FCSTD DOCUMENT  (FreeCAD 0.21R33771 (Git))
Label: ass-tornio
License: All rights reserved
LicenseURL: https://en.wikipedia.org/wiki/All_rights_reserved
objects: App::Link×56, App::DocumentObjectGroup×4, Part::FeaturePython×4, App::AnnotationLabel×4, PartDesign::CoordinateSystem×1, App::FeaturePython×1, App::Part×1
note: 5 computed .brp shape members not serialized (recipe doc carries the construction recipe); baked Part::Feature solids carry a one-line shape summary decoded from their .brp
EXTERNAL_REF file=../Pattino-20.FCStd obj=LCS_Pattino_20
EXTERNAL_REF file=../Pattino-20.FCStd obj=Body
EXTERNAL_REF file=../PiastraCarroUtensile.FCStd obj=LCS_PiastraCarro
EXTERNAL_REF file=../PiastraCarroUtensile.FCStd obj=Body
EXTERNAL_REF file=../TORRETTA/Pattino-15.FCStd obj=LCS_Pattino1
EXTERNAL_REF file=../PiastraTorretta.FCStd obj=LCS_PiastraTorretta
EXTERNAL_REF file=../PiastraTorretta.FCStd obj=Body
EXTERNAL_REF file=../BloccoMandrino/FlangiaSupportoMandrino.FCStd obj=LCS_
EXTERNAL_REF file=../Profilo-C-basamento.FCStd obj=LCS_ProfiloCbasamento
EXTERNAL_REF file=../BloccoMandrino/FlangiaSupportoMandrino.FCStd obj=Body
EXTERNAL_REF file=../SupportoSingoloVite16x4.FCStd obj=LCS_SupportoSingoloVite16x4
EXTERNAL_REF file=../ViteCarro16x4.FCStd obj=LCS_ViteCarro16x4
EXTERNAL_REF file=../ViteCarro16x4.FCStd obj=Body
EXTERNAL_REF file=../SupportoSingoloVite16x4.FCStd obj=Body
EXTERNAL_REF file=../Chiocciola16x4.FCStd obj=LCS_Chiociola16X4
EXTERNAL_REF file=../StaffaChiocciola16x4.FCStd obj=LCS_StaffaChiocciola16x4
EXTERNAL_REF file=../Chiocciola16x4.FCStd obj=Body
EXTERNAL_REF file=../StaffaChiocciola16x4.FCStd obj=Body
EXTERNAL_REF file=../SupportoDoppioVite16x4.FCStd obj=LCS_SupportoDoppioVite16x4
EXTERNAL_REF file=../SupportoDoppioVite16x4.FCStd obj=Body
EXTERNAL_REF file=../Piedino40x40.FCStd obj=LCS_piedino40x40
EXTERNAL_REF file=../Piedino40x40.FCStd obj=Body
EXTERNAL_REF file=../Guida-quadra-20-800.FCStd obj=LCS_GuidaQuadrata_20x800
EXTERNAL_REF file=../Contropunta/PiastraContropunta.FCStd obj=LCS_PiastraContropunta
EXTERNAL_REF file=../Contropunta/PiastraContropunta.FCStd obj=Body
EXTERNAL_REF file=../BloccoMandrino/Flagia-Mandrino.FCStd obj=LCS_FllangiaSupportoMandrino
EXTERNAL_REF file=../BloccoMandrino/Reggispinta35x52x12.FCStd obj=LCS_Reggispinta35x12
EXTERNAL_REF file=../BloccoMandrino/Reggispinta35x52x12.FCStd obj=Body
EXTERNAL_REF file=../TORRETTA/Guida-quadra-15-300.FCStd obj=LCS_GuidoQuadra15x300
EXTERNAL_REF file=../BloccoMandrino/PiastraMandrinoRotante.FCStd obj=LCS_PiastraRotazioneUtensile
EXTERNAL_REF file=../TORRETTA/Guida-quadra-15-300.FCStd obj=Body
EXTERNAL_REF file=../TORRETTA/Pattino-15.FCStd obj=Body
EXTERNAL_REF file=../BloccoMandrino/PiastraMandrinoRotante.FCStd obj=Body
EXTERNAL_REF file=../TORRETTA/SupportoChiocciolaRicircolo12.FCStd obj=LCS_SupportoChiocciolaRicircolo12
EXTERNAL_REF file=../TORRETTA/SupportoChiocciolaRicircolo12.FCStd obj=Body
EXTERNAL_REF file=../TORRETTA/Chiocciola10x2.FCStd obj=LCS_Chiocciola12x2
EXTERNAL_REF file=../TORRETTA/Chiocciola10x2.FCStd obj=Body
EXTERNAL_REF file=../TORRETTA/ViteTrapezioT10.FCStd obj=LCS_ViteTrapezioT10
EXTERNAL_REF file=../TORRETTA/ViteTrapezioT10.FCStd obj=Body
EXTERNAL_REF file=../TORRETTA/TorrettaPortaUtensile.FCStd obj=LCS_TorrettaPortaUtensile
EXTERNAL_REF file=../TORRETTA/TorrettaPortaUtensile.FCStd obj=Body
EXTERNAL_REF file=../BloccoMandrino/Motore-P60B13150HXS00M- SANYO.FCStd obj=LCS_Motore_sanyoP60
EXTERNAL_REF file=../BloccoMandrino/Motore-P60B13150HXS00M- SANYO.FCStd obj=Body
EXTERNAL_REF file=../BloccoMandrino/FlangiaCuscinettoAlberoMandrino.FCStd obj=LCS_FlangiaCuscinettoMandrino
EXTERNAL_REF file=../BloccoMandrino/FlangiaCuscinettoAlberoMandrino.FCStd obj=Body
EXTERNAL_REF file=../BloccoMandrino/CuscinettoSfere30x52x12.FCStd obj=LCS_Cuscinetto30x52x12
EXTERNAL_REF file=../BloccoMandrino/CuscinettoSfere30x52x12.FCStd obj=Body
EXTERNAL_REF file=../Profilo-C-basamento.FCStd obj=Body
EXTERNAL_REF file=../Piatto40x10x850.FCStd obj=LCS_Piatto40x10
EXTERNAL_REF file=../Piatto40x10x850.FCStd obj=Body
EXTERNAL_REF file=../Guida-quadra-20-800.FCStd obj=Body
EXTERNAL_REF file=../Puleggia70-Foro28.FCStd obj=LCS_Puleggia70
EXTERNAL_REF file=../Puleggia70-Foro28.FCStd obj=Body
EXTERNAL_REF file=../BloccoMandrino/Albero-Mandrino30.FCStd obj=LCS_AlberoMandrino
EXTERNAL_REF file=../BloccoMandrino/Flagia-Mandrino.FCStd obj=Body
EXTERNAL_REF file=../BloccoMandrino/Albero-Mandrino30.FCStd obj=Body
EXTERNAL_REF file=../BloccoMandrino/Mandrino.FCStd obj=LCS_Mandrino
EXTERNAL_REF file=../BloccoMandrino/Mandrino.FCStd obj=Body
EXTERNAL_REF file=../DistanzialeBasamentoC.FCStd obj=LCS_DistanzialeBasamentoC
EXTERNAL_REF file=../DistanzialeBasamentoC.FCStd obj=Body
EXTERNAL_REF file=../Cremagliera-M1.FCStd obj=LCS_Cremagliera_800
EXTERNAL_REF file=../Cremagliera-M1.FCStd obj=Part
EXTERNAL_REF file=../PiastraAvanzamentoCarro.FCStd obj=LCS_PiastraAvanzamentoUtensile
EXTERNAL_REF file=../Pignone13-M1.FCStd obj=LCS_Pignone13M1
EXTERNAL_REF file=../Pignone13-M1.FCStd obj=Part
EXTERNAL_REF file=../TORRETTA/PiastraAvanzamentoUtensile.FCStd obj=LCS_PiastraAvanzamentoViteUtensile
EXTERNAL_REF file=../TORRETTA/PiastraAvanzamentoUtensile.FCStd obj=Body
EXTERNAL_REF file=../PiastraAvanzamentoCarro.FCStd obj=Body
EXTERNAL_REF file=../Assembly-SgancioViteCarro.FCStd obj=LCS_Origin
EXTERNAL_REF file=../Assembly-SgancioViteCarro.FCStd obj=Assembly
EXTERNAL_REF file=../BloccoMandrino/IngranaggioM35.FCStd obj=LCS_1_Ingranaggio35
EXTERNAL_REF file=../BloccoMandrino/IngranaggioM35.FCStd obj=Body

FEATURE [App::DocumentObjectGroup] Parts
FEATURE [PartDesign::CoordinateSystem] LCS_Origin
  AttacherType = Attacher::AttachEngine3D
  MapMode = 2
  Support = -> [X_Axis]
FEATURE [App::DocumentObjectGroup] Constraints
FEATURE [App::DocumentObjectGroup] Configurations
FEATURE [App::Link] Pattino20_2_link
  AttachedBy = #LCS_Pattino_20
  AttachedTo = Pattino20_0_link#LCS_Pattino_20
  AttachmentOffset = pos=(0,0,85) rot=(0,0,1;0rad)
  LinkPlacement = pos=(86,-115,360) rot=(0,0,1;4.71239rad)
  LinkedObject = -> <external ../Pattino-20.FCStd>#Body
  Placement = pos=(86,-115,360) rot=(0,0,1;4.71239rad)
  SolverId = Asm4EE
  expr: Placement = Pattino20_0_link.Placement * Pattino_20#LCS_Pattino_20.Placement * AttachmentOffset * Pattino_20#LCS_Pattino_20.Placement ^ -1
FEATURE [App::Link] PiastraCarro_link  label="PiastraCarro-link"
  AttachedBy = #LCS_PiastraCarro
  AttachedTo = Pattino20_0_link#LCS_Pattino_20
  AttachmentOffset = pos=(-142,25,83) rot=(1,0,0;1.5708rad)
  LinkPlacement = pos=(126,127,423) rot=(-0.57735,-0.57735,0.57735;4.18879rad)
  LinkedObject = -> <external ../PiastraCarroUtensile.FCStd>#Body
  Placement = pos=(126,127,423) rot=(-0.57735,-0.57735,0.57735;4.18879rad)
  SolverId = Asm4EE
  expr: Placement = Pattino20_0_link.Placement * Pattino_20#LCS_Pattino_20.Placement * AttachmentOffset * PiastraCarroUtensile#LCS_PiastraCarro.Placement ^ -1
FEATURE [App::Link] PiastraTorretta_link
  AttachedBy = #LCS_PiastraTorretta
  AttachedTo = Pattino_1_15_link#LCS_Pattino1
  AttachmentOffset = pos=(-13,24,23) rot=(0,-0.707107,-0.707107;3.14159rad)
  LinkPlacement = pos=(161,87,358) rot=(0.707107,0,0.707107;3.14159rad)
  LinkedObject = -> <external ../PiastraTorretta.FCStd>#Body
  Placement = pos=(161,87,358) rot=(0.707107,0,0.707107;3.14159rad)
  SolverId = Asm4EE
  expr: Placement = Pattino_1_15_link.Placement * Pattino_15#LCS_Pattino1.Placement * AttachmentOffset * PiastraTorretta#LCS_PiastraTorretta.Placement ^ -1
FEATURE [App::Link] Pattino20_4_link  label="Pattino20-3_link"
  AttachedBy = #LCS_Pattino_20
  AttachedTo = Pattino20_3_link#LCS_Pattino_20
  AttachmentOffset = pos=(0,0,85) rot=(0,0,1;0rad)
  LinkPlacement = pos=(86,75,360) rot=(0,0,1;4.71239rad)
  LinkedObject = -> <external ../Pattino-20.FCStd>#Body
  Placement = pos=(86,75,360) rot=(0,0,1;4.71239rad)
  SolverId = Asm4EE
  expr: Placement = Pattino20_3_link.Placement * Pattino_20#LCS_Pattino_20.Placement * AttachmentOffset * Pattino_20#LCS_Pattino_20.Placement ^ -1
FEATURE [App::Link] FlangiaSupportoMandrino1_link  label="FlangiaSupportoMandrino1-link"
  AttachedBy = #LCS_
  AttachedTo = Profilo_C_basamento_link#LCS_ProfiloCbasamento
  AttachmentOffset = pos=(80,35,230) rot=(0.57735,-0.57735,0.57735;4.18879rad)
  LinkPlacement = pos=(80,35,230) rot=(0.57735,-0.57735,0.57735;4.18879rad)
  LinkedObject = -> <external ../BloccoMandrino/FlangiaSupportoMandrino.FCStd>#Body
  Placement = pos=(80,35,230) rot=(0.57735,-0.57735,0.57735;4.18879rad)
  SolverId = Asm4EE
  expr: Placement = Profilo_C_basamento_link.Placement * Profilo_C_basamento#LCS_ProfiloCbasamento.Placement * AttachmentOffset * FlangiaSupportoMandrino#LCS_.Placement ^ -1
FEATURE [App::Link] FlangiaSupportoMandrino2_link  label="FlangiaSupportoMandrino2-link"
  AttachedBy = #LCS_
  AttachedTo = FlangiaSupportoMandrino1_link#LCS_
  AttachmentOffset = pos=(0,220,0) rot=(0,0,1;0rad)
  LinkPlacement = pos=(80,35,10) rot=(0.57735,-0.57735,0.57735;4.18879rad)
  LinkedObject = -> <external ../BloccoMandrino/FlangiaSupportoMandrino.FCStd>#Body
  Placement = pos=(80,35,10) rot=(0.57735,-0.57735,0.57735;4.18879rad)
  SolverId = Asm4EE
  expr: Placement = FlangiaSupportoMandrino1_link.Placement * FlangiaSupportoMandrino#LCS_.Placement * AttachmentOffset * FlangiaSupportoMandrino#LCS_.Placement ^ -1
FEATURE [App::Link] ViteCarro16x4_link  label="ViteCarro16x4-link"
  AttachedBy = #LCS_ViteCarro16x4
  AttachedTo = SuppotoSingoloVite16x4_link#LCS_SupportoSingoloVite16x4
  AttachmentOffset = pos=(0,0,-576) rot=(0,1,0;4.71239rad)
  LinkPlacement = pos=(35,90,274) rot=(0,1,0;4.71239rad)
  LinkedObject = -> <external ../ViteCarro16x4.FCStd>#Body
  Placement = pos=(35,90,274) rot=(0,1,0;4.71239rad)
  SolverId = Asm4EE
  expr: Placement = SuppotoSingoloVite16x4_link.Placement * SupportoSingoloVite16x4#LCS_SupportoSingoloVite16x4.Placement * AttachmentOffset * ViteCarro16x4#LCS_ViteCarro16x4.Placement ^ -1
FEATURE [App::Link] SuppotoSingoloVite16x4_link  label="SuppotoSingoloVite16x4-link"
  AttachedBy = #LCS_SupportoSingoloVite16x4
  AttachedTo = Profilo_C_basamento_link#LCS_ProfiloCbasamento
  AttachmentOffset = pos=(35,90,850) rot=(0,0,1;0rad)
  LinkPlacement = pos=(35,90,850) rot=(0,0,1;0rad)
  LinkedObject = -> <external ../SupportoSingoloVite16x4.FCStd>#Body
  Placement = pos=(35,90,850) rot=(0,0,1;0rad)
  SolverId = Asm4EE
  expr: Placement = Profilo_C_basamento_link.Placement * Profilo_C_basamento#LCS_ProfiloCbasamento.Placement * AttachmentOffset * SupportoSingoloVite16x4#LCS_SupportoSingoloVite16x4.Placement ^ -1
FEATURE [App::Link] Chiocciola16x4_link  label="Chiocciola16x4-link"
  AttachedBy = #LCS_Chiociola16X4
  AttachedTo = StaffaChiocciola16x4#LCS_StaffaChiocciola16x4
  AttachmentOffset = pos=(55,20,-5) rot=(0,1,0;4.71239rad)
  LinkPlacement = pos=(56,-40,404) rot=(-0.707107,0,-0.707107;3.14159rad)
  LinkedObject = -> <external ../Chiocciola16x4.FCStd>#Body
  Placement = pos=(56,-40,404) rot=(-0.707107,0,-0.707107;3.14159rad)
  SolverId = Asm4EE
  expr: Placement = StaffaChiocciola16x4.Placement * StaffaChiocciola16x4#LCS_StaffaChiocciola16x4.Placement * AttachmentOffset * Chiocciola16x4#LCS_Chiociola16X4.Placement ^ -1
FEATURE [App::Link] StaffaChiocciola16x4
  AttachedBy = #LCS_StaffaChiocciola16x4
  AttachedTo = PiastraCarro_link#LCS_PiastraCarro
  AttachmentOffset = pos=(47,51,0) rot=(-0.57735,-0.57735,-0.57735;2.0944rad)
  LinkPlacement = pos=(111,-20,409) rot=(0,0,1;3.14159rad)
  LinkedObject = -> <external ../StaffaChiocciola16x4.FCStd>#Body
  Placement = pos=(111,-20,409) rot=(0,0,1;3.14159rad)
  SolverId = Asm4EE
  expr: Placement = PiastraCarro_link.Placement * PiastraCarroUtensile#LCS_PiastraCarro.Placement * AttachmentOffset * StaffaChiocciola16x4#LCS_StaffaChiocciola16x4.Placement ^ -1
FEATURE [App::Link] SupportoDoppioVite16x4
  AttachedBy = #LCS_SupportoDoppioVite16x4
  AttachedTo = SuppotoSingoloVite16x4_link#LCS_SupportoSingoloVite16x4
  AttachmentOffset = pos=(0,0,-560) rot=(0,0,1;0rad)
  LinkPlacement = pos=(35,90,290) rot=(0,0,1;0rad)
  LinkedObject = -> <external ../SupportoDoppioVite16x4.FCStd>#Body
  Placement = pos=(35,90,290) rot=(0,0,1;0rad)
  SolverId = Asm4EE
  expr: Placement = SuppotoSingoloVite16x4_link.Placement * SupportoSingoloVite16x4#LCS_SupportoSingoloVite16x4.Placement * AttachmentOffset * SupportoDoppioVite16x4#LCS_SupportoDoppioVite16x4.Placement ^ -1
FEATURE [App::Link] Piedino40x40_link  label="Piedino40x40-link"
  AttachedBy = #LCS_piedino40x40
  AttachedTo = Profilo_C_basamento_link#LCS_ProfiloCbasamento
  AttachmentOffset = pos=(55,85,-20) rot=(0.57735,-0.57735,-0.57735;2.0944rad)
  LinkPlacement = pos=(55,85,-20) rot=(0.57735,-0.57735,-0.57735;2.0944rad)
  LinkedObject = -> <external ../Piedino40x40.FCStd>#Body
  Placement = pos=(55,85,-20) rot=(0.57735,-0.57735,-0.57735;2.0944rad)
  SolverId = Asm4EE
  expr: Placement = Profilo_C_basamento_link.Placement * Profilo_C_basamento#LCS_ProfiloCbasamento.Placement * AttachmentOffset * Piedino40x40#LCS_piedino40x40.Placement ^ -1
FEATURE [App::Link] Piedino40x40_1_link  label="Piedino40x40-1-link"
  AttachedBy = #LCS_piedino40x40
  AttachedTo = Piedino40x40_link#LCS_piedino40x40
  AttachmentOffset = pos=(0,1120,0) rot=(0,0,1;4.71239rad)
  LinkPlacement = pos=(55,85,1100) rot=(-0.707107,0,0.707107;3.14159rad)
  LinkedObject = -> <external ../Piedino40x40.FCStd>#Body
  Placement = pos=(55,85,1100) rot=(-0.707107,0,0.707107;3.14159rad)
  SolverId = Asm4EE
  expr: Placement = Piedino40x40_link.Placement * Piedino40x40#LCS_piedino40x40.Placement * AttachmentOffset * Piedino40x40#LCS_piedino40x40.Placement ^ -1
FEATURE [App::Link] Piedino40x40_2_link  label="Piedino40x40-2-link"
  AttachedBy = #LCS_piedino40x40
  AttachedTo = Profilo_C_basamento_2_link#LCS_ProfiloCbasamento
  AttachmentOffset = pos=(10,45,-20) rot=(0.57735,0.57735,0.57735;2.0944rad)
  LinkPlacement = pos=(70,-125,-20) rot=(-0.57735,0.57735,0.57735;4.18879rad)
  LinkedObject = -> <external ../Piedino40x40.FCStd>#Body
  Placement = pos=(70,-125,-20) rot=(-0.57735,0.57735,0.57735;4.18879rad)
  SolverId = Asm4EE
  expr: Placement = Profilo_C_basamento_2_link.Placement * Profilo_C_basamento#LCS_ProfiloCbasamento.Placement * AttachmentOffset * Piedino40x40#LCS_piedino40x40.Placement ^ -1
FEATURE [App::Link] Piedino40x40_3_link  label="Piedino40x40-3-link"
  AttachedBy = #LCS_piedino40x40
  AttachedTo = Piedino40x40_2_link#LCS_piedino40x40
  AttachmentOffset = pos=(0,1120,0) rot=(0,0,1;4.71239rad)
  LinkPlacement = pos=(70,-125,1100) rot=(0.707107,0,-0.707107;3.14159rad)
  LinkedObject = -> <external ../Piedino40x40.FCStd>#Body
  Placement = pos=(70,-125,1100) rot=(0.707107,0,-0.707107;3.14159rad)
  SolverId = Asm4EE
  expr: Placement = Piedino40x40_2_link.Placement * Piedino40x40#LCS_piedino40x40.Placement * AttachmentOffset * Piedino40x40#LCS_piedino40x40.Placement ^ -1
FEATURE [App::Link] Pattino_0_contropunta_link  label="Pattino-0-contropunta-link"
  AttachedBy = #LCS_Pattino_20
  AttachedTo = GuidaQuadra_20x800_2_link#LCS_GuidaQuadrata_20x800
  AttachmentOffset = pos=(20,5,780) rot=(0,1,0;3.14159rad)
  LinkPlacement = pos=(87,-155,1055) rot=(-0.707107,-0.707107,0;3.14159rad)
  LinkedObject = -> <external ../Pattino-20.FCStd>#Body
  Placement = pos=(87,-155,1055) rot=(-0.707107,-0.707107,0;3.14159rad)
  SolverId = Asm4EE
  expr: Placement = GuidaQuadra_20x800_2_link.Placement * Guida_quadra_20_800#LCS_GuidaQuadrata_20x800.Placement * AttachmentOffset * Pattino_20#LCS_Pattino_20.Placement ^ -1
FEATURE [App::Link] Pattino_1_contropunta_link  label="Pattino-1-contropunta-link"
  AttachedBy = #LCS_Pattino_20
  AttachedTo = Pattino_0_contropunta_link#LCS_Pattino_20
  AttachmentOffset = pos=(0,0,85) rot=(0,0,1;0rad)
  LinkPlacement = pos=(87,-155,970) rot=(-0.707107,-0.707107,0;3.14159rad)
  LinkedObject = -> <external ../Pattino-20.FCStd>#Body
  Placement = pos=(87,-155,970) rot=(-0.707107,-0.707107,0;3.14159rad)
  SolverId = Asm4EE
  expr: Placement = Pattino_0_contropunta_link.Placement * Pattino_20#LCS_Pattino_20.Placement * AttachmentOffset * Pattino_20#LCS_Pattino_20.Placement ^ -1
FEATURE [App::Link] Pattino_3_contropunta_link  label="Pattino-3-contropunta-link"
  AttachedBy = #LCS_Pattino_20
  AttachedTo = Pattino20_2_contropiastra#LCS_Pattino_20
  AttachmentOffset = pos=(0,0,85) rot=(0,0,1;0rad)
  LinkPlacement = pos=(87,35,970) rot=(-0.707107,-0.707107,0;3.14159rad)
  LinkedObject = -> <external ../Pattino-20.FCStd>#Body
  Placement = pos=(87,35,970) rot=(-0.707107,-0.707107,0;3.14159rad)
  SolverId = Asm4EE
  expr: Placement = Pattino20_2_contropiastra.Placement * Pattino_20#LCS_Pattino_20.Placement * AttachmentOffset * Pattino_20#LCS_Pattino_20.Placement ^ -1
FEATURE [App::Link] PiastraContropunta_link  label="PiastraContropunta-link"
  AttachedBy = #LCS_PiastraContropunta
  AttachedTo = Pattino_0_contropunta_link#LCS_Pattino_20
  AttachmentOffset = pos=(-7,25,17) rot=(0.707107,0,0.707107;3.14159rad)
  LinkPlacement = pos=(112,-162,1038) rot=(-0.57735,0.57735,0.57735;2.0944rad)
  LinkedObject = -> <external ../Contropunta/PiastraContropunta.FCStd>#Body
  Placement = pos=(112,-162,1038) rot=(-0.57735,0.57735,0.57735;2.0944rad)
  SolverId = Asm4EE
  expr: Placement = Pattino_0_contropunta_link.Placement * Pattino_20#LCS_Pattino_20.Placement * AttachmentOffset * PiastraContropunta#LCS_PiastraContropunta.Placement ^ -1
FEATURE [App::Link] Reggispinta35_12_link  label="Reggispinta35-12-link"
  AttachedBy = #LCS_Reggispinta35x12
  AttachedTo = FlangiaMandrino_link#LCS_FllangiaSupportoMandrino
  AttachmentOffset = pos=(-2,0,0) rot=(0,1,0;1.5708rad)
  LinkPlacement = pos=(190,-40,233) rot=(0,0,-1;4.71239rad)
  LinkedObject = -> <external ../BloccoMandrino/Reggispinta35x52x12.FCStd>#Body
  Placement = pos=(190,-40,233) rot=(0,0,-1;4.71239rad)
  SolverId = Asm4EE
  expr: Placement = FlangiaMandrino_link.Placement * Flagia_Mandrino#LCS_FllangiaSupportoMandrino.Placement * AttachmentOffset * Reggispinta35x52x12#LCS_Reggispinta35x12.Placement ^ -1
FEATURE [App::Link] GuidoQuadra15x300_link  label="GuidaQuadra15x300-link"
  AttachedBy = #LCS_GuidoQuadra15x300
  AttachedTo = PiastraRotazioneUtensile_link#LCS_PiastraRotazioneUtensile
  AttachmentOffset = pos=(-100,30,0) rot=(-0.57735,-0.57735,-0.57735;4.18879rad)
  LinkPlacement = pos=(136,127,328) rot=(-0.57735,-0.57735,0.57735;4.18879rad)
  LinkedObject = -> <external ../TORRETTA/Guida-quadra-15-300.FCStd>#Body
  Placement = pos=(136,127,328) rot=(-0.57735,-0.57735,0.57735;4.18879rad)
  SolverId = Asm4EE
  expr: Placement = PiastraRotazioneUtensile_link.Placement * PiastraMandrinoRotante#LCS_PiastraRotazioneUtensile.Placement * AttachmentOffset * Guida_quadra_15_300#LCS_GuidoQuadra15x300.Placement ^ -1
FEATURE [App::Link] GuidoQuadra_2_15x300_link  label="GuidaQuadra-2-15x300-link"
  AttachedBy = #LCS_GuidoQuadra15x300
  AttachedTo = GuidoQuadra15x300_link#LCS_GuidoQuadra15x300
  AttachmentOffset = pos=(-60,0,0) rot=(0,0,1;0rad)
  LinkPlacement = pos=(136,127,388) rot=(-0.57735,-0.57735,0.57735;4.18879rad)
  LinkedObject = -> <external ../TORRETTA/Guida-quadra-15-300.FCStd>#Body
  Placement = pos=(136,127,388) rot=(-0.57735,-0.57735,0.57735;4.18879rad)
  SolverId = Asm4EE
  expr: Placement = GuidoQuadra15x300_link.Placement * Guida_quadra_15_300#LCS_GuidoQuadra15x300.Placement * AttachmentOffset * Guida_quadra_15_300#LCS_GuidoQuadra15x300.Placement ^ -1
FEATURE [App::Link] Pattino_1_15_link  label="Pattino-1-15-link"
  AttachedBy = #LCS_Pattino1
  AttachedTo = GuidoQuadra15x300_link#LCS_GuidoQuadra15x300
  AttachmentOffset = pos=(-17,1,17) rot=(0,0,1;0rad)
  LinkPlacement = pos=(137,110,345) rot=(-0.57735,-0.57735,0.57735;4.18879rad)
  LinkedObject = -> <external ../TORRETTA/Pattino-15.FCStd>#Body
  Placement = pos=(137,110,345) rot=(-0.57735,-0.57735,0.57735;4.18879rad)
  SolverId = Asm4EE
  expr: Placement = GuidoQuadra15x300_link.Placement * Guida_quadra_15_300#LCS_GuidoQuadra15x300.Placement * AttachmentOffset * Pattino_15#LCS_Pattino1.Placement ^ -1
FEATURE [App::Link] LCS_Pattino3_15_link  label="Pattino3-15-link"
  AttachedBy = #LCS_Pattino1
  AttachedTo = Pattino_1_15_link#LCS_Pattino1
  AttachmentOffset = pos=(-60,0,0) rot=(0,0,1;0rad)
  LinkPlacement = pos=(137,110,405) rot=(-0.57735,-0.57735,0.57735;4.18879rad)
  LinkedObject = -> <external ../TORRETTA/Pattino-15.FCStd>#Body
  Placement = pos=(137,110,405) rot=(-0.57735,-0.57735,0.57735;4.18879rad)
  SolverId = Asm4EE
  expr: Placement = Pattino_1_15_link.Placement * Pattino_15#LCS_Pattino1.Placement * AttachmentOffset * Pattino_15#LCS_Pattino1.Placement ^ -1
FEATURE [App::FeaturePython] Variables  label="0.000000"  # WARN: FeaturePython — macro-defined, semantics opaque (R4)
  Angle = 0
  Type = App::PropertyContainer
  expr: Label = Angle
FEATURE [App::Link] Pattino20_0_link  label="Pattino20-0-link"
  AttachedBy = #LCS_Pattino_20
  AttachedTo = GuidaQuadra_20x800_2_link#LCS_GuidaQuadrata_20x800
  AttachmentOffset = pos=(-20,4,0) rot=(0,0,1;0rad)
  LinkPlacement = pos=(86,-115,275) rot=(0,0,1;4.71239rad)
  LinkedObject = -> <external ../Pattino-20.FCStd>#Body
  Placement = pos=(86,-115,275) rot=(0,0,1;4.71239rad)
  SolverId = Asm4EE
  expr: Placement = GuidaQuadra_20x800_2_link.Placement * Guida_quadra_20_800#LCS_GuidaQuadrata_20x800.Placement * AttachmentOffset * Pattino_20#LCS_Pattino_20.Placement ^ -1
FEATURE [App::Link] Pattino20_3_link  label="Pattino20-2-link"
  AttachedBy = #LCS_Pattino_20
  AttachedTo = Pattino20_0_link#LCS_Pattino_20
  AttachmentOffset = pos=(-190,0,0) rot=(0,0,1;0rad)
  LinkPlacement = pos=(86,75,275) rot=(0,0,1;4.71239rad)
  LinkedObject = -> <external ../Pattino-20.FCStd>#Body
  Placement = pos=(86,75,275) rot=(0,0,1;4.71239rad)
  SolverId = Asm4EE
  expr: Placement = Pattino20_0_link.Placement * Pattino_20#LCS_Pattino_20.Placement * AttachmentOffset * Pattino_20#LCS_Pattino_20.Placement ^ -1
FEATURE [App::Link] PiastraRotazioneUtensile_link  label="PiastraRotazioneUtensile-link"
  AttachedBy = #LCS_PiastraRotazioneUtensile
  AttachedTo = PiastraCarro_link#LCS_PiastraCarro
  AttachmentOffset = pos=(0,0,-25) rot=(1,0,0;3.14159rad)
  LinkPlacement = pos=(126,157,318) rot=(-0.707107,0,-0.707107;3.14159rad)
  LinkedObject = -> <external ../BloccoMandrino/PiastraMandrinoRotante.FCStd>#Body
  Placement = pos=(126,157,318) rot=(-0.707107,0,-0.707107;3.14159rad)
  SolverId = Asm4EE
  expr: .AttachmentOffset.Rotation.Yaw = Variables.Angle
  expr: .Placement.Rotation.Angle = 0
  expr: .Placement.Rotation.Pitch = Variables.Angle
  expr: Placement = PiastraCarro_link.Placement * PiastraCarroUtensile#LCS_PiastraCarro.Placement * AttachmentOffset * PiastraMandrinoRotante#LCS_PiastraRotazioneUtensile.Placement ^ -1
FEATURE [App::Link] Pattino20_2_contropiastra  label="Pattino20-2-contropiastra"
  AttachedBy = #LCS_Pattino_20
  AttachedTo = Pattino_0_contropunta_link#LCS_Pattino_20
  AttachmentOffset = pos=(190,0,0) rot=(0,0,1;0rad)
  LinkPlacement = pos=(87,35,1055) rot=(-0.707107,-0.707107,0;3.14159rad)
  LinkedObject = -> <external ../Pattino-20.FCStd>#Body
  Placement = pos=(87,35,1055) rot=(-0.707107,-0.707107,0;3.14159rad)
  SolverId = Asm4EE
  expr: Placement = Pattino_0_contropunta_link.Placement * Pattino_20#LCS_Pattino_20.Placement * AttachmentOffset * Pattino_20#LCS_Pattino_20.Placement ^ -1
FEATURE [App::Link] SuportoChiocciola12_link  label="SuportoChiocciola12-link"
  AttachedBy = #LCS_SupportoChiocciolaRicircolo12
  AttachedTo = PiastraTorretta_link#LCS_PiastraTorretta
  AttachmentOffset = pos=(0,-32,-13) rot=(1,0,0;4.71239rad)
  LinkPlacement = pos=(148,119,358) rot=(-0.57735,0.57735,-0.57735;4.18879rad)
  LinkedObject = -> <external ../TORRETTA/SupportoChiocciolaRicircolo12.FCStd>#Body
  Placement = pos=(148,119,358) rot=(-0.57735,0.57735,-0.57735;4.18879rad)
  SolverId = Asm4EE
  expr: Placement = PiastraTorretta_link.Placement * PiastraTorretta#LCS_PiastraTorretta.Placement * AttachmentOffset * SupportoChiocciolaRicircolo12#LCS_SupportoChiocciolaRicircolo12.Placement ^ -1
FEATURE [App::Link] Chiocciola12x2_link  label="Chiocciola12x2-link"
  AttachedBy = #LCS_Chiocciola12x2
  AttachedTo = SuportoChiocciola12_link#LCS_SupportoChiocciolaRicircolo12
  AttachmentOffset = pos=(0,0,0) rot=(0,1,0;3.14159rad)
  LinkPlacement = pos=(148,119,358) rot=(0.57735,-0.57735,-0.57735;4.18879rad)
  LinkedObject = -> <external ../TORRETTA/Chiocciola10x2.FCStd>#Body
  Placement = pos=(148,119,358) rot=(0.57735,-0.57735,-0.57735;4.18879rad)
  SolverId = Asm4EE
  expr: Placement = SuportoChiocciola12_link.Placement * SupportoChiocciolaRicircolo12#LCS_SupportoChiocciolaRicircolo12.Placement * AttachmentOffset * Chiocciola10x2#LCS_Chiocciola12x2.Placement ^ -1
FEATURE [App::Link] ViteTrapezioT10_link  label="ViteTrapezioT10-link"
  AttachedBy = #LCS_ViteTrapezioT10
  AttachedTo = Chiocciola12x2_link#LCS_Chiocciola12x2
  AttachmentOffset = pos=(0,0,60) rot=(0,1,0;3.14159rad)
  LinkPlacement = pos=(148,179,358) rot=(0.57735,-0.57735,0.57735;2.0944rad)
  LinkedObject = -> <external ../TORRETTA/ViteTrapezioT10.FCStd>#Body
  Placement = pos=(148,179,358) rot=(0.57735,-0.57735,0.57735;2.0944rad)
  SolverId = Asm4EE
  expr: Placement = Chiocciola12x2_link.Placement * Chiocciola10x2#LCS_Chiocciola12x2.Placement * AttachmentOffset * ViteTrapezioT10#LCS_ViteTrapezioT10.Placement ^ -1
FEATURE [App::Link] TorrettaPortaUtensile_link  label="TorrettaPortaUtensile-link"
  AttachedBy = #LCS_TorrettaPortaUtensile
  AttachedTo = PiastraTorretta_link#LCS_PiastraTorretta
  AttachmentOffset = pos=(0,0,10) rot=(0,0,1;0rad)
  LinkPlacement = pos=(171,87,358) rot=(0,0,1;1.5708rad)
  LinkedObject = -> <external ../TORRETTA/TorrettaPortaUtensile.FCStd>#Body
  Placement = pos=(171,87,358) rot=(0,0,1;1.5708rad)
  SolverId = Asm4EE
  expr: Placement = PiastraTorretta_link.Placement * PiastraTorretta#LCS_PiastraTorretta.Placement * AttachmentOffset * TorrettaPortaUtensile#LCS_TorrettaPortaUtensile.Placement ^ -1
FEATURE [App::Link] Motore_P60_Sanyo_link  label="Motore-P60-Sanyo-link"
  AttachedBy = #LCS_Motore_sanyoP60
  AttachedTo = FlangiaSupportoMandrino1_link#LCS_
  AttachmentOffset = pos=(75,205,-80) rot=(0,0,-1;3.14159rad)
  LinkPlacement = pos=(4.26e-14,-40,25) rot=(0,0,1;1.5708rad)
  LinkedObject = -> <external ../BloccoMandrino/Motore-P60B13150HXS00M- SANYO.FCStd>#Body
  Placement = pos=(4.26e-14,-40,25) rot=(0,0,1;1.5708rad)
  SolverId = Asm4EE
  expr: Placement = FlangiaSupportoMandrino1_link.Placement * FlangiaSupportoMandrino#LCS_.Placement * AttachmentOffset * Motore_P60B13150HXS00M__SANYO#LCS_Motore_sanyoP60.Placement ^ -1
FEATURE [App::Link] FlangiaCuscinettoMandrino_link  label="FlangiaCuscinettoMandrino-link"
  AttachedBy = #LCS_FlangiaCuscinettoMandrino
  AttachedTo = FlangiaSupportoMandrino1_link#LCS_
  AttachmentOffset = pos=(75,18,110) rot=(1,0,0;1.5708rad)
  LinkPlacement = pos=(190,-40,212) rot=(0,0,1;4.71239rad)
  LinkedObject = -> <external ../BloccoMandrino/FlangiaCuscinettoAlberoMandrino.FCStd>#Body
  Placement = pos=(190,-40,212) rot=(0,0,1;4.71239rad)
  SolverId = Asm4EE
  expr: Placement = FlangiaSupportoMandrino1_link.Placement * FlangiaSupportoMandrino#LCS_.Placement * AttachmentOffset * FlangiaCuscinettoAlberoMandrino#LCS_FlangiaCuscinettoMandrino.Placement ^ -1
FEATURE [App::Link] CuscinettoSfere30x52x12_link  label="CuscinettoSfere30x52x12-link"
  AttachedBy = #LCS_Cuscinetto30x52x12
  AttachedTo = FlangiaCuscinettoMandrino_link#LCS_FlangiaCuscinettoMandrino
  AttachmentOffset = pos=(0,0,3) rot=(0,0,1;0rad)
  LinkPlacement = pos=(190,-40,215) rot=(0,0,1;4.71239rad)
  LinkedObject = -> <external ../BloccoMandrino/CuscinettoSfere30x52x12.FCStd>#Body
  Placement = pos=(190,-40,215) rot=(0,0,1;4.71239rad)
  SolverId = Asm4EE
  expr: Placement = FlangiaCuscinettoMandrino_link.Placement * FlangiaCuscinettoAlberoMandrino#LCS_FlangiaCuscinettoMandrino.Placement * AttachmentOffset * CuscinettoSfere30x52x12#LCS_Cuscinetto30x52x12.Placement ^ -1
FEATURE [App::Link] Profilo_C_basamento_link  label="Profilo_C_basamento-link"
  AttachedBy = #LCS_ProfiloCbasamento
  AttachedTo = Parent Assembly#LCS_Origin
  LinkedObject = -> <external ../Profilo-C-basamento.FCStd>#Body
  SolverId = Asm4EE
  expr: Placement = LCS_Origin.Placement * AttachmentOffset * Profilo_C_basamento#LCS_ProfiloCbasamento.Placement ^ -1
FEATURE [App::Link] Piatto40x10_link  label="Piatto40x10-link"
  AttachedBy = #LCS_Piatto40x10
  AttachedTo = Profilo_C_basamento_link#LCS_ProfiloCbasamento
  AttachmentOffset = pos=(82,45,250) rot=(0,0,1;1.5708rad)
  LinkPlacement = pos=(82,45,250) rot=(0,0,1;1.5708rad)
  LinkedObject = -> <external ../Piatto40x10x850.FCStd>#Body
  Placement = pos=(82,45,250) rot=(0,0,1;1.5708rad)
  SolverId = Asm4EE
  expr: Placement = Profilo_C_basamento_link.Placement * Profilo_C_basamento#LCS_ProfiloCbasamento.Placement * AttachmentOffset * Piatto40x10x850#LCS_Piatto40x10.Placement ^ -1
FEATURE [App::Link] Piatto40x10_link_2  label="Piatto40x10-link-2"
  AttachedBy = #LCS_Piatto40x10
  AttachedTo = Piatto40x10_link#LCS_Piatto40x10
  AttachmentOffset = pos=(10,0,0) rot=(0,0,1;0rad)
  LinkPlacement = pos=(82,55,250) rot=(0,0,1;1.5708rad)
  LinkedObject = -> <external ../Piatto40x10x850.FCStd>#Body
  Placement = pos=(82,55,250) rot=(0,0,1;1.5708rad)
  SolverId = Asm4EE
  expr: Placement = Piatto40x10_link.Placement * Piatto40x10x850#LCS_Piatto40x10.Placement * AttachmentOffset * Piatto40x10x850#LCS_Piatto40x10.Placement ^ -1
FEATURE [App::Link] GuidaQuadra_20x800_link  label="GuidaQuadra_20x800-link"
  AttachedBy = #LCS_GuidaQuadrata_20x800
  AttachedTo = Piatto40x10_link_2#LCS_Piatto40x10
  AttachmentOffset = pos=(0,0,25) rot=(0,0,1;3.14159rad)
  LinkPlacement = pos=(82,55,275) rot=(0,0,1;4.71239rad)
  LinkedObject = -> <external ../Guida-quadra-20-800.FCStd>#Body
  Placement = pos=(82,55,275) rot=(0,0,1;4.71239rad)
  SolverId = Asm4EE
  expr: Placement = Piatto40x10_link_2.Placement * Piatto40x10x850#LCS_Piatto40x10.Placement * AttachmentOffset * Guida_quadra_20_800#LCS_GuidaQuadrata_20x800.Placement ^ -1
FEATURE [App::Link] Profilo_C_basamento_2_link  label="Profilo_C_basamento-2-link"
  AttachedBy = #LCS_ProfiloCbasamento
  AttachedTo = Profilo_C_basamento_link#LCS_ProfiloCbasamento
  AttachmentOffset = pos=(80,-80,0) rot=(0,0,1;3.14159rad)
  LinkPlacement = pos=(80,-80,0) rot=(0,0,1;3.14159rad)
  LinkedObject = -> <external ../Profilo-C-basamento.FCStd>#Body
  Placement = pos=(80,-80,0) rot=(0,0,1;3.14159rad)
  SolverId = Asm4EE
  expr: Placement = Profilo_C_basamento_link.Placement * Profilo_C_basamento#LCS_ProfiloCbasamento.Placement * AttachmentOffset * Profilo_C_basamento#LCS_ProfiloCbasamento.Placement ^ -1
FEATURE [App::Link] Piatto40x10_2_link  label="Piatto40x10-2-link"
  AttachedBy = #LCS_Piatto40x10
  AttachedTo = Profilo_C_basamento_2_link#LCS_ProfiloCbasamento
  AttachmentOffset = pos=(38,45,250) rot=(0,0,1;1.5708rad)
  LinkPlacement = pos=(42,-125,250) rot=(0,0,1;4.71239rad)
  LinkedObject = -> <external ../Piatto40x10x850.FCStd>#Body
  Placement = pos=(42,-125,250) rot=(0,0,1;4.71239rad)
  SolverId = Asm4EE
  expr: Placement = Profilo_C_basamento_2_link.Placement * Profilo_C_basamento#LCS_ProfiloCbasamento.Placement * AttachmentOffset * Piatto40x10x850#LCS_Piatto40x10.Placement ^ -1
FEATURE [App::Link] Piatto40x10_3_link  label="Piatto40x10-3-link"
  AttachedBy = #LCS_Piatto40x10
  AttachedTo = Piatto40x10_2_link#LCS_Piatto40x10
  AttachmentOffset = pos=(10,0,0) rot=(0,0,1;0rad)
  LinkPlacement = pos=(42,-135,250) rot=(0,0,1;4.71239rad)
  LinkedObject = -> <external ../Piatto40x10x850.FCStd>#Body
  Placement = pos=(42,-135,250) rot=(0,0,1;4.71239rad)
  SolverId = Asm4EE
  expr: Placement = Piatto40x10_2_link.Placement * Piatto40x10x850#LCS_Piatto40x10.Placement * AttachmentOffset * Piatto40x10x850#LCS_Piatto40x10.Placement ^ -1
FEATURE [App::Link] GuidaQuadra_20x800_2_link  label="GuidaQuadra_20x800-2-link"
  AttachedBy = #LCS_GuidaQuadrata_20x800
  AttachedTo = Piatto40x10_3_link#LCS_Piatto40x10
  AttachmentOffset = pos=(0,40,25) rot=(0,0,1;0rad)
  LinkPlacement = pos=(82,-135,275) rot=(0,0,1;4.71239rad)
  LinkedObject = -> <external ../Guida-quadra-20-800.FCStd>#Body
  Placement = pos=(82,-135,275) rot=(0,0,1;4.71239rad)
  SolverId = Asm4EE
  expr: Placement = Piatto40x10_3_link.Placement * Piatto40x10x850#LCS_Piatto40x10.Placement * AttachmentOffset * Guida_quadra_20_800#LCS_GuidaQuadrata_20x800.Placement ^ -1
FEATURE [App::Link] Puleggia70_link  label="Puleggia70-link"
  AttachedBy = #LCS_Puleggia70
  AttachedTo = Motore_P60_Sanyo_link#LCS_Motore_sanyoP60
  AttachmentOffset = pos=(0,162,0) rot=(0.57735,0.57735,0.57735;2.0944rad)
  LinkPlacement = pos=(-6.53e-14,-40,187) rot=(0.57735,0.57735,0.57735;4.18879rad)
  LinkedObject = -> <external ../Puleggia70-Foro28.FCStd>#Body
  Placement = pos=(-6.53e-14,-40,187) rot=(0.57735,0.57735,0.57735;4.18879rad)
  SolverId = Asm4EE
  expr: Placement = Motore_P60_Sanyo_link.Placement * Motore_P60B13150HXS00M__SANYO#LCS_Motore_sanyoP60.Placement * AttachmentOffset * Puleggia70_Foro28#LCS_Puleggia70.Placement ^ -1
FEATURE [App::Link] FlangiaMandrino_link  label="FlangiaMandrino-link"
  AttachedBy = #LCS_FllangiaSupportoMandrino
  AttachedTo = AlberoMandrino30_link#LCS_AlberoMandrino
  AttachmentOffset = pos=(0,0,30) rot=(0,1,0;1.5708rad)
  LinkPlacement = pos=(190,-40,235) rot=(-0.57735,0.57735,-0.57735;4.18879rad)
  LinkedObject = -> <external ../BloccoMandrino/Flagia-Mandrino.FCStd>#Body
  Placement = pos=(190,-40,235) rot=(-0.57735,0.57735,-0.57735;4.18879rad)
  SolverId = Asm4EE
  expr: Placement = AlberoMandrino30_link.Placement * Albero_Mandrino30#LCS_AlberoMandrino.Placement * AttachmentOffset * Flagia_Mandrino#LCS_FllangiaSupportoMandrino.Placement ^ -1
FEATURE [App::Link] AlberoMandrino30_link  label="AlberoMandrino30-link"
  AttachedBy = #LCS_AlberoMandrino
  AttachedTo = FlangiaSupportoMandrino1_link#LCS_
  AttachmentOffset = pos=(75,-35,110) rot=(1,0,0;4.71239rad)
  LinkPlacement = pos=(190,-40,265) rot=(-0.707107,0.707107,0;3.14159rad)
  LinkedObject = -> <external ../BloccoMandrino/Albero-Mandrino30.FCStd>#Body
  Placement = pos=(190,-40,265) rot=(-0.707107,0.707107,0;3.14159rad)
  SolverId = Asm4EE
  expr: Placement = FlangiaSupportoMandrino1_link.Placement * FlangiaSupportoMandrino#LCS_.Placement * AttachmentOffset * Albero_Mandrino30#LCS_AlberoMandrino.Placement ^ -1
FEATURE [App::Link] Puleggia70Din28_link  label="Puleggia70Din28-link"
  AttachedBy = #LCS_Puleggia70
  AttachedTo = AlberoMandrino30_link#LCS_AlberoMandrino
  AttachmentOffset = pos=(0,0,78) rot=(-0.57735,-0.57735,0.57735;4.18879rad)
  LinkPlacement = pos=(190,-40,187) rot=(0.707107,0,0.707107;3.14159rad)
  LinkedObject = -> <external ../Puleggia70-Foro28.FCStd>#Body
  Placement = pos=(190,-40,187) rot=(0.707107,0,0.707107;3.14159rad)
  SolverId = Asm4EE
  expr: Placement = AlberoMandrino30_link.Placement * Albero_Mandrino30#LCS_AlberoMandrino.Placement * AttachmentOffset * Puleggia70_Foro28#LCS_Puleggia70.Placement ^ -1
FEATURE [App::Link] Mandrino_link  label="Mandrino-link"
  AttachedBy = #LCS_Mandrino
  AttachedTo = FlangiaMandrino_link#LCS_FllangiaSupportoMandrino
  AttachmentOffset = pos=(25,0,0) rot=(0.707107,0,0.707107;3.14159rad)
  LinkPlacement = pos=(190,-40,260) rot=(0,0,-1;1.5708rad)
  LinkedObject = -> <external ../BloccoMandrino/Mandrino.FCStd>#Body
  Placement = pos=(190,-40,260) rot=(0,0,-1;1.5708rad)
  SolverId = Asm4EE
  expr: Placement = FlangiaMandrino_link.Placement * Flagia_Mandrino#LCS_FllangiaSupportoMandrino.Placement * AttachmentOffset * Mandrino#LCS_Mandrino.Placement ^ -1
FEATURE [App::Link] DistanzialeBasamentoC_link  label="DistanzialeBasamentoC-link"
  AttachedBy = #LCS_DistanzialeBasamentoC
  AttachedTo = Profilo_C_basamento_link#LCS_ProfiloCbasamento
  AttachmentOffset = pos=(59,39,1100) rot=(0,-0.707107,0.707107;3.14159rad)
  LinkPlacement = pos=(59,39,1100) rot=(0,-0.707107,0.707107;3.14159rad)
  LinkedObject = -> <external ../DistanzialeBasamentoC.FCStd>#Body
  Placement = pos=(59,39,1100) rot=(0,-0.707107,0.707107;3.14159rad)
  SolverId = Asm4EE
  expr: Placement = Profilo_C_basamento_link.Placement * Profilo_C_basamento#LCS_ProfiloCbasamento.Placement * AttachmentOffset * DistanzialeBasamentoC#LCS_DistanzialeBasamentoC.Placement ^ -1
FEATURE [App::Link] Cremagliera_800_link  label="Cremagliera-800-link"
  AttachedBy = #LCS_Cremagliera_800
  AttachedTo = Piatto40x10_link_2#LCS_Piatto40x10
  AttachmentOffset = pos=(10,11,80) rot=(0.57735,0.57735,0.57735;2.0944rad)
  LinkPlacement = pos=(71,65,330) rot=(0,0.707107,0.707107;3.14159rad)
  LinkedObject = -> <external ../Cremagliera-M1.FCStd>#Part
  Placement = pos=(71,65,330) rot=(0,0.707107,0.707107;3.14159rad)
  SolverId = Asm4EE
  expr: Placement = Piatto40x10_link_2.Placement * Piatto40x10x850#LCS_Piatto40x10.Placement * AttachmentOffset * Cremagliera_M1#LCS_Cremagliera_800.Placement ^ -1
FEATURE [App::Link] Pignone_13M1_link  label="Pignone-13M1-link"
  AttachedBy = #LCS_Pignone13M1
  AttachedTo = PiastraVolantinoAvanzamentoCarro_link#LCS_PiastraAvanzamentoUtensile
  AttachmentOffset = pos=(23,21,61) rot=(0,1,0;3.14159rad)
  LinkPlacement = pos=(67,66,335) rot=(0.57735,0.57735,0.57735;4.18879rad)
  LinkedObject = -> <external ../Pignone13-M1.FCStd>#Part
  Placement = pos=(67,66,335) rot=(0.57735,0.57735,0.57735;4.18879rad)
  SolverId = Asm4EE
  expr: Placement = PiastraVolantinoAvanzamentoCarro_link.Placement * PiastraAvanzamentoCarro#LCS_PiastraAvanzamentoUtensile.Placement * AttachmentOffset * Pignone13_M1#LCS_Pignone13M1.Placement ^ -1
FEATURE [App::Link] PiastraVolantinoAvanzamentoUtensile_link  label="PiastraVolantinoAvanzamentoUtensile-link"
  AttachedBy = #LCS_PiastraAvanzamentoViteUtensile
  AttachedTo = ViteTrapezioT10_link#LCS_ViteTrapezioT10
  AttachmentOffset = pos=(0,7,22) rot=(1,0,0;3.14159rad)
  LinkPlacement = pos=(141,157,358) rot=(0.57735,0.57735,0.57735;4.18879rad)
  LinkedObject = -> <external ../TORRETTA/PiastraAvanzamentoUtensile.FCStd>#Body
  Placement = pos=(141,157,358) rot=(0.57735,0.57735,0.57735;4.18879rad)
  SolverId = Asm4EE
  expr: Placement = ViteTrapezioT10_link.Placement * ViteTrapezioT10#LCS_ViteTrapezioT10.Placement * AttachmentOffset * PiastraAvanzamentoUtensile#LCS_PiastraAvanzamentoViteUtensile.Placement ^ -1
FEATURE [App::Link] PiastraVolantinoAvanzamentoUtensilePosteriore_link  label="PiastraVolantinoAvanzamentoUtensilePosteriore-link"
  AttachedBy = #LCS_PiastraAvanzamentoViteUtensile
  AttachedTo = ViteTrapezioT10_link#LCS_ViteTrapezioT10
  AttachmentOffset = pos=(0,7,372) rot=(0,0,1;3.14159rad)
  LinkPlacement = pos=(141,-193,358) rot=(-0.57735,-0.57735,0.57735;4.18879rad)
  LinkedObject = -> <external ../TORRETTA/PiastraAvanzamentoUtensile.FCStd>#Body
  Placement = pos=(141,-193,358) rot=(-0.57735,-0.57735,0.57735;4.18879rad)
  SolverId = Asm4EE
  expr: Placement = ViteTrapezioT10_link.Placement * ViteTrapezioT10#LCS_ViteTrapezioT10.Placement * AttachmentOffset * PiastraAvanzamentoUtensile#LCS_PiastraAvanzamentoViteUtensile.Placement ^ -1
FEATURE [App::Link] PiastraVolantinoAvanzamentoCarro_link  label="PiastraVolantinoAvanzamentoCarro-link"
  AttachedBy = #LCS_PiastraAvanzamentoUtensile
  AttachedTo = PiastraCarro_link#LCS_PiastraCarro
  AttachmentOffset = pos=(-100,0,65) rot=(0.57735,-0.57735,0.57735;4.18879rad)
  LinkPlacement = pos=(46,127,358) rot=(0.57735,0.57735,-0.57735;2.0944rad)
  LinkedObject = -> <external ../PiastraAvanzamentoCarro.FCStd>#Body
  Placement = pos=(46,127,358) rot=(0.57735,0.57735,-0.57735;2.0944rad)
  SolverId = Asm4EE
  expr: Placement = PiastraCarro_link.Placement * PiastraCarroUtensile#LCS_PiastraCarro.Placement * AttachmentOffset * PiastraAvanzamentoCarro#LCS_PiastraAvanzamentoUtensile.Placement ^ -1
FEATURE [App::Link] Assembly_SgancioViteCarro_link  label="Assembly_SgancioViteCarro-link"
  AttachedBy = #LCS_Origin
  AttachedTo = PiastraVolantinoAvanzamentoCarro_link#LCS_PiastraAvanzamentoUtensile
  AttachmentOffset = pos=(-56,-55,10) rot=(0,0,1;0rad)
  LinkPlacement = pos=(-9,117,414) rot=(0.57735,0.57735,-0.57735;2.0944rad)
  LinkedObject = -> <external ../Assembly-SgancioViteCarro.FCStd>#Assembly
  Placement = pos=(-9,117,414) rot=(0.57735,0.57735,-0.57735;2.0944rad)
  SolverId = Asm4EE
  expr: Placement = PiastraVolantinoAvanzamentoCarro_link.Placement * PiastraAvanzamentoCarro#LCS_PiastraAvanzamentoUtensile.Placement * AttachmentOffset * Assembly_SgancioViteCarro#LCS_Origin.Placement ^ -1
FEATURE [Part::FeaturePython] DistPoints  # WARN: FeaturePython — macro-defined, semantics opaque (R4)
FEATURE [App::AnnotationLabel] MeasureLbl
  BasePosition = (97,-145,908)
  LabelText = D = 30,00 mm
  TextPosition = (0,0,0)
FEATURE [Part::FeaturePython] DistPoints001  # WARN: FeaturePython — macro-defined, semantics opaque (R4)
FEATURE [App::AnnotationLabel] MeasureLbl001
  BasePosition = (97,-145,908)
  LabelText = D = 30,00 mm
  TextPosition = (0,0,0)
FEATURE [Part::FeaturePython] DistPoints002  # WARN: FeaturePython — macro-defined, semantics opaque (R4)
FEATURE [App::AnnotationLabel] MeasureLbl002
  BasePosition = (96.5,-145,293)
  LabelText = D = 29,00 mm
  TextPosition = (0,0,0)
FEATURE [App::Link] Ingranaggio35_link  label="Ingranaggio35-link"
  AttachedBy = #LCS_1_Ingranaggio35
  AttachedTo = AlberoMandrino30_link#LCS_AlberoMandrino
  AttachmentOffset = pos=(0,0,55) rot=(0,0,1;0rad)
  LinkPlacement = pos=(190,-40,210) rot=(-0.707107,0.707107,0;3.14159rad)
  LinkedObject = -> <external ../BloccoMandrino/IngranaggioM35.FCStd>#Body
  Placement = pos=(190,-40,210) rot=(-0.707107,0.707107,0;3.14159rad)
  SolverId = Asm4EE
  expr: Placement = AlberoMandrino30_link.Placement * Albero_Mandrino30#LCS_AlberoMandrino.Placement * AttachmentOffset * IngranaggioM35#LCS_1_Ingranaggio35.Placement ^ -1
FEATURE [App::Part] Assembly
  AssemblyType = Part::Link
  Group = -> [LCS_Origin,Constraints,Configurations,Pattino20_2_link,Pattino20_4_link,PiastraCarro_link,FlangiaSupportoMandrino1_link,FlangiaSupportoMandrino2_link,ViteCarro16x4_link,SuppotoSingoloVite16x4_link,Chiocciola16x4_link,StaffaChiocciola16x4,SupportoDoppioVite16x4,Piedino40x40_link,Piedino40x40_1_link,Piedino40x40_2_link,Piedino40x40_3_link,Pattino_0_contropunta_link,Pattino_1_contropunta_link,+41 more]
  Origin = -> Origin
  Type = Assembly
FEATURE [Part::FeaturePython] DistPoints003  # WARN: FeaturePython — macro-defined, semantics opaque (R4)
FEATURE [App::AnnotationLabel] MeasureLbl003
  BasePosition = (72.5,55,290)
  LabelText = D = 25,00 mm
  TextPosition = (0,0,0)
FEATURE [App::DocumentObjectGroup] Measures
  Group = -> [DistPoints,MeasureLbl,DistPoints001,MeasureLbl001,DistPoints002,MeasureLbl002,DistPoints003,MeasureLbl003]

RESOLVED EXTERNAL PARTS (link-assembly join: the EXTERNAL_REF files above that resolve inside this repo's crawl, each included once):
---- part ../Assembly-SgancioViteCarro.FCStd = doc fcstd_8bcb4f4af678 ----
FCSTD DOCUMENT  (FreeCAD 0.21R33771 (Git))
Label: Assembly-SgancioViteCarro
License: All rights reserved
LicenseURL: http://en.wikipedia.org/wiki/All_rights_reserved
objects: App::DocumentObjectGroup×4, App::Link×4, PartDesign::CoordinateSystem×1, App::FeaturePython×1, App::Part×1, Part::FeaturePython×1, App::AnnotationLabel×1
note: 2 computed .brp shape members not serialized (recipe doc carries the construction recipe); baked Part::Feature solids carry a one-line shape summary decoded from their .brp
EXTERNAL_REF file=ChiocciolaMezzoSupporto.FCStd obj=LCS_HlafNut
EXTERNAL_REF file=FangiaHalfNut.FCStd obj=LCS_FlangiaHalfNut
EXTERNAL_REF file=ChiocciolaMezzoSupporto.FCStd obj=Body
EXTERNAL_REF file=FangiaHalfNut.FCStd obj=Body
EXTERNAL_REF file=CammaRotazioneHalfNut-160.FCStd obj=LCS_CammaHalfNut
EXTERNAL_REF file=CammaRotazioneHalfNut-160.FCStd obj=Body

FEATURE [App::DocumentObjectGroup] Parts
FEATURE [PartDesign::CoordinateSystem] LCS_Origin
  AttacherType = Attacher::AttachEngine3D
  MapMode = 2
  Support = -> [X_Axis]
FEATURE [App::DocumentObjectGroup] Constraints
FEATURE [App::FeaturePython] Variables  # WARN: FeaturePython — macro-defined, semantics opaque (R4)
  Type = App::PropertyContainer
FEATURE [App::DocumentObjectGroup] Configurations
FEATURE [App::Link] ChiocciolaMezzoSupporto_link  label="ChiocciolaMezzoSupporto-link"
  AttachedBy = #LCS_HlafNut
  AttachedTo = FlangiaHalfNut_link#LCS_FlangiaHalfNut
  AttachmentOffset = pos=(44,45,27) rot=(0,1,0;4.71239rad)
  LinkPlacement = pos=(44,45,27) rot=(0,1,0;4.71239rad)
  LinkedObject = -> <external ChiocciolaMezzoSupporto.FCStd>#Body
  Placement = pos=(44,45,27) rot=(0,1,0;4.71239rad)
  SolverId = Asm4EE
  expr: Placement = FlangiaHalfNut_link.Placement * FangiaHalfNut#LCS_FlangiaHalfNut.Placement * AttachmentOffset * ChiocciolaMezzoSupporto#LCS_HlafNut.Placement ^ -1
FEATURE [App::Link] ChiocciolaMezzoSupporto_2_link  label="ChiocciolaMezzoSupporto-2-link"
  AttachedBy = #LCS_HlafNut
  AttachedTo = ChiocciolaMezzoSupporto_link#LCS_HlafNut
  AttachmentOffset = pos=(0,0,28) rot=(1,0,0;3.14159rad)
  LinkPlacement = pos=(16,45,27) rot=(-0.707107,0,-0.707107;3.14159rad)
  LinkedObject = -> <external ChiocciolaMezzoSupporto.FCStd>#Body
  Placement = pos=(16,45,27) rot=(-0.707107,0,-0.707107;3.14159rad)
  SolverId = Asm4EE
  expr: Placement = ChiocciolaMezzoSupporto_link.Placement * ChiocciolaMezzoSupporto#LCS_HlafNut.Placement * AttachmentOffset * ChiocciolaMezzoSupporto#LCS_HlafNut.Placement ^ -1
FEATURE [App::Link] FlangiaHalfNut_link  label="FlangiaHalfNut-link"
  AttachedBy = #LCS_FlangiaHalfNut
  AttachedTo = Parent Assembly#LCS_Origin
  LinkedObject = -> <external FangiaHalfNut.FCStd>#Body
  SolverId = Asm4EE
  expr: Placement = LCS_Origin.Placement * AttachmentOffset * FangiaHalfNut#LCS_FlangiaHalfNut.Placement ^ -1
FEATURE [App::Link] CammaRotazioneHalfNut_160_link  label="CammaRotazioneHalfNut-160-link"
  AttachedBy = #LCS_CammaHalfNut
  AttachedTo = FlangiaHalfNut_link#LCS_FlangiaHalfNut
  AttachmentOffset = pos=(30,45,0) rot=(0,0,-1;4.71239rad)
  LinkPlacement = pos=(30,45,0) rot=(0,0,-1;4.71239rad)
  LinkedObject = -> <external CammaRotazioneHalfNut-160.FCStd>#Body
  Placement = pos=(30,45,0) rot=(0,0,-1;4.71239rad)
  SolverId = Asm4EE
  expr: Placement = FlangiaHalfNut_link.Placement * FangiaHalfNut#LCS_FlangiaHalfNut.Placement * AttachmentOffset * CammaRotazioneHalfNut_160#LCS_CammaHalfNut.Placement ^ -1
FEATURE [App::Part] Assembly
  AssemblyType = Part::Link
  Group = -> [LCS_Origin,Constraints,Variables,Configurations,ChiocciolaMezzoSupporto_link,ChiocciolaMezzoSupporto_2_link,FlangiaHalfNut_link,CammaRotazioneHalfNut_160_link]
  Origin = -> Origin
  Type = Assembly
FEATURE [Part::FeaturePython] DistPoints  # WARN: FeaturePython — macro-defined, semantics opaque (R4)
FEATURE [App::AnnotationLabel] MeasureLbl
  BasePosition = (0,45,0)
  LabelText = D = 90,00 mm
  TextPosition = (0,0,0)
FEATURE [App::DocumentObjectGroup] Measures
  Group = -> [DistPoints,MeasureLbl]
---- part ../BloccoMandrino/Albero-Mandrino30.FCStd = doc fcstd_750b8ebc45a7 ----
FCSTD DOCUMENT  (FreeCAD 0.21R33771 (Git))
Label: Albero-Mandrino30
License: All rights reserved
LicenseURL: http://en.wikipedia.org/wiki/All_rights_reserved
objects: Sketcher::SketchObject×2, Part::Helix×1, PartDesign::Pad×1, Part::Feature×1, PartDesign::CoordinateSystem×1, PartDesign::Pocket×1, PartDesign::Body×1
note: 10 computed .brp shape members not serialized (recipe doc carries the construction recipe); baked Part::Feature solids carry a one-line shape summary decoded from their .brp

FEATURE [Part::Helix] Helix  label="Elica"
  Angle = 0
  AttacherType = Attacher::AttachEngine3D
  Height = 15
  LocalCoord = 0
  Pitch = 1.5
  Placement = pos=(0,0,65.7628) rot=(0,0,1;0rad)
  Radius = 15
  SegmentLength = 0
  Style = 1
FEATURE [Sketcher::SketchObject] Sketch
  FullyConstrained = true
  MapMode = 5
  Support = -> [XY_Plane]
  sketch-geometry (2):
    g0: Circle CenterX=0 CenterY=0 CenterZ=0 NormalX=0 NormalY=0 NormalZ=1 AngleXU=0 Radius=15
    g1: Circle CenterX=0 CenterY=0 CenterZ=0 NormalX=0 NormalY=0 NormalZ=1 AngleXU=0 Radius=11
  constraints (4):
    c: Coincident(g0,g-1)
    c: Radius(g0) = 15
    c: Coincident(g1,g0)
    c: Radius(g1) = 11
FEATURE [Sketcher::SketchObject] Sketch001
  FullyConstrained = true
  MapMode = 5
  Placement = pos=(0,0,260) rot=(0,0,1;0rad)
  sketch-geometry (2):
    g0: Circle CenterX=0 CenterY=0 CenterZ=0 NormalX=0 NormalY=0 NormalZ=1 AngleXU=0 Radius=15
    g1: Circle CenterX=0 CenterY=0 CenterZ=0 NormalX=0 NormalY=0 NormalZ=1 AngleXU=0 Radius=14
  constraints (4):
    c: Coincident(g0,g-1)
    c: Coincident(g1,g0)
    c: Radius(g0) = 15
    c: Radius(g1) = 14
FEATURE [PartDesign::Pad] Pad
  Direction = (0,0,1)
  Length = 260
  Length2 = 10
  Profile = -> Sketch
  ReferenceAxis = -> Sketch [N_Axis]
  Type = 0
FEATURE [Part::Feature] Face
  Placement = pos=(-0.113336,0,0) rot=(0,0,1;0rad)
  shape: bbox 0.6439 x 2e-07 x 0.7643 mm, 1 faces, 0 solids (baked)
FEATURE [PartDesign::CoordinateSystem] LCS_AlberoMandrino
  AttacherType = Attacher::AttachEngine3D
FEATURE [PartDesign::Pocket] Pocket
  BaseFeature = -> Pad
  Direction = (0,0,-1)
  Length = 190
  Length2 = 5
  Profile = -> Sketch001
  ReferenceAxis = -> Sketch001 [N_Axis]
  Type = 0
FEATURE [PartDesign::Body] Body
  Group = -> [Sketch,Sketch001,Pad,LCS_AlberoMandrino,Pocket]
  Origin = -> Origin
  Tip = -> Pocket
---- part ../BloccoMandrino/CuscinettoSfere30x52x12.FCStd = doc fcstd_a628b2c13842 ----
FCSTD DOCUMENT  (FreeCAD 0.21R33771 (Git))
Label: CuscinettoSfere30x52x12
License: All rights reserved
LicenseURL: http://en.wikipedia.org/wiki/All_rights_reserved
objects: Sketcher::SketchObject×2, PartDesign::Pad×1, PartDesign::Pocket×1, PartDesign::CoordinateSystem×1, PartDesign::Body×1
note: 8 computed .brp shape members not serialized (recipe doc carries the construction recipe); baked Part::Feature solids carry a one-line shape summary decoded from their .brp

FEATURE [Sketcher::SketchObject] Sketch
  FullyConstrained = true
  MapMode = 5
  Support = -> [XY_Plane]
  sketch-geometry (2):
    g0: Circle CenterX=0 CenterY=0 CenterZ=0 NormalX=0 NormalY=0 NormalZ=1 AngleXU=0 Radius=15
    g1: Circle CenterX=0 CenterY=0 CenterZ=0 NormalX=0 NormalY=0 NormalZ=1 AngleXU=0 Radius=26
  constraints (4):
    c: Coincident(g0,g-1)
    c: Coincident(g1,g0)
    c: Radius(g0) = 15
    c: Radius(g1) = 26
FEATURE [PartDesign::Pad] Pad
  Direction = (1,1,1)
  Length = 12
  Length2 = 100
  Profile = -> Sketch
  Type = 0
FEATURE [Sketcher::SketchObject] Sketch001
  FullyConstrained = true
  MapMode = 5
  Placement = pos=(0,0,12) rot=(0,0,1;0rad)
  Support = -> [Pad]
  sketch-geometry (2):
    g0: Circle CenterX=0 CenterY=0 CenterZ=0 NormalX=0 NormalY=0 NormalZ=1 AngleXU=0 Radius=34
    g1: Circle CenterX=0 CenterY=0 CenterZ=0 NormalX=0 NormalY=0 NormalZ=1 AngleXU=0 Radius=48
  constraints (4):
    c: Coincident(g0,g-1)
    c: Coincident(g1,g0)
    c: Radius(g1) = 48
    c: Radius(g0) = 34
FEATURE [PartDesign::Pocket] Pocket
  BaseFeature = -> Pad
  Direction = (1,1,1)
  Length = 5
  Length2 = 100
  Profile = -> Sketch001
  Type = 0
FEATURE [PartDesign::CoordinateSystem] LCS_Cuscinetto30x52x12
  AttacherType = Attacher::AttachEngine3D
FEATURE [PartDesign::Body] Body
  Group = -> [Sketch,Pad,Sketch001,Pocket,LCS_Cuscinetto30x52x12]
  Origin = -> Origin
  Tip = -> Pocket
---- part ../BloccoMandrino/Flagia-Mandrino.FCStd = doc fcstd_5d5e6ed03656 ----
FCSTD DOCUMENT  (FreeCAD 0.21R33771 (Git))
Label: Flagia-Mandrino
License: All rights reserved
LicenseURL: http://en.wikipedia.org/wiki/All_rights_reserved
objects: TechDraw::DrawViewDimension×12, TechDraw::DrawProjGroupItem×4, Sketcher::SketchObject×3, PartDesign::Pocket×2, PartDesign::Chamfer×2, PartDesign::Revolution×1, PartDesign::CoordinateSystem×1, PartDesign::Plane×1, PartDesign::Body×1, TechDraw::DrawSVGTemplate×1, TechDraw::DrawViewSection×1, TechDraw::DrawViewBalloon×1, TechDraw::DrawProjGroup×1, TechDraw::DrawPage×1
note: 33 computed .brp shape members not serialized (recipe doc carries the construction recipe); baked Part::Feature solids carry a one-line shape summary decoded from their .brp

FEATURE [Sketcher::SketchObject] Sketch
  FullyConstrained = true
  MapMode = 5
  Placement = pos=(0,0,0) rot=(1,0,0;1.5708rad)
  Support = -> [XZ_Plane]
  sketch-geometry (10):
    g0: LineSegment StartX=0 StartY=15 StartZ=0 EndX=0 EndY=17.5 EndZ=0
    g1: LineSegment StartX=0 StartY=17.5 StartZ=0 EndX=11 EndY=17.5 EndZ=0
    g2: LineSegment StartX=17 StartY=50 StartZ=0 EndX=24 EndY=50 EndZ=0
    g3: LineSegment StartX=24 StartY=50 StartZ=0 EndX=24 EndY=37 EndZ=0
    g4: LineSegment StartX=24 StartY=37 StartZ=0 EndX=30 EndY=37 EndZ=0
    g5: LineSegment StartX=30 StartY=37 StartZ=0 EndX=30 EndY=15 EndZ=0
    g6: LineSegment StartX=30 StartY=15 StartZ=0 EndX=0 EndY=15 EndZ=0
    g7: LineSegment StartX=17 StartY=50 StartZ=0 EndX=17 EndY=26 EndZ=0
    g8: LineSegment StartX=17 StartY=26 StartZ=0 EndX=11 EndY=26 EndZ=0
    g9: LineSegment StartX=11 StartY=26 StartZ=0 EndX=11 EndY=17.5 EndZ=0
  constraints (30):
    c: PointOnObject(g0,g-2)
    c: PointOnObject(g0,g-2)
    c: Coincident(g1,g0)
    c: Horizontal(g1)
    c: Horizontal(g2)
    c: Vertical(g3)
    c: Horizontal(g4)
    c: Coincident(g5,g4)
    c: Vertical(g5)
    c: Coincident(g6,g5)
    c: Coincident(g6,g0)
    c: Horizontal(g6)
    c: DistanceY(g-1,g0) = 15
    c: Coincident(g3,g2)
    c: Coincident(g3,g4)
    c: DistanceX(g6,g6) = 30
    c: DistanceY(g5,g5) = 22
    c: Coincident(g7,g2)
    c: Vertical(g7)
    c: Coincident(g8,g7)
    c: Horizontal(g8)
    c: Coincident(g9,g8)
    c: Coincident(g9,g1)
    c: Vertical(g9)
    c: DistanceY(g-1,g8) = 26
    c: DistanceX(g8,g8) = 6
    c: DistanceY(g-1,g0) = 17.5
    c: DistanceY(g-1,g2) = 50
    c: DistanceX(g4,g4) = 6
    c: DistanceX(g1,g1) = 11
FEATURE [PartDesign::Revolution] Revolution
  Angle = 360
  Axis = (1,0,0)
  Base = (0,0,0)
  Placement = pos=(0,0,0) rot=(1,0,0;1.5708rad)
  Profile = -> Sketch
  ReferenceAxis = -> X_Axis
FEATURE [Sketcher::SketchObject] Sketch001
  FullyConstrained = false
  MapMode = 5
  Placement = pos=(7,0,0) rot=(0.707107,0,-0.707107;3.14159rad)
  sketch-geometry (5):
    g0: Circle CenterX=0 CenterY=0 CenterZ=0 NormalX=0 NormalY=0 NormalZ=1 AngleXU=0 Radius=41.75
    g1: Circle CenterX=0 CenterY=41.75 CenterZ=0 NormalX=0 NormalY=0 NormalZ=1 AngleXU=0 Radius=4
    g2: Circle CenterX=35.9374 CenterY=-21.25 CenterZ=0 NormalX=0 NormalY=0 NormalZ=1 AngleXU=0 Radius=4
    g3: Circle CenterX=-35.9374 CenterY=-21.25 CenterZ=0 NormalX=0 NormalY=0 NormalZ=1 AngleXU=0 Radius=4
    g4: LineSegment StartX=-66.7657 StartY=-21.25 StartZ=0 EndX=72.4096 EndY=-21.25 EndZ=0
  constraints (13):
    c: Coincident(g0,g-1)
    c: PointOnObject(g1,g0)
    c: PointOnObject(g1,g-2)
    c: Radius(g0) = 41.75
    c: PointOnObject(g2,g0)
    c: PointOnObject(g3,g0)
    c: Horizontal(g4)
    c: PointOnObject(g3,g4)
    c: PointOnObject(g2,g4)
    c: DistanceY(g4,g0) = 21.25
    c: Equal(g1,g3)
    c: Equal(g1,g2)
    c: Radius(g1) = 4
FEATURE [PartDesign::CoordinateSystem] LCS_FllangiaSupportoMandrino  label="LCS_FlangiaSupportoMandrino"
  AttacherType = Attacher::AttachEngine3D
FEATURE [PartDesign::Pocket] Pocket
  BaseFeature = -> Revolution
  Direction = (1,0,2e-16)
  Length = 5
  Length2 = 5
  Placement = pos=(0,0,0) rot=(1,0,0;1.5708rad)
  Profile = -> Sketch001
  ReferenceAxis = -> Sketch001 [N_Axis]
  Type = 1
FEATURE [PartDesign::Chamfer] Chamfer
  Angle = 60
  Base = -> Pocket [Edge7,Edge5,Edge4]
  BaseFeature = -> Pocket
  ChamferType = 0
  FlipDirection = false
  Placement = pos=(0,0,0) rot=(1,0,0;1.5708rad)
  Size = 3.5
  Size2 = 1
  SupportTransform = false
  UseAllEdges = false
FEATURE [PartDesign::Chamfer] Chamfer001
  Angle = 45
  Base = -> Chamfer [Edge28]
  BaseFeature = -> Chamfer
  ChamferType = 0
  FlipDirection = false
  Placement = pos=(0,0,0) rot=(1,0,0;1.5708rad)
  Size = 4
  Size2 = 1
  SupportTransform = false
  UseAllEdges = false
FEATURE [PartDesign::Plane] DatumPlane
  AttachmentOffset = pos=(0,0,50) rot=(0,0,1;0rad)
  Length = 60
  MapMode = 2
  Placement = pos=(0,0,50) rot=(0,0,1;0rad)
  ResizeMode = 0
  Support = -> [XY_Plane]
  Width = 60
FEATURE [Sketcher::SketchObject] Sketch002
  FullyConstrained = true
  MapMode = 5
  Placement = pos=(0,0,50) rot=(0,0,1;0rad)
  Support = -> [DatumPlane]
  sketch-geometry (1):
    g0: Circle CenterX=14 CenterY=0 CenterZ=0 NormalX=0 NormalY=0 NormalZ=1 AngleXU=0 Radius=2.5
  constraints (3):
    c: PointOnObject(g0,g-1)
    c: Radius(g0) = 2.5
    c: DistanceX(g-1,g0) = 14
FEATURE [PartDesign::Pocket] Pocket001
  BaseFeature = -> Chamfer001
  Direction = (0,0,-1)
  Length = 5
  Length2 = 5
  Placement = pos=(0,0,0) rot=(1,0,0;1.5708rad)
  Profile = -> Sketch002
  ReferenceAxis = -> Sketch002 [N_Axis]
  Type = 1
FEATURE [PartDesign::Body] Body
  Group = -> [Sketch,Revolution,Sketch001,LCS_FllangiaSupportoMandrino,Pocket,Chamfer,Chamfer001,DatumPlane,Sketch002,Pocket001]
  Origin = -> Origin
  Tip = -> Pocket001
FEATURE [TechDraw::DrawSVGTemplate] Template
  EditableTexts = Designed_by_Name=Designed by Name; Drawing_number=Drawing number; FC-Date=Date; FC-SC=Scale; FC-SH=Sheet; FC-Title=Flangia Mandrino 03; Subtitle=Acciaio; Weight=Weight
  Height = 210
  Orientation = 1
  Template = <userpath>/Portable/FreeCAD_0.21.2-2023-12-17-conda-Windows-x86_64-py310/data/Mod/TechDraw/Templates/A4_LandscapeTD.svg
  Width = 297
FEATURE [TechDraw::DrawProjGroupItem] ProjItem  label="Front"
  CoarseView = false
  Direction = (-1,0,0)
  Focus = 100
  HardHidden = false
  IsoCount = 0
  IsoHidden = false
  IsoVisible = false
  LockPosition = true
  Perspective = false
  Rotation = 0
  RotationVector = (0,-1,0)
  Scale = 0.7
  ScaleType = 2
  ScrubCount = 0
  SeamHidden = false
  SeamVisible = false
  SmoothHidden = false
  SmoothVisible = true
  Source = -> [Body]
  Type = 0
  X = 0
  XDirection = (0,-1,0)
  Y = 0
FEATURE [TechDraw::DrawProjGroupItem] ProjItem001  label="Left"
  CoarseView = false
  Direction = (-1e-16,1,0)
  Focus = 100
  HardHidden = false
  IsoCount = 0
  IsoHidden = false
  IsoVisible = false
  LockPosition = true
  Perspective = false
  Rotation = 0
  RotationVector = (1,0,0)
  Scale = 0.7
  ScaleType = 2
  ScrubCount = 0
  SeamHidden = false
  SeamVisible = false
  SmoothHidden = false
  SmoothVisible = true
  Source = -> [Body]
  Type = 1
  X = 105.482
  XDirection = (-1,-1e-16,0)
  Y = 0
FEATURE [TechDraw::DrawViewDimension] Dimension001
  AngleOverride = false
  Arbitrary = false
  ArbitraryTolerances = false
  EqualTolerance = true
  ExtensionAngle = 0
  FormatSpec = ⌀%.2w
  FormatSpecOverTolerance = %+.2w
  FormatSpecUnderTolerance = %+.2w
  Inverted = false
  LineAngle = 0
  LockPosition = false
  MeasureType = 1
  OverTolerance = 0
  References2D = -> [ProjItem]
  Rotation = 0
  ScaleType = 0
  TheoreticalExact = false
  Type = 5
  UnderTolerance = 0
  X = 31.937
  Y = 42.9953
FEATURE [TechDraw::DrawViewDimension] Dimension002
  AngleOverride = false
  Arbitrary = false
  ArbitraryTolerances = false
  EqualTolerance = true
  ExtensionAngle = 0
  FormatSpec = ⌀%.2w
  FormatSpecOverTolerance = %+.2w
  FormatSpecUnderTolerance = %+.2w
  Inverted = false
  LineAngle = 0
  LockPosition = false
  MeasureType = 1
  OverTolerance = 0
  References2D = -> [ProjItem]
  Rotation = 0
  ScaleType = 0
  TheoreticalExact = false
  Type = 5
  UnderTolerance = 0
  X = 18.952
  Y = 44.838
FEATURE [TechDraw::DrawViewDimension] Dimension003
  AngleOverride = false
  Arbitrary = false
  ArbitraryTolerances = false
  EqualTolerance = false
  ExtensionAngle = 0
  FormatSpec = ⌀%.2w
  FormatSpecOverTolerance = %+.2w
  FormatSpecUnderTolerance = %+.2w
  Inverted = false
  LineAngle = 0
  LockPosition = false
  MeasureType = 1
  OverTolerance = 0
  References2D = -> [ProjItem]
  Rotation = 0
  ScaleType = 0
  TheoreticalExact = false
  Type = 5
  UnderTolerance = -0.1
  X = 46.7897
  Y = -27.0961
FEATURE [TechDraw::DrawViewDimension] Dimension004
  AngleOverride = false
  Arbitrary = false
  ArbitraryTolerances = false
  EqualTolerance = false
  ExtensionAngle = 0
  FormatSpec = ⌀%.2w
  FormatSpecOverTolerance = %+.2w
  FormatSpecUnderTolerance = %+.2w
  Inverted = false
  LineAngle = 0
  LockPosition = false
  MeasureType = 1
  OverTolerance = 0.1
  References2D = -> [ProjItem]
  Rotation = 0
  ScaleType = 0
  TheoreticalExact = false
  Type = 5
  UnderTolerance = 0
  X = 31.4493
  Y = -31.7766
FEATURE [TechDraw::DrawViewDimension] Dimension005
  AngleOverride = false
  Arbitrary = false
  ArbitraryTolerances = false
  EqualTolerance = true
  ExtensionAngle = 0
  FormatSpec = ⌀%.2w
  FormatSpecOverTolerance = %+.2w
  FormatSpecUnderTolerance = %+.2w
  Inverted = false
  LineAngle = 0
  LockPosition = false
  MeasureType = 1
  OverTolerance = 0
  References2D = -> [ProjItem]
  Rotation = 0
  ScaleType = 0
  TheoreticalExact = false
  Type = 5
  UnderTolerance = 0
  X = -36.1156
  Y = 38.0573
FEATURE [TechDraw::DrawViewDimension] Dimension006
  AngleOverride = false
  Arbitrary = false
  ArbitraryTolerances = false
  EqualTolerance = true
  ExtensionAngle = 0
  FormatSpec = %.2w
  FormatSpecOverTolerance = %+.2w
  FormatSpecUnderTolerance = %+.2w
  Inverted = false
  LineAngle = 0
  LockPosition = false
  MeasureType = 1
  OverTolerance = 0
  References2D = -> [ProjItem001]
  Rotation = 0
  ScaleType = 0
  TheoreticalExact = false
  Type = 1
  UnderTolerance = 0
  X = -33.9986
  Y = 45.2214
FEATURE [TechDraw::DrawViewDimension] Dimension007
  AngleOverride = false
  Arbitrary = false
  ArbitraryTolerances = false
  EqualTolerance = true
  ExtensionAngle = 0
  FormatSpec = %.2w
  FormatSpecOverTolerance = %+.2w
  FormatSpecUnderTolerance = %+.2w
  Inverted = false
  LineAngle = 0
  LockPosition = false
  MeasureType = 1
  OverTolerance = 0
  References2D = -> [ProjItem001]
  Rotation = 0
  ScaleType = 0
  TheoreticalExact = false
  Type = 1
  UnderTolerance = 0
  X = -25.5633
  Y = 51.0968
FEATURE [TechDraw::DrawViewDimension] Dimension008
  AngleOverride = false
  Arbitrary = false
  ArbitraryTolerances = false
  EqualTolerance = true
  ExtensionAngle = 0
  FormatSpec = %.2w
  FormatSpecOverTolerance = %+.2w
  FormatSpecUnderTolerance = %+.2w
  Inverted = false
  LineAngle = 0
  LockPosition = false
  MeasureType = 1
  OverTolerance = 0
  References2D = -> [ProjItem001]
  Rotation = 0
  ScaleType = 0
  TheoreticalExact = false
  Type = 1
  UnderTolerance = 0
  X = -1.1633
  Y = 68.6411
FEATURE [TechDraw::DrawViewDimension] Dimension009
  AngleOverride = false
  Arbitrary = false
  ArbitraryTolerances = false
  EqualTolerance = true
  ExtensionAngle = 0
  FormatSpec = %.2w
  FormatSpecOverTolerance = %+.2w
  FormatSpecUnderTolerance = %+.2w
  Inverted = false
  LineAngle = 0
  LockPosition = false
  MeasureType = 1
  OverTolerance = 0
  References2D = -> [ProjItem001]
  Rotation = 0
  ScaleType = 0
  TheoreticalExact = false
  Type = 1
  UnderTolerance = 0
  X = -20.5242
  Y = 61.0005
FEATURE [TechDraw::DrawViewSection] SectionView  label="Section A - A"
  BaseView = -> ProjItem
  CoarseView = false
  CutSurfaceDisplay = 2
  Direction = (0,-1e-16,-1)
  FileGeomPattern = <userpath>/Portable/FreeCAD_0.21.2-2023-12-17-conda-Windows-x86_64-py310/data/Mod/TechDraw/PAT/FCPAT.pat
  FileHatchPattern = <userpath>/Portable/FreeCAD_0.21.2-2023-12-17-conda-Windows-x86_64-py310/data/Mod/TechDraw/Patterns/simple.svg
  Focus = 100
  FuseBeforeCut = false
  HardHidden = false
  HatchOffset = (0,0,0)
  HatchRotation = 0
  HatchScale = 1
  IsoCount = 0
  IsoHidden = false
  IsoVisible = false
  LockPosition = true
  NameGeomPattern = Diamond
  Perspective = false
  Rotation = 0
  Scale = 0.7
  ScaleType = 2
  ScrubCount = 0
  SeamHidden = false
  SeamVisible = false
  SectionDirection = 4
  SectionNormal = (0,-1e-16,-1)
  SectionOrigin = (15,0,0)
  SectionSymbol = A
  SmoothHidden = false
  SmoothVisible = true
  Source = -> [Body]
  TrimAfterCut = false
  X = 70.37
  XDirection = (0,-1,1e-16)
  Y = 38.4134
FEATURE [TechDraw::DrawProjGroupItem] ProjItem004  label="Bottom"
  CoarseView = false
  Direction = (0,0,-1)
  Focus = 100
  HardHidden = false
  IsoCount = 0
  IsoHidden = false
  IsoVisible = false
  LockPosition = true
  Perspective = false
  Rotation = 0
  RotationVector = (1,0,0)
  ScaleType = 2
  ScrubCount = 0
  SeamHidden = false
  SeamVisible = false
  SmoothHidden = false
  SmoothVisible = true
  Source = -> [Body]
  Type = 5
  X = 0
  XDirection = (0,-1,0)
  Y = 73.8285
FEATURE [TechDraw::DrawViewDimension] Dimension012
  AngleOverride = false
  Arbitrary = false
  ArbitraryTolerances = false
  EqualTolerance = false
  ExtensionAngle = 0
  FormatSpec = ⌀%.2w
  FormatSpecOverTolerance = %+.2w
  FormatSpecUnderTolerance = %+.2w
  Inverted = false
  LineAngle = 0
  LockPosition = false
  MeasureType = 1
  OverTolerance = 0
  References2D = -> [ProjItem001]
  Rotation = 0
  ScaleType = 0
  TheoreticalExact = false
  Type = 2
  UnderTolerance = -0.05
  X = -32.1831
  Y = 3.24561
FEATURE [TechDraw::DrawViewDimension] Dimension014
  AngleOverride = false
  Arbitrary = false
  ArbitraryTolerances = false
  EqualTolerance = true
  ExtensionAngle = 0
  FormatSpec = ⌀%.2w
  FormatSpecOverTolerance = %+.2w
  FormatSpecUnderTolerance = %+.2w
  Inverted = false
  LineAngle = 0
  LockPosition = false
  MeasureType = 1
  OverTolerance = 0
  References2D = -> [ProjItem]
  Rotation = 0
  ScaleType = 0
  TheoreticalExact = false
  Type = 5
  UnderTolerance = 0
  X = -36.179
  Y = 26.3555
FEATURE [TechDraw::DrawViewBalloon] Balloon
  BubbleShape = 0
  EndType = 0
  EndTypeScale = 1
  KinkLength = 5
  LockPosition = false
  OriginX = -2.5
  OriginY = 1
  Rotation = 0
  ScaleType = 0
  ShapeScale = 1
  SourceView = -> ProjItem004
  Text = Filetto M5
  TextWrapLen = -1
  X = 83.0656
  Y = -4.90236
FEATURE [TechDraw::DrawProjGroupItem] ProjItem005  label="FrontBottomRight"
  CoarseView = false
  Direction = (-0.57735,-0.57735,-0.57735)
  Focus = 100
  HardHidden = false
  IsoCount = 0
  IsoHidden = false
  IsoVisible = false
  LockPosition = true
  Perspective = false
  Rotation = 0
  RotationVector = (1,0,0)
  ScaleType = 2
  ScrubCount = 0
  SeamHidden = false
  SeamVisible = false
  SmoothHidden = false
  SmoothVisible = true
  Source = -> [Body]
  Type = 9
  X = 181.142
  XDirection = (0.707107,-0.707107,0)
  Y = 51.4949
FEATURE [TechDraw::DrawProjGroup] ProjGroup
  Anchor = -> ProjItem
  AutoDistribute = true
  LockPosition = false
  ProjectionType = 0
  Rotation = 0
  Scale = 0.7
  ScaleType = 2
  Source = -> [Body]
  Views = -> [ProjItem,ProjItem001,ProjItem004,ProjItem005]
  X = 70.6048
  Y = 106.728
  spacingX = 15
  spacingY = 15
FEATURE [TechDraw::DrawViewDimension] Dimension015
  AngleOverride = false
  Arbitrary = true
  ArbitraryTolerances = false
  EqualTolerance = true
  ExtensionAngle = 0
  FormatSpec = ⌀83,5
  FormatSpecOverTolerance = %+.2w
  FormatSpecUnderTolerance = %+.2w
  Inverted = false
  LineAngle = 0
  LockPosition = false
  MeasureType = 1
  OverTolerance = 0
  References2D = -> [ProjItem]
  Rotation = 0
  ScaleType = 0
  TheoreticalExact = false
  Type = 5
  UnderTolerance = 0
  X = 43.6041
  Y = 32.2197
FEATURE [TechDraw::DrawPage] Page
  KeepUpdated = true
  NextBalloonIndex = 2
  ProjectionType = 0
  Template = -> Template
  Views = -> [ProjGroup,Dimension001,Dimension002,Dimension003,Dimension004,Dimension005,Dimension006,Dimension007,Dimension008,Dimension009,SectionView,Dimension012,Dimension014,Balloon,Dimension015]
---- part ../BloccoMandrino/FlangiaCuscinettoAlberoMandrino.FCStd = doc fcstd_be11426dbcd9 ----
FCSTD DOCUMENT  (FreeCAD 0.21R33771 (Git))
Label: FlangiaCuscinettoAlberoMandrino
License: All rights reserved
LicenseURL: http://en.wikipedia.org/wiki/All_rights_reserved
objects: Sketcher::SketchObject×3, PartDesign::Pocket×2, PartDesign::CoordinateSystem×1, PartDesign::Pad×1, PartDesign::Body×1
note: 11 computed .brp shape members not serialized (recipe doc carries the construction recipe); baked Part::Feature solids carry a one-line shape summary decoded from their .brp

FEATURE [Sketcher::SketchObject] Sketch
  FullyConstrained = true
  MapMode = 5
  Support = -> [XY_Plane]
  sketch-geometry (4):
    g0: LineSegment StartX=-35 StartY=35 StartZ=0 EndX=35 EndY=35 EndZ=0
    g1: LineSegment StartX=35 StartY=35 StartZ=0 EndX=35 EndY=-35 EndZ=0
    g2: LineSegment StartX=35 StartY=-35 StartZ=0 EndX=-35 EndY=-35 EndZ=0
    g3: LineSegment StartX=-35 StartY=-35 StartZ=0 EndX=-35 EndY=35 EndZ=0
  constraints (12):
    c: Coincident(g0,g1)
    c: Coincident(g1,g2)
    c: Coincident(g2,g3)
    c: Coincident(g3,g0)
    c: Horizontal(g0)
    c: Horizontal(g2)
    c: Vertical(g1)
    c: Vertical(g3)
    c: DistanceY(g1,g-1) = 35
    c: DistanceY(g3,g3) = 70
    c: DistanceX(g0,g0) = 70
    c: DistanceX(g2,g-1) = 35
FEATURE [Sketcher::SketchObject] Sketch002
  FullyConstrained = false
  MapMode = 5
  Placement = pos=(0,0,15) rot=(0,0,1;0rad)
  sketch-geometry (9):
    g0: LineSegment StartX=-42.5383 StartY=25 StartZ=0 EndX=54.8117 EndY=25 EndZ=0
    g1: LineSegment StartX=-43.6541 StartY=-25 StartZ=0 EndX=49.7908 EndY=-25 EndZ=0
    g2: LineSegment StartX=-25 StartY=39.9582 StartZ=0 EndX=-25 EndY=-42.6081 EndZ=0
    g3: LineSegment StartX=25 StartY=42.3292 StartZ=0 EndX=25 EndY=-40.795 EndZ=0
    g4: Circle CenterX=-25 CenterY=25 CenterZ=0 NormalX=0 NormalY=0 NormalZ=1 AngleXU=0 Radius=3
    g5: Circle CenterX=25 CenterY=25 CenterZ=0 NormalX=0 NormalY=0 NormalZ=1 AngleXU=0 Radius=3
    g6: Circle CenterX=25 CenterY=-25 CenterZ=0 NormalX=0 NormalY=0 NormalZ=1 AngleXU=0 Radius=3
    g7: Circle CenterX=-25 CenterY=-25 CenterZ=0 NormalX=0 NormalY=0 NormalZ=1 AngleXU=0 Radius=3
    g8: Circle CenterX=0 CenterY=0 CenterZ=0 NormalX=0 NormalY=0 NormalZ=1 AngleXU=0 Radius=21
  constraints (18):
    c: Horizontal(g0)
    c: Horizontal(g1)
    c: Vertical(g2)
    c: Vertical(g3)
    c: PointOnObject(g4,g2)
    c: PointOnObject(g5,g0)
    c: PointOnObject(g6,g1)
    c: PointOnObject(g7,g1)
    c: PointOnObject(g5,g3)
    c: PointOnObject(g6,g3)
    c: Equal(g4,g5)
    c: Equal(g5,g6)
    c: Equal(g6,g7)
    c: Radius(g4) = 3
    c: Symmetric(g4,g7,g-1)
    c: Symmetric(g4,g5,g-2)
    c: Coincident(g8,g-1)
    c: Radius(g8) = 21
FEATURE [PartDesign::CoordinateSystem] LCS_FlangiaCuscinettoMandrino
  AttacherType = Attacher::AttachEngine3D
FEATURE [PartDesign::Pad] Pad
  Direction = (0,0,1)
  Length = 15
  Length2 = 100
  Profile = -> Sketch
  Type = 0
FEATURE [Sketcher::SketchObject] Sketch001
  FullyConstrained = true
  MapMode = 5
  Placement = pos=(0,0,15) rot=(0,0,1;0rad)
  Support = -> [Pad]
  sketch-geometry (1):
    g0: Circle CenterX=0 CenterY=0 CenterZ=0 NormalX=0 NormalY=0 NormalZ=1 AngleXU=0 Radius=26
  constraints (2):
    c: Coincident(g0,g-1)
    c: Radius(g0) = 26
FEATURE [PartDesign::Pocket] Pocket
  BaseFeature = -> Pad
  Direction = (0,0,-1)
  Length = 11
  Length2 = 5
  Profile = -> Sketch001
  ReferenceAxis = -> Sketch001 [N_Axis]
  Type = 0
FEATURE [PartDesign::Pocket] Pocket001
  BaseFeature = -> Pocket
  Direction = (0,0,-1)
  Length = 5
  Length2 = 5
  Profile = -> Sketch002
  ReferenceAxis = -> Sketch002 [N_Axis]
  Type = 1
FEATURE [PartDesign::Body] Body
  Group = -> [Sketch,Pad,Sketch001,Sketch002,LCS_FlangiaCuscinettoMandrino,Pocket,Pocket001]
  Origin = -> Origin
  Tip = -> Pocket001
---- part ../BloccoMandrino/FlangiaSupportoMandrino.FCStd = doc fcstd_6f6d0b2f52be ----
FCSTD DOCUMENT  (FreeCAD 0.21R33771 (Git))
Label: FlangiaSupportoMandrino
License: All rights reserved
LicenseURL: http://en.wikipedia.org/wiki/All_rights_reserved
objects: Sketcher::SketchObject×2, PartDesign::Pad×1, PartDesign::CoordinateSystem×1, PartDesign::Pocket×1, PartDesign::Body×1
note: 8 computed .brp shape members not serialized (recipe doc carries the construction recipe); baked Part::Feature solids carry a one-line shape summary decoded from their .brp

FEATURE [Sketcher::SketchObject] Sketch
  FullyConstrained = false
  MapMode = 5
  Placement = pos=(0,0,0) rot=(1,0,0;1.5708rad)
  Support = -> [XZ_Plane]
  sketch-geometry (13):
    g0: LineSegment StartX=0 StartY=0 StartZ=0 EndX=50 EndY=0 EndZ=0
    g1: LineSegment StartX=150 StartY=0 StartZ=0 EndX=150 EndY=120 EndZ=0
    g2: LineSegment StartX=100 StartY=170 StartZ=0 EndX=50 EndY=170 EndZ=0
    g3: LineSegment StartX=0 StartY=120 StartZ=0 EndX=0 EndY=0 EndZ=0
    g4: LineSegment StartX=50 StartY=170 StartZ=0 EndX=0 EndY=120 EndZ=0
    g5: LineSegment StartX=100 StartY=170 StartZ=0 EndX=150 EndY=120 EndZ=0
    g6: LineSegment StartX=50 StartY=0 StartZ=0 EndX=50 EndY=-50 EndZ=0
    g7: LineSegment StartX=50 StartY=-50 StartZ=0 EndX=100 EndY=-50 EndZ=0
    g8: LineSegment StartX=100 StartY=-50 StartZ=0 EndX=100 EndY=0 EndZ=0
    g9: LineSegment StartX=100 StartY=0 StartZ=0 EndX=150 EndY=0 EndZ=0
    g10: LineSegment StartX=57.3539 StartY=-25 StartZ=0 EndX=90.0763 EndY=-25 EndZ=0
    g11: LineSegment StartX=75 StartY=-16.1455 StartZ=0 EndX=75 EndY=-44.4932 EndZ=0
    g12: Circle CenterX=75 CenterY=-25 CenterZ=0 NormalX=0 NormalY=0 NormalZ=1 AngleXU=0 Radius=5
  constraints (36):
    c: Coincident(g9,g1)
    c: Coincident(g3,g0)
    c: Horizontal(g0)
    c: Horizontal(g2)
    c: Vertical(g1)
    c: Vertical(g3)
    c: Coincident(g0,g-1)
    c: DistanceX(g0,g9) = 150
    c: Coincident(g2,g5)
    c: Coincident(g1,g5)
    c: Coincident(g2,g4)
    c: Coincident(g3,g4)
    c: Angle(g-2,g4) = 2.35619
    c: Angle(g-2,g5) = 0.785398
    c: DistanceY(g1,g1) = 120
    c: Equal(g1,g3)
    c: DistanceY(g1,g2) = 50
    c: Vertical(g6)
    c: Coincident(g7,g6)
    c: Horizontal(g7)
    c: Coincident(g8,g7)
    c: Vertical(g8)
    c: Coincident(g0,g6)
    c: Coincident(g9,g8)
    c: DistanceX(g7,g7) = 50
    c: DistanceY(g8,g8) = 50
    c: Horizontal(g9)
    c: Equal(g8,g6)
    c: DistanceX(g0,g0) = 50
    c: Horizontal(g10)
    c: Vertical(g11)
    c: DistanceY(g10,g0) = 25
    c: DistanceX(g0,g11) = 75
    c: PointOnObject(g12,g11)
    c: PointOnObject(g12,g10)
    c: Radius(g12) = 5
FEATURE [PartDesign::Pad] Pad
  Direction = (0,-1,-2e-16)
  Length = 8
  Length2 = 100
  Placement = pos=(0,0,0) rot=(1,0,0;1.5708rad)
  Profile = -> Sketch
  Type = 0
FEATURE [PartDesign::CoordinateSystem] LCS_  label="LCS_FlangiaSupportoMotore"
  AttacherType = Attacher::AttachEngine3D
FEATURE [Sketcher::SketchObject] Sketch001
  FullyConstrained = true
  MapMode = 5
  Placement = pos=(0,0,0) rot=(1,0,0;1.5708rad)
  Support = -> [XZ_Plane]
  sketch-geometry (1):
    g0: Circle CenterX=75 CenterY=110 CenterZ=0 NormalX=0 NormalY=0 NormalZ=1 AngleXU=0 Radius=18
  constraints (3):
    c: DistanceX(g-1,g0) = 75
    c: Radius(g0) = 18
    c: DistanceY(g-1,g0) = 110
FEATURE [PartDesign::Pocket] Pocket
  BaseFeature = -> Pad
  Direction = (0,1,2e-16)
  Length = 5
  Length2 = 5
  Placement = pos=(0,0,0) rot=(1,0,0;1.5708rad)
  Profile = -> Sketch001
  ReferenceAxis = -> Sketch001 [N_Axis]
  Reversed = true
  Type = 1
FEATURE [PartDesign::Body] Body
  Group = -> [Sketch,Pad,LCS_,Sketch001,Pocket]
  Origin = -> Origin
  Tip = -> Pocket
---- part ../BloccoMandrino/IngranaggioM35.FCStd = doc fcstd_6e630a0a7936 ----
FCSTD DOCUMENT  (FreeCAD 0.21R33771 (Git))
Label: IngranaggioM35
License: All rights reserved
LicenseURL: http://en.wikipedia.org/wiki/All_rights_reserved
objects: Part::Part2DObjectPython×1, Sketcher::SketchObject×1, PartDesign::Pad×1, PartDesign::Pocket×1, PartDesign::CoordinateSystem×1, PartDesign::Body×1
note: 8 computed .brp shape members not serialized (recipe doc carries the construction recipe); baked Part::Feature solids carry a one-line shape summary decoded from their .brp

FEATURE [Part::Part2DObjectPython] InvoluteGear001  # Draft 2D object (typed FeaturePython)
  AddendumCoefficient = 1
  DedendumCoefficient = 1.25
  ExternalGear = true
  HighPrecision = true
  Modules = 1
  NumberOfTeeth = 35
  PressureAngle = 20
  ProfileShiftCoefficient = 0
  RootFilletCoefficient = 0.38
FEATURE [Sketcher::SketchObject] Sketch001
  FullyConstrained = true
  MapMode = 5
  Placement = pos=(0,0,7) rot=(0,0,1;0rad)
  sketch-geometry (4):
    g0: ArcOfCircle CenterX=0 CenterY=0 CenterZ=0 NormalX=0 NormalY=0 NormalZ=1 AngleXU=0 Radius=14 StartAngle=1.71414 EndAngle=7.71063
    g1: LineSegment StartX=-2 StartY=15 StartZ=0 EndX=2 EndY=15 EndZ=0
    g2: LineSegment StartX=-2 StartY=15 StartZ=0 EndX=-2 EndY=13.8564 EndZ=0
    g3: LineSegment StartX=2 StartY=15 StartZ=0 EndX=2 EndY=13.8564 EndZ=0
  constraints (11):
    c: Coincident(g0,g-1)
    c: Radius(g0) = 14
    c: Symmetric(g1,g1,g-2)
    c: DistanceX(g1,g1) = 4
    c: DistanceY(g0,g1) = 15
    c: Coincident(g2,g1)
    c: Vertical(g2)
    c: Coincident(g3,g1)
    c: Vertical(g3)
    c: Coincident(g2,g0)
    c: Coincident(g3,g0)
FEATURE [PartDesign::Pad] Pad
  Direction = (0,0,1)
  Length = 7
  Length2 = 10
  Profile = -> InvoluteGear001
  ReferenceAxis = -> InvoluteGear001 [N_Axis]
  Type = 0
FEATURE [PartDesign::Pocket] Pocket
  BaseFeature = -> Pad
  Direction = (0,0,-1)
  Length = 5
  Length2 = 5
  Profile = -> Sketch001
  ReferenceAxis = -> Sketch001 [N_Axis]
  Type = 1
FEATURE [PartDesign::CoordinateSystem] LCS_1_Ingranaggio35
  AttacherType = Attacher::AttachEngine3D
FEATURE [PartDesign::Body] Body
  Group = -> [InvoluteGear001,Pad,Sketch001,Pocket,LCS_1_Ingranaggio35]
  Origin = -> Origin
  Tip = -> Pocket
---- part ../BloccoMandrino/Mandrino.FCStd = doc fcstd_84db28730806 ----
FCSTD DOCUMENT  (FreeCAD 0.21R33771 (Git))
Label: Mandrino
License: All rights reserved
LicenseURL: http://en.wikipedia.org/wiki/All_rights_reserved
objects: Sketcher::SketchObject×4, PartDesign::Pocket×3, PartDesign::Chamfer×2, PartDesign::Pad×1, PartDesign::CoordinateSystem×1, PartDesign::Body×1
note: 18 computed .brp shape members not serialized (recipe doc carries the construction recipe); baked Part::Feature solids carry a one-line shape summary decoded from their .brp

FEATURE [Sketcher::SketchObject] Sketch
  FullyConstrained = true
  MapMode = 5
  Support = -> [XY_Plane]
  sketch-geometry (1):
    g0: Circle CenterX=0 CenterY=0 CenterZ=0 NormalX=0 NormalY=0 NormalZ=1 AngleXU=0 Radius=50
  constraints (2):
    c: Coincident(g0,g-1)
    c: Radius(g0) = 50
FEATURE [PartDesign::Pad] Pad
  Direction = (0,0,1)
  Length = 56
  Length2 = 10
  Profile = -> Sketch
  ReferenceAxis = -> Sketch [N_Axis]
  Type = 0
FEATURE [Sketcher::SketchObject] Sketch003
  FullyConstrained = true
  MapMode = 5
  Placement = pos=(0,0,0) rot=(1,0,0;3.14159rad)
  sketch-geometry (1):
    g0: Circle CenterX=0 CenterY=0 CenterZ=0 NormalX=0 NormalY=0 NormalZ=1 AngleXU=0 Radius=35
  constraints (2):
    c: Coincident(g0,g-1)
    c: Radius(g0) = 35
FEATURE [Sketcher::SketchObject] Sketch004
  FullyConstrained = true
  MapMode = 5
  Support = -> [XY_Plane]
  sketch-geometry (1):
    g0: Circle CenterX=0 CenterY=0 CenterZ=0 NormalX=0 NormalY=0 NormalZ=1 AngleXU=0 Radius=11
  constraints (2):
    c: Coincident(g0,g-1)
    c: Radius(g0) = 11
FEATURE [PartDesign::Pocket] Pocket
  BaseFeature = -> Pad
  Direction = (0,0,-1)
  Length = 5
  Length2 = 5
  Profile = -> Sketch004
  ReferenceAxis = -> Sketch004 [N_Axis]
  Reversed = true
  Type = 1
FEATURE [PartDesign::Pocket] Pocket001
  BaseFeature = -> Pocket
  Direction = (0,0,1)
  Length = 7
  Length2 = 5
  Profile = -> Sketch003
  ReferenceAxis = -> Sketch003 [N_Axis]
  Type = 0
FEATURE [PartDesign::Chamfer] Chamfer
  Angle = 45
  Base = -> Pocket001 [Edge3]
  BaseFeature = -> Pocket001
  ChamferType = 1
  FlipDirection = false
  Size = 15
  Size2 = 25
  SupportTransform = false
  UseAllEdges = false
FEATURE [PartDesign::CoordinateSystem] LCS_Mandrino
  AttacherType = Attacher::AttachEngine3D
FEATURE [Sketcher::SketchObject] Sketch005
  FullyConstrained = false
  MapMode = 5
  Placement = pos=(0,0,0) rot=(1,0,0;3.14159rad)
  Support = -> [Chamfer]
  sketch-geometry (6):
    g0: Circle CenterX=0 CenterY=0 CenterZ=0 NormalX=0 NormalY=0 NormalZ=1 AngleXU=0 Radius=41.75
    g1: Circle CenterX=0 CenterY=41.75 CenterZ=0 NormalX=0 NormalY=0 NormalZ=1 AngleXU=0 Radius=3.4
    g2: Circle CenterX=36.1566 CenterY=-20.875 CenterZ=0 NormalX=0 NormalY=0 NormalZ=1 AngleXU=0 Radius=3.4
    g3: Circle CenterX=-36.1566 CenterY=-20.875 CenterZ=0 NormalX=0 NormalY=0 NormalZ=1 AngleXU=0 Radius=3.4
    g4: LineSegment StartX=0 StartY=0 StartZ=0 EndX=-59.1845 EndY=-34.1702 EndZ=0
    g5: LineSegment StartX=0 StartY=0 StartZ=0 EndX=58.1579 EndY=-33.5775 EndZ=0
  constraints (16):
    c: Coincident(g0,g-1)
    c: PointOnObject(g1,g0)
    c: PointOnObject(g2,g0)
    c: PointOnObject(g3,g0)
    c: Radius(g1) = 3.4
    c: Equal(g1,g2)
    c: Equal(g2,g3)
    c: PointOnObject(g1,g-2)
    c: Radius(g0) = 41.75
    c: PointOnObject(g4,g-1)
    c: Coincident(g5,g0)
    c: PointOnObject(g0,g4)
    c: Angle(g4,g-1) = 2.61799
    c: Angle(g5,g-1) = 0.523599
    c: PointOnObject(g2,g5)
    c: PointOnObject(g3,g4)
FEATURE [PartDesign::Pocket] Pocket002
  BaseFeature = -> Chamfer
  Direction = (0,0,1)
  Length = 20
  Length2 = 5
  Profile = -> Sketch005
  ReferenceAxis = -> Sketch005 [N_Axis]
  Type = 0
FEATURE [PartDesign::Chamfer] Chamfer001
  Angle = 45
  Base = -> Pocket002 [Edge9,Edge6,Edge7]
  BaseFeature = -> Pocket002
  ChamferType = 0
  FlipDirection = false
  Size = 1
  Size2 = 1
  SupportTransform = false
  UseAllEdges = false
FEATURE [PartDesign::Body] Body
  Group = -> [Sketch,Pad,Sketch003,Sketch004,Pocket,Pocket001,Chamfer,LCS_Mandrino,Sketch005,Pocket002,Chamfer001]
  Origin = -> Origin
  Tip = -> Chamfer001
---- part ../BloccoMandrino/PiastraMandrinoRotante.FCStd = doc fcstd_9cd8f2e4074e ----
FCSTD DOCUMENT  (FreeCAD 0.21R33771 (Git))
Label: PiastraMandrinoRotante
License: All rights reserved
LicenseURL: http://en.wikipedia.org/wiki/All_rights_reserved
objects: Sketcher::SketchObject×1, PartDesign::Pad×1, PartDesign::CoordinateSystem×1, PartDesign::Body×1
note: 5 computed .brp shape members not serialized (recipe doc carries the construction recipe); baked Part::Feature solids carry a one-line shape summary decoded from their .brp

FEATURE [Sketcher::SketchObject] Sketch
  FullyConstrained = false
  MapMode = 5
  Support = -> [XY_Plane]
  sketch-geometry (41):
    g0: LineSegment StartX=-2.13e-14 StartY=0 StartZ=0 EndX=80 EndY=0 EndZ=0
    g1: LineSegment StartX=80 StartY=0 StartZ=0 EndX=80 EndY=78.7652 EndZ=0
    g2: LineSegment StartX=80 StartY=350 StartZ=0 EndX=0 EndY=350 EndZ=0
    g3: LineSegment StartX=-7.1e-15 StartY=350 StartZ=0 EndX=-7.1e-15 EndY=181.235 EndZ=0
    g4: Circle CenterX=10 CenterY=50 CenterZ=0 NormalX=0 NormalY=0 NormalZ=1 AngleXU=0 Radius=2
    g5: Circle CenterX=10 CenterY=110 CenterZ=0 NormalX=0 NormalY=0 NormalZ=1 AngleXU=0 Radius=2
    g6: LineSegment StartX=10 StartY=50 StartZ=0 EndX=10 EndY=110 EndZ=0
    g7: Circle CenterX=10 CenterY=170 CenterZ=0 NormalX=0 NormalY=0 NormalZ=1 AngleXU=0 Radius=2
    g8: LineSegment StartX=10 StartY=110 StartZ=0 EndX=10 EndY=170 EndZ=0
    g9: Circle CenterX=10 CenterY=230 CenterZ=0 NormalX=0 NormalY=0 NormalZ=1 AngleXU=0 Radius=2
    g10: LineSegment StartX=10 StartY=170 StartZ=0 EndX=10 EndY=230 EndZ=0
    g11: Circle CenterX=10 CenterY=290 CenterZ=0 NormalX=0 NormalY=0 NormalZ=1 AngleXU=0 Radius=2
    g12: LineSegment StartX=10 StartY=230 StartZ=0 EndX=10 EndY=290 EndZ=0
    g13: Circle CenterX=70 CenterY=50 CenterZ=0 NormalX=0 NormalY=0 NormalZ=1 AngleXU=0 Radius=2
    g14: LineSegment StartX=10 StartY=50 StartZ=0 EndX=70 EndY=50 EndZ=0
    g15: Circle CenterX=70 CenterY=110 CenterZ=0 NormalX=0 NormalY=0 NormalZ=1 AngleXU=0 Radius=2
    g16: LineSegment StartX=70 StartY=50 StartZ=0 EndX=70 EndY=110 EndZ=0
    g17: Circle CenterX=70 CenterY=170 CenterZ=0 NormalX=0 NormalY=0 NormalZ=1 AngleXU=0 Radius=2
    g18: LineSegment StartX=70 StartY=110 StartZ=0 EndX=70 EndY=170 EndZ=0
    g19: Circle CenterX=70 CenterY=230 CenterZ=0 NormalX=0 NormalY=0 NormalZ=1 AngleXU=0 Radius=2
    g20: LineSegment StartX=70 StartY=170 StartZ=0 EndX=70 EndY=230 EndZ=0
    g21: Circle CenterX=70 CenterY=290 CenterZ=0 NormalX=0 NormalY=0 NormalZ=1 AngleXU=0 Radius=2
    g22: LineSegment StartX=70 StartY=230 StartZ=0 EndX=70 EndY=290 EndZ=0
    g23: Circle CenterX=40 CenterY=130 CenterZ=0 NormalX=0 NormalY=0 NormalZ=1 AngleXU=0 Radius=5
    g24: LineSegment StartX=80 StartY=181.235 StartZ=0 EndX=80 EndY=350 EndZ=0
    g25: LineSegment StartX=-2.13e-14 StartY=78.7652 StartZ=0 EndX=-2.13e-14 EndY=0 EndZ=0
    g26: ArcOfCircle CenterX=40 CenterY=130 CenterZ=0 NormalX=0 NormalY=0 NormalZ=1 AngleXU=0 Radius=65 StartAngle=5.37526 EndAngle=7.19111
    g27: ArcOfCircle CenterX=40 CenterY=130 CenterZ=0 NormalX=0 NormalY=0 NormalZ=1 AngleXU=0 Radius=65 StartAngle=2.23367 EndAngle=4.04952
    g28: Circle CenterX=40 CenterY=130 CenterZ=0 NormalX=0 NormalY=0 NormalZ=1 AngleXU=0 Radius=56
    g29: LineSegment StartX=40 StartY=130 StartZ=0 EndX=40 EndY=205 EndZ=0
    g30: Circle CenterX=40 CenterY=205 CenterZ=0 NormalX=0 NormalY=0 NormalZ=1 AngleXU=0 Radius=3
    g31: ArcOfCircle CenterX=40 CenterY=130 CenterZ=0 NormalX=0 NormalY=0 NormalZ=1 AngleXU=0 Radius=59 StartAngle=2.35619 EndAngle=4.01426
    g32: ArcOfCircle CenterX=40 CenterY=130 CenterZ=0 NormalX=0 NormalY=0 NormalZ=1 AngleXU=0 Radius=53 StartAngle=2.35619 EndAngle=4.01426
    g33: LineSegment StartX=40 StartY=130 StartZ=0 EndX=-66.264 EndY=236.264 EndZ=0
    g34: LineSegment StartX=40 StartY=130 StartZ=0 EndX=-32.4746 EndY=43.6281 EndZ=0
    g35: ArcOfCircle CenterX=0.40202 CenterY=169.598 CenterZ=0 NormalX=0 NormalY=0 NormalZ=1 AngleXU=0 Radius=3 StartAngle=5.49778 EndAngle=8.63938
    g36: ArcOfCircle CenterX=4.00389 CenterY=87.1015 CenterZ=0 NormalX=0 NormalY=0 NormalZ=1 AngleXU=0 Radius=3 StartAngle=4.01426 EndAngle=7.15585
    g37: ArcOfCircle CenterX=40 CenterY=130 CenterZ=0 NormalX=0 NormalY=0 NormalZ=1 AngleXU=0 Radius=53 StartAngle=5.41052 EndAngle=7.06858
    g38: ArcOfCircle CenterX=79.598 CenterY=169.598 CenterZ=0 NormalX=0 NormalY=0 NormalZ=1 AngleXU=0 Radius=3 StartAngle=0.785398 EndAngle=3.927
    g39: ArcOfCircle CenterX=40 CenterY=130 CenterZ=0 NormalX=0 NormalY=0 NormalZ=1 AngleXU=0 Radius=59 StartAngle=5.41052 EndAngle=7.06858
    g40: ArcOfCircle CenterX=75.9961 CenterY=87.1015 CenterZ=0 NormalX=0 NormalY=0 NormalZ=1 AngleXU=0 Radius=3 StartAngle=2.26893 EndAngle=5.41052
  constraints (108):
    c: Coincident(g0,g1)
    c: Coincident(g24,g2)
    c: Coincident(g2,g3)
    c: Coincident(g25,g0)
    c: Horizontal(g0)
    c: Horizontal(g2)
    c: Vertical(g1)
    c: Vertical(g3)
    c: Coincident(g0,g-1)
    c: DistanceX(g0,g0) = 80
    c: DistanceY(g25,g3) = 350
    c: DistanceX(g0,g4) = 10
    c: DistanceY(g0,g4) = 50
    c: Radius(g4) = 2
    c: Radius(g5) = 2
    c: Coincident(g4,g6)
    c: Coincident(g5,g6)
    c: Distance(g6) = 60
    c: Angle(g6) = 1.5708
    c: Radius(g7) = 2
    c: Coincident(g5,g8)
    c: Coincident(g7,g8)
    c: Equal(g6,g8)
    c: Parallel(g8,g6)
    c: Radius(g9) = 2
    c: Coincident(g7,g10)
    c: Coincident(g9,g10)
    c: Equal(g6,g10)
    c: Parallel(g10,g6)
    c: Radius(g11) = 2
    c: Coincident(g9,g12)
    c: Coincident(g11,g12)
    c: Equal(g6,g12)
    c: Parallel(g12,g6)
    c: Radius(g13) = 2
    c: Coincident(g4,g14)
    c: Coincident(g13,g14)
    c: Distance(g14) = 60
    c: Perpendicular(g14,g6)
    c: Radius(g15) = 2
    c: Coincident(g13,g16)
    c: Coincident(g15,g16)
    c: Equal(g6,g16)
    c: Parallel(g16,g6)
    c: Radius(g17) = 2
    c: Coincident(g15,g18)
    c: Coincident(g17,g18)
    c: Equal(g6,g18)
    c: Parallel(g18,g6)
    c: Radius(g19) = 2
    c: Coincident(g17,g20)
    c: Coincident(g19,g20)
    c: Equal(g6,g20)
    c: Parallel(g20,g6)
    c: Radius(g21) = 2
    c: Coincident(g19,g22)
    c: Coincident(g21,g22)
    c: Equal(g6,g22)
    c: Parallel(g22,g6)
    c: Radius(g23) = 5
    c: Coincident(g27,g25)
    c: Coincident(g27,g3)
    c: Vertical(g25)
    c: Equal(g27,g26)
    c: Vertical(g24)
    c: Equal(g0,g2)
    c: Radius(g27) = 65
    c: Coincident(g24,g26)
    c: Coincident(g26,g1)
    c: Equal(g25,g1)
    c: Coincident(g27,g23)
    c: Equal(g3,g24)
    c: Coincident(g28,g23)
    c: Radius(g28) = 56
    c: Coincident(g29,g23)
    c: Vertical(g29)
    c: Coincident(g30,g29)
    c: Radius(g30) = 3
    c: DistanceY(g29,g29) = 75
    c: PointOnObject(g3,g-2)
    c: Coincident(g31,g23)
    c: Coincident(g32,g23)
    c: Coincident(g33,g23)
    c: Coincident(g34,g23)
    c: Angle(g33,g34) = 1.65806
    c: Angle(g29,g33) = 0.785398
    c: Radius(g31) = 59
    c: Radius(g32) = 53
    c: PointOnObject(g35,g33)
    c: Radius(g35) = 3
    c: PointOnObject(g36,g34)
    c: Equal(g36,g35)
    c: PointOnObject(g31,g33)
    c: PointOnObject(g35,g33)
    c: Coincident(g35,g32)
    c: PointOnObject(g31,g34)
    c: PointOnObject(g36,g34)
    c: Coincident(g36,g32)
    c: PointOnObject(g36,g28)
    c: PointOnObject(g35,g28)
    c: DistanceY(g0,g23) = 130
    c: DistanceX(g0,g26) = 40
    c: Radius(g39) = 59
    c: Radius(g37) = 53
    c: Radius(g38) = 3
    c: Equal(g40,g38)
    c: Coincident(g38,g37)
    c: Coincident(g40,g37)
FEATURE [PartDesign::Pad] Pad
  Direction = (0,0,1)
  Length = 10
  Length2 = 10
  Profile = -> Sketch
  ReferenceAxis = -> Sketch [N_Axis]
  Type = 0
FEATURE [PartDesign::CoordinateSystem] LCS_PiastraRotazioneUtensile
  AttacherType = Attacher::AttachEngine3D
  MapMode = 11
  Placement = pos=(40,130,10) rot=(0,0,1;1.5708rad)
  Support = -> [Pad]
FEATURE [PartDesign::Body] Body
  Group = -> [Sketch,Pad,LCS_PiastraRotazioneUtensile]
  Origin = -> Origin
  Tip = -> Pad
---- part ../BloccoMandrino/Reggispinta35x52x12.FCStd = doc fcstd_1eb25f528bc7 ----
FCSTD DOCUMENT  (FreeCAD 0.21R33771 (Git))
Label: Reggispinta35x52x12
License: All rights reserved
LicenseURL: http://en.wikipedia.org/wiki/All_rights_reserved
objects: Sketcher::SketchObject×1, PartDesign::Pad×1, PartDesign::CoordinateSystem×1, PartDesign::Body×1
note: 5 computed .brp shape members not serialized (recipe doc carries the construction recipe); baked Part::Feature solids carry a one-line shape summary decoded from their .brp

FEATURE [Sketcher::SketchObject] Sketch
  FullyConstrained = true
  MapMode = 5
  Support = -> [XY_Plane]
  sketch-geometry (2):
    g0: Circle CenterX=0 CenterY=0 CenterZ=0 NormalX=0 NormalY=0 NormalZ=1 AngleXU=0 Radius=17.5
    g1: Circle CenterX=0 CenterY=0 CenterZ=0 NormalX=0 NormalY=0 NormalZ=1 AngleXU=0 Radius=26
  constraints (4):
    c: Coincident(g0,g-1)
    c: Radius(g0) = 17.5
    c: Coincident(g1,g0)
    c: Radius(g1) = 26
FEATURE [PartDesign::Pad] Pad
  Direction = (1,1,1)
  Length = 12
  Length2 = 100
  Profile = -> Sketch
  Type = 0
FEATURE [PartDesign::CoordinateSystem] LCS_Reggispinta35x12
  AttacherType = Attacher::AttachEngine3D
FEATURE [PartDesign::Body] Body
  Group = -> [Sketch,Pad,LCS_Reggispinta35x12]
  Origin = -> Origin
  Tip = -> Pad
---- part ../Chiocciola16x4.FCStd = doc fcstd_8876642d731d ----
FCSTD DOCUMENT  (FreeCAD 0.21R33771 (Git))
Label: Chiocciola16x4
License: All rights reserved
LicenseURL: http://en.wikipedia.org/wiki/All_rights_reserved
objects: Sketcher::SketchObject×2, PartDesign::Revolution×1, PartDesign::Pocket×1, PartDesign::CoordinateSystem×1, PartDesign::Body×1
note: 8 computed .brp shape members not serialized (recipe doc carries the construction recipe); baked Part::Feature solids carry a one-line shape summary decoded from their .brp

FEATURE [Sketcher::SketchObject] Sketch
  FullyConstrained = true
  MapMode = 5
  Support = -> [XY_Plane]
  sketch-geometry (6):
    g0: LineSegment StartX=0 StartY=7 StartZ=0 EndX=0 EndY=20 EndZ=0
    g1: LineSegment StartX=0 StartY=20 StartZ=0 EndX=5 EndY=20 EndZ=0
    g2: LineSegment StartX=5 StartY=20 StartZ=0 EndX=5 EndY=11 EndZ=0
    g3: LineSegment StartX=5 StartY=11 StartZ=0 EndX=28 EndY=11 EndZ=0
    g4: LineSegment StartX=28 StartY=11 StartZ=0 EndX=28 EndY=7 EndZ=0
    g5: LineSegment StartX=28 StartY=7 StartZ=0 EndX=0 EndY=7 EndZ=0
  constraints (18):
    c: PointOnObject(g0,g-2)
    c: PointOnObject(g0,g-2)
    c: Coincident(g1,g0)
    c: Horizontal(g1)
    c: Coincident(g2,g1)
    c: Vertical(g2)
    c: Coincident(g3,g2)
    c: Horizontal(g3)
    c: Coincident(g4,g3)
    c: Vertical(g4)
    c: Coincident(g5,g4)
    c: Coincident(g5,g0)
    c: Horizontal(g5)
    c: DistanceY(g-1,g0) = 7
    c: DistanceY(g0,g0) = 13
    c: DistanceY(g4,g4) = 4
    c: DistanceX(g1,g1) = 5
    c: DistanceX(g5,g5) = 28
FEATURE [PartDesign::Revolution] Revolution
  Angle = 360
  Axis = (1,0,0)
  Base = (0,0,0)
  Profile = -> Sketch
  ReferenceAxis = -> Sketch [H_Axis]
FEATURE [Sketcher::SketchObject] Sketch001
  FullyConstrained = true
  MapMode = 5
  Placement = pos=(0,0,0) rot=(0.57735,-0.57735,-0.57735;2.0944rad)
  Support = -> [Revolution]
  sketch-geometry (5):
    g0: Circle CenterX=0 CenterY=0 CenterZ=0 NormalX=0 NormalY=0 NormalZ=1 AngleXU=0 Radius=15.5
    g1: Circle CenterX=0 CenterY=15.5 CenterZ=0 NormalX=0 NormalY=0 NormalZ=1 AngleXU=0 Radius=2.25
    g2: Circle CenterX=15.5 CenterY=0 CenterZ=0 NormalX=0 NormalY=0 NormalZ=1 AngleXU=0 Radius=2.25
    g3: Circle CenterX=0 CenterY=-15.5 CenterZ=0 NormalX=0 NormalY=0 NormalZ=1 AngleXU=0 Radius=2.25
    g4: Circle CenterX=-15.5 CenterY=0 CenterZ=0 NormalX=0 NormalY=0 NormalZ=1 AngleXU=0 Radius=2.25
  constraints (14):
    c: Coincident(g0,g-1)
    c: PointOnObject(g1,g0)
    c: PointOnObject(g2,g0)
    c: PointOnObject(g3,g0)
    c: PointOnObject(g4,g0)
    c: PointOnObject(g1,g-2)
    c: PointOnObject(g4,g-1)
    c: PointOnObject(g2,g-1)
    c: PointOnObject(g3,g-2)
    c: Equal(g1,g2)
    c: Equal(g2,g3)
    c: Equal(g3,g4)
    c: Radius(g1) = 2.25
    c: Radius(g0) = 15.5
FEATURE [PartDesign::Pocket] Pocket
  BaseFeature = -> Revolution
  Direction = (1,0,0)
  Length = 5
  Length2 = 5
  Profile = -> Sketch001
  ReferenceAxis = -> Sketch001 [N_Axis]
  Type = 0
FEATURE [PartDesign::CoordinateSystem] LCS_Chiociola16X4
  AttacherType = Attacher::AttachEngine3D
FEATURE [PartDesign::Body] Body  label="Corpo"
  Group = -> [Sketch,Revolution,Sketch001,Pocket,LCS_Chiociola16X4]
  Origin = -> Origin
  Tip = -> Pocket
---- part ../Contropunta/PiastraContropunta.FCStd = doc fcstd_a144cd0fb891 ----
FCSTD DOCUMENT  (FreeCAD 0.21R33771 (Git))
Label: PiastraContropunta
License: All rights reserved
LicenseURL: http://en.wikipedia.org/wiki/All_rights_reserved
objects: Sketcher::SketchObject×3, PartDesign::CoordinateSystem×1, PartDesign::Pad×1, PartDesign::Body×1
note: 7 computed .brp shape members not serialized (recipe doc carries the construction recipe); baked Part::Feature solids carry a one-line shape summary decoded from their .brp

FEATURE [Sketcher::SketchObject] Sketch
  FullyConstrained = true
  MapMode = 5
  Placement = pos=(0,0,0) rot=(1,0,0;1.5708rad)
  Support = -> [XZ_Plane]
  sketch-geometry (4):
    g0: LineSegment StartX=0 StartY=0 StartZ=0 EndX=130 EndY=0 EndZ=0
    g1: LineSegment StartX=130 StartY=0 StartZ=0 EndX=130 EndY=250 EndZ=0
    g2: LineSegment StartX=130 StartY=250 StartZ=0 EndX=0 EndY=250 EndZ=0
    g3: LineSegment StartX=0 StartY=250 StartZ=0 EndX=0 EndY=0 EndZ=0
  constraints (11):
    c: Coincident(g0,g1)
    c: Coincident(g1,g2)
    c: Coincident(g2,g3)
    c: Coincident(g3,g0)
    c: Horizontal(g0)
    c: Horizontal(g2)
    c: Vertical(g1)
    c: Vertical(g3)
    c: Coincident(g0,g-1)
    c: DistanceX(g0,g0) = 130
    c: DistanceY(g3,g3) = 250
FEATURE [Sketcher::SketchObject] Sketch001
  FullyConstrained = true
  MapMode = 5
  Placement = pos=(0,-10,0) rot=(1,0,0;1.5708rad)
  sketch-geometry (31):
    g0: Circle CenterX=5 CenterY=235 CenterZ=0 NormalX=0 NormalY=0 NormalZ=1 AngleXU=0 Radius=2.1
    g1: Circle CenterX=41 CenterY=235 CenterZ=0 NormalX=0 NormalY=0 NormalZ=1 AngleXU=0 Radius=2.1
    g2: LineSegment StartX=5 StartY=235 StartZ=0 EndX=41 EndY=235 EndZ=0
    g3: Circle CenterX=5 CenterY=203 CenterZ=0 NormalX=0 NormalY=0 NormalZ=1 AngleXU=0 Radius=2.1
    g4: LineSegment StartX=5 StartY=235 StartZ=0 EndX=5 EndY=203 EndZ=0
    g5: Circle CenterX=41 CenterY=203 CenterZ=0 NormalX=0 NormalY=0 NormalZ=1 AngleXU=0 Radius=2.1
    g6: LineSegment StartX=5 StartY=203 StartZ=0 EndX=41 EndY=203 EndZ=0
    g7: Circle CenterX=90 CenterY=235 CenterZ=0 NormalX=0 NormalY=0 NormalZ=1 AngleXU=0 Radius=2.1
    g8: Circle CenterX=126 CenterY=235 CenterZ=0 NormalX=0 NormalY=0 NormalZ=1 AngleXU=0 Radius=2.1
    g9: LineSegment StartX=90 StartY=235 StartZ=0 EndX=126 EndY=235 EndZ=0
    g10: Circle CenterX=90 CenterY=203 CenterZ=0 NormalX=0 NormalY=0 NormalZ=1 AngleXU=0 Radius=2.1
    g11: LineSegment StartX=90 StartY=235 StartZ=0 EndX=90 EndY=203 EndZ=0
    g12: Circle CenterX=126 CenterY=203 CenterZ=0 NormalX=0 NormalY=0 NormalZ=1 AngleXU=0 Radius=2.1
    g13: LineSegment StartX=90 StartY=203 StartZ=0 EndX=126 EndY=203 EndZ=0
    g14: LineSegment StartX=5 StartY=235 StartZ=0 EndX=90 EndY=235 EndZ=0
    g15: Circle CenterX=5 CenterY=45 CenterZ=0 NormalX=0 NormalY=0 NormalZ=1 AngleXU=0 Radius=2.1
    g16: Circle CenterX=41 CenterY=45 CenterZ=0 NormalX=0 NormalY=0 NormalZ=1 AngleXU=0 Radius=2.1
    g17: LineSegment StartX=5 StartY=45 StartZ=0 EndX=41 EndY=45 EndZ=0
    g18: Circle CenterX=5 CenterY=13 CenterZ=0 NormalX=0 NormalY=0 NormalZ=1 AngleXU=0 Radius=2.1
    g19: LineSegment StartX=5 StartY=45 StartZ=0 EndX=5 EndY=13 EndZ=0
    g20: Circle CenterX=41 CenterY=13 CenterZ=0 NormalX=0 NormalY=0 NormalZ=1 AngleXU=0 Radius=2.1
    g21: LineSegment StartX=5 StartY=13 StartZ=0 EndX=41 EndY=13 EndZ=0
    g22: LineSegment StartX=5 StartY=235 StartZ=0 EndX=5 EndY=45 EndZ=0
    g23: Circle CenterX=90 CenterY=45 CenterZ=0 NormalX=0 NormalY=0 NormalZ=1 AngleXU=0 Radius=2.1
    g24: Circle CenterX=126 CenterY=45 CenterZ=0 NormalX=0 NormalY=0 NormalZ=1 AngleXU=0 Radius=2.1
    g25: LineSegment StartX=90 StartY=45 StartZ=0 EndX=126 EndY=45 EndZ=0
    g26: Circle CenterX=90 CenterY=13 CenterZ=0 NormalX=0 NormalY=0 NormalZ=1 AngleXU=0 Radius=2.1
    g27: LineSegment StartX=90 StartY=45 StartZ=0 EndX=90 EndY=13 EndZ=0
    g28: Circle CenterX=126 CenterY=13 CenterZ=0 NormalX=0 NormalY=0 NormalZ=1 AngleXU=0 Radius=2.1
    g29: LineSegment StartX=90 StartY=13 StartZ=0 EndX=126 EndY=13 EndZ=0
    g30: LineSegment StartX=5 StartY=45 StartZ=0 EndX=90 EndY=45 EndZ=0
  constraints (78):
    c: Coincident(g0,g2)
    c: Coincident(g1,g2)
    c: Distance(g2) = 36
    c: Angle(g2) = 0
    c: Coincident(g0,g4)
    c: Coincident(g3,g4)
    c: Distance(g4) = 32
    c: Perpendicular(g4,g2)
    c: Coincident(g3,g6)
    c: Coincident(g5,g6)
    c: Equal(g2,g6)
    c: Parallel(g6,g2)
    c: Coincident(g7,g9)
    c: Coincident(g8,g9)
    c: Distance(g9) = 36
    c: Angle(g9) = 0
    c: Coincident(g7,g11)
    c: Coincident(g10,g11)
    c: Distance(g11) = 32
    c: Perpendicular(g11,g9)
    c: Coincident(g10,g13)
    c: Coincident(g12,g13)
    c: Equal(g9,g13)
    c: Parallel(g13,g9)
    c: Coincident(g0,g14)
    c: Coincident(g7,g14)
    c: Distance(g14) = 85
    c: Angle(g14) = 0
    c: Coincident(g15,g17)
    c: Coincident(g16,g17)
    c: Distance(g17) = 36
    c: Angle(g17) = 0
    c: Coincident(g15,g19)
    c: Coincident(g18,g19)
    c: Distance(g19) = 32
    c: Perpendicular(g19,g17)
    c: Coincident(g18,g21)
    c: Coincident(g20,g21)
    c: Equal(g17,g21)
    c: Parallel(g21,g17)
    c: Coincident(g0,g22)
    c: Coincident(g15,g22)
    c: Distance(g22) = 190
    c: Perpendicular(g22,g14)
    c: Coincident(g23,g25)
    c: Coincident(g24,g25)
    c: Distance(g25) = 36
    c: Angle(g25) = 0
    c: Coincident(g23,g27)
    c: Coincident(g26,g27)
    c: Perpendicular(g27,g25)
    c: Coincident(g26,g29)
    c: Coincident(g28,g29)
    c: Equal(g25,g29)
    c: Parallel(g29,g25)
    c: Coincident(g15,g30)
    c: Coincident(g23,g30)
    c: Equal(g14,g30)
    c: Parallel(g30,g14)
    c: DistanceY(g-1,g0) = 235
    c: DistanceX(g-1,g0) = 5
    c: Radius(g0) = 2.1
    c: Equal(g3,g0)
    c: Equal(g0,g1)
    c: Equal(g1,g5)
    c: Equal(g5,g10)
    c: Equal(g10,g12)
    c: Equal(g12,g8)
    c: Equal(g8,g7)
    c: Equal(g16,g23)
    c: Equal(g23,g24)
    c: Equal(g24,g18)
    c: Equal(g18,g20)
    c: Equal(g15,g16)
    c: Equal(g24,g28)
    c: Equal(g28,g26)
    c: Equal(g27,g19)
    c: Equal(g3,g15)
FEATURE [Sketcher::SketchObject] Sketch002
  FullyConstrained = false
  MapMode = 5
  Placement = pos=(0,-10,0) rot=(1,0,0;1.5708rad)
  sketch-geometry (15):
    g0: Circle CenterX=15 CenterY=280 CenterZ=0 NormalX=0 NormalY=0 NormalZ=1 AngleXU=0 Radius=4
    g1: Circle CenterX=5 CenterY=13 CenterZ=0 NormalX=0 NormalY=0 NormalZ=1 AngleXU=0 Radius=4
    g2: Circle CenterX=5 CenterY=45 CenterZ=0 NormalX=0 NormalY=0 NormalZ=1 AngleXU=0 Radius=4
    g3: LineSegment StartX=5 StartY=13 StartZ=0 EndX=5 EndY=45 EndZ=0
    g4: Circle CenterX=41 CenterY=13 CenterZ=0 NormalX=0 NormalY=0 NormalZ=1 AngleXU=0 Radius=4
    g5: LineSegment StartX=5 StartY=13 StartZ=0 EndX=41 EndY=13 EndZ=0
    g6: Circle CenterX=41 CenterY=45 CenterZ=0 NormalX=0 NormalY=0 NormalZ=1 AngleXU=0 Radius=4
    g7: LineSegment StartX=41 StartY=13 StartZ=0 EndX=41 EndY=45 EndZ=0
    g8: Circle CenterX=90 CenterY=13 CenterZ=0 NormalX=0 NormalY=0 NormalZ=1 AngleXU=0 Radius=4
    g9: Circle CenterX=90 CenterY=45 CenterZ=0 NormalX=0 NormalY=0 NormalZ=1 AngleXU=0 Radius=4
    g10: LineSegment StartX=90 StartY=13 StartZ=0 EndX=90 EndY=45 EndZ=0
    g11: Circle CenterX=126 CenterY=13 CenterZ=0 NormalX=0 NormalY=0 NormalZ=1 AngleXU=0 Radius=4
    g12: LineSegment StartX=90 StartY=13 StartZ=0 EndX=126 EndY=13 EndZ=0
    g13: Circle CenterX=126 CenterY=45 CenterZ=0 NormalX=0 NormalY=0 NormalZ=1 AngleXU=0 Radius=4
    g14: LineSegment StartX=126 StartY=13 StartZ=0 EndX=126 EndY=45 EndZ=0
  constraints (36):
    c: DistanceY(g-1,g1) = 13
    c: DistanceX(g-1,g1) = 5
    c: Radius(g1) = 4
    c: Radius(g2) = 4
    c: Coincident(g1,g3)
    c: Coincident(g2,g3)
    c: Distance(g3) = 32
    c: Angle(g3) = 1.5708
    c: Radius(g4) = 4
    c: Coincident(g1,g5)
    c: Coincident(g4,g5)
    c: Distance(g5) = 36
    c: Perpendicular(g5,g3)
    c: Radius(g6) = 4
    c: Coincident(g4,g7)
    c: Coincident(g6,g7)
    c: Equal(g3,g7)
    c: Parallel(g7,g3)
    c: DistanceY(g-1,g8) = 13
    c: Radius(g8) = 4
    c: Radius(g9) = 4
    c: Coincident(g8,g10)
    c: Coincident(g9,g10)
    c: Distance(g10) = 32
    c: Angle(g10) = 1.5708
    c: Radius(g11) = 4
    c: Coincident(g8,g12)
    c: Coincident(g11,g12)
    c: Distance(g12) = 36
    c: Perpendicular(g12,g10)
    c: Radius(g13) = 4
    c: Coincident(g11,g14)
    c: Coincident(g13,g14)
    c: Equal(g10,g14)
    c: Parallel(g14,g10)
    c: DistanceX(g1,g8) = 85
FEATURE [PartDesign::CoordinateSystem] LCS_PiastraContropunta
  AttacherType = Attacher::AttachEngine3D
FEATURE [PartDesign::Pad] Pad
  Direction = (0,-1,-2e-16)
  Length = 10
  Length2 = 10
  Placement = pos=(0,0,0) rot=(1,0,0;1.5708rad)
  Profile = -> Sketch
  ReferenceAxis = -> Sketch [N_Axis]
  Type = 0
FEATURE [PartDesign::Body] Body
  Group = -> [Sketch,Sketch001,Sketch002,LCS_PiastraContropunta,Pad]
  Origin = -> Origin
  Tip = -> Pad
---- part ../DistanzialeBasamentoC.FCStd = doc fcstd_04e8804abaee ----
FCSTD DOCUMENT  (FreeCAD 0.21R33771 (Git))
Label: DistanzialeBasamentoC
License: All rights reserved
LicenseURL: http://en.wikipedia.org/wiki/All_rights_reserved
objects: Sketcher::SketchObject×1, PartDesign::Pad×1, PartDesign::CoordinateSystem×1, PartDesign::Body×1
note: 5 computed .brp shape members not serialized (recipe doc carries the construction recipe); baked Part::Feature solids carry a one-line shape summary decoded from their .brp

FEATURE [Sketcher::SketchObject] Sketch
  FullyConstrained = true
  MapMode = 5
  Support = -> [XY_Plane]
  sketch-geometry (8):
    g0: LineSegment StartX=0 StartY=0 StartZ=0 EndX=40 EndY=0 EndZ=0
    g1: LineSegment StartX=40 StartY=0 StartZ=0 EndX=40 EndY=40 EndZ=0
    g2: LineSegment StartX=40 StartY=40 StartZ=0 EndX=0 EndY=40 EndZ=0
    g3: LineSegment StartX=0 StartY=40 StartZ=0 EndX=0 EndY=0 EndZ=0
    g4: LineSegment StartX=2 StartY=38 StartZ=0 EndX=38 EndY=38 EndZ=0
    g5: LineSegment StartX=38 StartY=38 StartZ=0 EndX=38 EndY=2 EndZ=0
    g6: LineSegment StartX=38 StartY=2 StartZ=0 EndX=2 EndY=2 EndZ=0
    g7: LineSegment StartX=2 StartY=2 StartZ=0 EndX=2 EndY=38 EndZ=0
  constraints (23):
    c: Coincident(g0,g1)
    c: Coincident(g1,g2)
    c: Coincident(g2,g3)
    c: Coincident(g3,g0)
    c: Horizontal(g0)
    c: Horizontal(g2)
    c: Vertical(g1)
    c: Vertical(g3)
    c: Coincident(g0,g-1)
    c: DistanceX(g0,g0) = 40
    c: DistanceY(g3,g3) = 40
    c: Coincident(g4,g5)
    c: Coincident(g5,g6)
    c: Coincident(g6,g7)
    c: Coincident(g7,g4)
    c: Horizontal(g4)
    c: Horizontal(g6)
    c: Vertical(g5)
    c: Vertical(g7)
    c: DistanceX(g6,g6) = 36
    c: DistanceY(g5,g5) = 36
    c: DistanceX(g0,g6) = 2
    c: DistanceY(g0,g5) = 2
FEATURE [PartDesign::Pad] Pad
  Direction = (0,0,1)
  Length = 158
  Length2 = 10
  Profile = -> Sketch
  ReferenceAxis = -> Sketch [N_Axis]
  Type = 0
FEATURE [PartDesign::CoordinateSystem] LCS_DistanzialeBasamentoC
  AttacherType = Attacher::AttachEngine3D
FEATURE [PartDesign::Body] Body  label="Corpo"
  Group = -> [Sketch,Pad,LCS_DistanzialeBasamentoC]
  Origin = -> Origin
  Tip = -> Pad
---- part ../Guida-quadra-20-800.FCStd = doc fcstd_de21a5611281 ----
FCSTD DOCUMENT  (FreeCAD 0.21R33771 (Git))
Label: Guida-quadra-20-800
License: All rights reserved
LicenseURL: https://en.wikipedia.org/wiki/All_rights_reserved
objects: Sketcher::SketchObject×3, PartDesign::Pocket×2, PartDesign::Pad×1, PartDesign::CoordinateSystem×1, PartDesign::Body×1
note: 11 computed .brp shape members not serialized (recipe doc carries the construction recipe); baked Part::Feature solids carry a one-line shape summary decoded from their .brp

FEATURE [Sketcher::SketchObject] Sketch
  FullyConstrained = true
  MapMode = 5
  Support = -> [XY_Plane]
  sketch-geometry (10):
    g0: LineSegment StartX=-9.5 StartY=0 StartZ=0 EndX=9.5 EndY=0 EndZ=0
    g1: LineSegment StartX=9.5 StartY=17.409 StartZ=0 EndX=-9.5 EndY=17.409 EndZ=0
    g2: LineSegment StartX=-9.81069 StartY=16.5173 StartZ=0 EndX=-4 EndY=11.909 EndZ=0
    g3: LineSegment StartX=-4 StartY=11.909 StartZ=0 EndX=-9.94147 EndY=0.734736 EndZ=0
    g4: LineSegment StartX=9.81069 StartY=16.5173 StartZ=0 EndX=4 EndY=11.909 EndZ=0
    g5: LineSegment StartX=4 StartY=11.909 StartZ=0 EndX=9.94147 EndY=0.734736 EndZ=0
    g6: ArcOfCircle CenterX=-9.5 CenterY=0.5 CenterZ=0 NormalX=0 NormalY=0 NormalZ=1 AngleXU=0 Radius=0.5 StartAngle=2.6529 EndAngle=4.71239
    g7: ArcOfCircle CenterX=9.5 CenterY=0.5 CenterZ=0 NormalX=0 NormalY=0 NormalZ=1 AngleXU=0 Radius=0.5 StartAngle=4.71239 EndAngle=6.77188
    g8: ArcOfCircle CenterX=-9.5 CenterY=16.909 CenterZ=0 NormalX=0 NormalY=0 NormalZ=1 AngleXU=0 Radius=0.5 StartAngle=1.5708 EndAngle=4.04189
    g9: ArcOfCircle CenterX=9.5 CenterY=16.909 CenterZ=0 NormalX=0 NormalY=0 NormalZ=1 AngleXU=0 Radius=0.5 StartAngle=5.38289 EndAngle=7.85398
  constraints (23):
    c: Coincident(g3,g2)
    c: Coincident(g5,g4)
    c: Equal(g0,g1)
    c: Tangent(g3,g6) = -1.5708
    c: Tangent(g0,g6) = -1.5708
    c: Tangent(g5,g7) = 1.5708
    c: Tangent(g0,g7) = -1.5708
    c: Radius(g7) = 0.5
    c: Equal(g6,g7)
    c: Tangent(g2,g8) = -1.5708
    c: Tangent(g1,g8) = -1.5708
    c: Tangent(g1,g9) = -1.5708
    c: Tangent(g4,g9) = 1.5708
    c: Symmetric(g6,g7,g-2)
    c: Symmetric(g8,g9,g-2)
    c: Equal(g7,g9)
    c: Equal(g9,g8)
    c: Symmetric(g2,g4,g-2)
    c: DistanceX(g6,g7) = 19
    c: DistanceY(g4,g9) = 5
    c: DistanceX(g2,g-1) = 4
    c: PointOnObject(g-1,g0)
    c: Angle(g5,g0) = 1.0821
FEATURE [PartDesign::Pad] Pad
  Direction = (0,0,1)
  Length = 800
  Length2 = 10
  Profile = -> Sketch
  ReferenceAxis = -> Sketch [N_Axis]
  Type = 0
FEATURE [Sketcher::SketchObject] Sketch001
  FullyConstrained = true
  MapMode = 5
  Placement = pos=(0,17.409,0) rot=(0,0.707107,0.707107;3.14159rad)
  Support = -> [Pad]
  sketch-geometry (25):
    g0: Circle CenterX=0 CenterY=20 CenterZ=0 NormalX=0 NormalY=0 NormalZ=1 AngleXU=0 Radius=3
    g1: Circle CenterX=3.7e-15 CenterY=80 CenterZ=0 NormalX=0 NormalY=0 NormalZ=1 AngleXU=0 Radius=3
    g2: LineSegment StartX=0 StartY=20 StartZ=0 EndX=3.7e-15 EndY=80 EndZ=0
    g3: Circle CenterX=7.4e-15 CenterY=140 CenterZ=0 NormalX=0 NormalY=0 NormalZ=1 AngleXU=0 Radius=3
    g4: LineSegment StartX=3.7e-15 StartY=80 StartZ=0 EndX=7.4e-15 EndY=140 EndZ=0
    g5: Circle CenterX=1.1e-14 CenterY=200 CenterZ=0 NormalX=0 NormalY=0 NormalZ=1 AngleXU=0 Radius=3
    g6: LineSegment StartX=7.4e-15 StartY=140 StartZ=0 EndX=1.1e-14 EndY=200 EndZ=0
    g7: Circle CenterX=1.47e-14 CenterY=260 CenterZ=0 NormalX=0 NormalY=0 NormalZ=1 AngleXU=0 Radius=3
    g8: LineSegment StartX=1.1e-14 StartY=200 StartZ=0 EndX=1.47e-14 EndY=260 EndZ=0
    g9: Circle CenterX=1.84e-14 CenterY=320 CenterZ=0 NormalX=0 NormalY=0 NormalZ=1 AngleXU=0 Radius=3
    g10: LineSegment StartX=1.47e-14 StartY=260 StartZ=0 EndX=1.84e-14 EndY=320 EndZ=0
    g11: Circle CenterX=2.21e-14 CenterY=380 CenterZ=0 NormalX=0 NormalY=0 NormalZ=1 AngleXU=0 Radius=3
    g12: LineSegment StartX=1.84e-14 StartY=320 StartZ=0 EndX=2.21e-14 EndY=380 EndZ=0
    g13: Circle CenterX=2.57e-14 CenterY=440 CenterZ=0 NormalX=0 NormalY=0 NormalZ=1 AngleXU=0 Radius=3
    g14: LineSegment StartX=2.21e-14 StartY=380 StartZ=0 EndX=2.57e-14 EndY=440 EndZ=0
    g15: Circle CenterX=2.94e-14 CenterY=500 CenterZ=0 NormalX=0 NormalY=0 NormalZ=1 AngleXU=0 Radius=3
    g16: LineSegment StartX=2.57e-14 StartY=440 StartZ=0 EndX=2.94e-14 EndY=500 EndZ=0
    g17: Circle CenterX=3.31e-14 CenterY=560 CenterZ=0 NormalX=0 NormalY=0 NormalZ=1 AngleXU=0 Radius=3
    g18: LineSegment StartX=2.94e-14 StartY=500 StartZ=0 EndX=3.31e-14 EndY=560 EndZ=0
    g19: Circle CenterX=3.68e-14 CenterY=620 CenterZ=0 NormalX=0 NormalY=0 NormalZ=1 AngleXU=0 Radius=3
    g20: LineSegment StartX=3.31e-14 StartY=560 StartZ=0 EndX=3.68e-14 EndY=620 EndZ=0
    g21: Circle CenterX=4.04e-14 CenterY=680 CenterZ=0 NormalX=0 NormalY=0 NormalZ=1 AngleXU=0 Radius=3
    g22: LineSegment StartX=3.68e-14 StartY=620 StartZ=0 EndX=4.04e-14 EndY=680 EndZ=0
    g23: Circle CenterX=4.41e-14 CenterY=740 CenterZ=0 NormalX=0 NormalY=0 NormalZ=1 AngleXU=0 Radius=3
    g24: LineSegment StartX=4.04e-14 StartY=680 StartZ=0 EndX=4.41e-14 EndY=740 EndZ=0
  constraints (63):
    c: PointOnObject(g0,g-2)
    c: Radius(g0) = 3
    c: DistanceY(g-1,g0) = 20
    c: Radius(g1) = 3
    c: Coincident(g0,g2)
    c: Coincident(g1,g2)
    c: Distance(g2) = 60
    c: Angle(g2) = 1.5708
    c: Radius(g3) = 3
    c: Coincident(g1,g4)
    c: Coincident(g3,g4)
    c: Equal(g2,g4)
    c: Parallel(g4,g2)
    c: Radius(g5) = 3
    c: Coincident(g3,g6)
    c: Coincident(g5,g6)
    c: Equal(g2,g6)
    c: Parallel(g6,g2)
    c: Radius(g7) = 3
    c: Coincident(g5,g8)
    c: Coincident(g7,g8)
    c: Equal(g2,g8)
    c: Parallel(g8,g2)
    c: Radius(g9) = 3
    c: Coincident(g7,g10)
    c: Coincident(g9,g10)
    c: Equal(g2,g10)
    c: Parallel(g10,g2)
    c: Radius(g11) = 3
    c: Coincident(g9,g12)
    c: Coincident(g11,g12)
    c: Equal(g2,g12)
    c: Parallel(g12,g2)
    c: Radius(g13) = 3
    c: Coincident(g11,g14)
    c: Coincident(g13,g14)
    c: Equal(g2,g14)
    c: Parallel(g14,g2)
    c: Radius(g15) = 3
    c: Coincident(g13,g16)
    c: Coincident(g15,g16)
    c: Equal(g2,g16)
    c: Parallel(g16,g2)
    c: Radius(g17) = 3
    c: Coincident(g15,g18)
    c: Coincident(g17,g18)
    c: Equal(g2,g18)
    c: Parallel(g18,g2)
    c: Radius(g19) = 3
    c: Coincident(g17,g20)
    c: Coincident(g19,g20)
    c: Equal(g2,g20)
    c: Parallel(g20,g2)
    c: Radius(g21) = 3
    c: Coincident(g19,g22)
    c: Coincident(g21,g22)
    c: Equal(g2,g22)
    c: Parallel(g22,g2)
    c: Radius(g23) = 3
    c: Coincident(g21,g24)
    c: Coincident(g23,g24)
    c: Equal(g2,g24)
    c: Parallel(g24,g2)
FEATURE [PartDesign::Pocket] Pocket
  BaseFeature = -> Pad
  Direction = (0,-1,2e-16)
  Length = 5
  Length2 = 5
  Profile = -> Sketch001
  ReferenceAxis = -> Sketch001 [N_Axis]
  Type = 1
FEATURE [Sketcher::SketchObject] Sketch002
  ExternalGeometry = -> [Pocket]
  FullyConstrained = true
  MapMode = 5
  Placement = pos=(0,17.409,0) rot=(0,0.707107,0.707107;3.14159rad)
  Support = -> [Pocket]
  sketch-geometry (27):
    g0: Circle CenterX=0 CenterY=20 CenterZ=0 NormalX=0 NormalY=0 NormalZ=1 AngleXU=0 Radius=5
    g1: Circle CenterX=0 CenterY=80 CenterZ=0 NormalX=0 NormalY=0 NormalZ=1 AngleXU=0 Radius=5
    g2: LineSegment StartX=0 StartY=20 StartZ=0 EndX=0 EndY=80 EndZ=0
    g3: Circle CenterX=0 CenterY=140 CenterZ=0 NormalX=0 NormalY=0 NormalZ=1 AngleXU=0 Radius=5
    g4: LineSegment StartX=0 StartY=80 StartZ=0 EndX=0 EndY=140 EndZ=0
    g5: Circle CenterX=0 CenterY=200 CenterZ=0 NormalX=0 NormalY=0 NormalZ=1 AngleXU=0 Radius=5
    g6: LineSegment StartX=0 StartY=140 StartZ=0 EndX=0 EndY=200 EndZ=0
    g7: Circle CenterX=0 CenterY=260 CenterZ=0 NormalX=0 NormalY=0 NormalZ=1 AngleXU=0 Radius=5
    g8: LineSegment StartX=0 StartY=200 StartZ=0 EndX=0 EndY=260 EndZ=0
    g9: Circle CenterX=0 CenterY=320 CenterZ=0 NormalX=0 NormalY=0 NormalZ=1 AngleXU=0 Radius=5
    g10: LineSegment StartX=0 StartY=260 StartZ=0 EndX=0 EndY=320 EndZ=0
    g11: Circle CenterX=0 CenterY=380 CenterZ=0 NormalX=0 NormalY=0 NormalZ=1 AngleXU=0 Radius=5
    g12: LineSegment StartX=0 StartY=320 StartZ=0 EndX=0 EndY=380 EndZ=0
    g13: Circle CenterX=0 CenterY=440 CenterZ=0 NormalX=0 NormalY=0 NormalZ=1 AngleXU=0 Radius=5
    g14: LineSegment StartX=0 StartY=380 StartZ=0 EndX=0 EndY=440 EndZ=0
    g15: Circle CenterX=0 CenterY=500 CenterZ=0 NormalX=0 NormalY=0 NormalZ=1 AngleXU=0 Radius=5
    g16: LineSegment StartX=0 StartY=440 StartZ=0 EndX=0 EndY=500 EndZ=0
    g17: Circle CenterX=0 CenterY=560 CenterZ=0 NormalX=0 NormalY=0 NormalZ=1 AngleXU=0 Radius=5
    g18: LineSegment StartX=0 StartY=500 StartZ=0 EndX=0 EndY=560 EndZ=0
    g19: Circle CenterX=0 CenterY=620 CenterZ=0 NormalX=0 NormalY=0 NormalZ=1 AngleXU=0 Radius=5
    g20: LineSegment StartX=0 StartY=560 StartZ=0 EndX=0 EndY=620 EndZ=0
    g21: Circle CenterX=0 CenterY=680 CenterZ=0 NormalX=0 NormalY=0 NormalZ=1 AngleXU=0 Radius=5
    g22: LineSegment StartX=0 StartY=620 StartZ=0 EndX=0 EndY=680 EndZ=0
    g23: Circle CenterX=0 CenterY=740 CenterZ=0 NormalX=0 NormalY=0 NormalZ=1 AngleXU=0 Radius=5
    g24: LineSegment StartX=0 StartY=680 StartZ=0 EndX=0 EndY=740 EndZ=0
    g25: Circle CenterX=0 CenterY=800 CenterZ=0 NormalX=0 NormalY=0 NormalZ=1 AngleXU=0 Radius=5
    g26: LineSegment StartX=0 StartY=740 StartZ=0 EndX=0 EndY=800 EndZ=0
  constraints (67):
    c: Radius(g0) = 5
    c: Coincident(g0,g-4)
    c: Radius(g1) = 5
    c: Coincident(g0,g2)
    c: Coincident(g1,g2)
    c: Angle(g2) = 1.5708
    c: Radius(g3) = 5
    c: Coincident(g1,g4)
    c: Coincident(g3,g4)
    c: Equal(g2,g4)
    c: Parallel(g4,g2)
    c: Radius(g5) = 5
    c: Coincident(g3,g6)
    c: Coincident(g5,g6)
    c: Equal(g2,g6)
    c: Parallel(g6,g2)
    c: Radius(g7) = 5
    c: Coincident(g5,g8)
    c: Coincident(g7,g8)
    c: Equal(g2,g8)
    c: Parallel(g8,g2)
    c: Radius(g9) = 5
    c: Coincident(g7,g10)
    c: Coincident(g9,g10)
    c: Equal(g2,g10)
    c: Parallel(g10,g2)
    c: Radius(g11) = 5
    c: Coincident(g9,g12)
    c: Coincident(g11,g12)
    c: Equal(g2,g12)
    c: Parallel(g12,g2)
    c: Radius(g13) = 5
    c: Coincident(g11,g14)
    c: Coincident(g13,g14)
    c: Equal(g2,g14)
    c: Parallel(g14,g2)
    c: Radius(g15) = 5
    c: Coincident(g13,g16)
    c: Coincident(g15,g16)
    c: Equal(g2,g16)
    c: Parallel(g16,g2)
    c: Radius(g17) = 5
    c: Coincident(g15,g18)
    c: Coincident(g17,g18)
    c: Equal(g2,g18)
    c: Parallel(g18,g2)
    c: Radius(g19) = 5
    c: Coincident(g17,g20)
    c: Coincident(g19,g20)
    c: Equal(g2,g20)
    c: Parallel(g20,g2)
    c: Radius(g21) = 5
    c: Coincident(g19,g22)
    c: Coincident(g21,g22)
    c: Equal(g2,g22)
    c: Parallel(g22,g2)
    c: Radius(g23) = 5
    c: Coincident(g21,g24)
    c: Coincident(g23,g24)
    c: Equal(g2,g24)
    c: Parallel(g24,g2)
    c: Radius(g25) = 5
    c: Coincident(g23,g26)
    c: Coincident(g25,g26)
    c: Equal(g2,g26)
    c: Parallel(g26,g2)
    c: Coincident(g1,g-5)
FEATURE [PartDesign::Pocket] Pocket001
  BaseFeature = -> Pocket
  Direction = (0,-1,2e-16)
  Length = 5
  Length2 = 5
  Profile = -> Sketch002
  ReferenceAxis = -> Sketch002 [N_Axis]
  Type = 0
FEATURE [PartDesign::CoordinateSystem] LCS_GuidaQuadrata_20x800
  AttacherType = Attacher::AttachEngine3D
FEATURE [PartDesign::Body] Body
  Group = -> [Sketch,Pad,Sketch001,Pocket,Sketch002,Pocket001,LCS_GuidaQuadrata_20x800]
  Origin = -> Origin
  Tip = -> Pocket001
---- part ../Pattino-20.FCStd = doc fcstd_0acbeb565758 ----
FCSTD DOCUMENT  (FreeCAD 0.21R33771 (Git))
Label: Pattino-20
License: All rights reserved
LicenseURL: http://en.wikipedia.org/wiki/All_rights_reserved
objects: Sketcher::SketchObject×2, PartDesign::CoordinateSystem×1, PartDesign::Pad×1, PartDesign::Body×1
note: 6 computed .brp shape members not serialized (recipe doc carries the construction recipe); baked Part::Feature solids carry a one-line shape summary decoded from their .brp

FEATURE [Sketcher::SketchObject] Sketch
  FullyConstrained = true
  MapMode = 5
  Support = -> [XY_Plane]
  sketch-geometry (8):
    g0: LineSegment StartX=0 StartY=0 StartZ=0 EndX=11 EndY=0 EndZ=0
    g1: LineSegment StartX=44 StartY=0 StartZ=0 EndX=44 EndY=25 EndZ=0
    g2: LineSegment StartX=44 StartY=25 StartZ=0 EndX=0 EndY=25 EndZ=0
    g3: LineSegment StartX=0 StartY=25 StartZ=0 EndX=0 EndY=0 EndZ=0
    g4: LineSegment StartX=11 StartY=0 StartZ=0 EndX=11 EndY=14 EndZ=0
    g5: LineSegment StartX=11 StartY=14 StartZ=0 EndX=31 EndY=14 EndZ=0
    g6: LineSegment StartX=31 StartY=14 StartZ=0 EndX=31 EndY=0 EndZ=0
    g7: LineSegment StartX=31 StartY=0 StartZ=0 EndX=44 EndY=0 EndZ=0
  constraints (22):
    c: Coincident(g7,g1)
    c: Coincident(g1,g2)
    c: Coincident(g2,g3)
    c: Coincident(g3,g0)
    c: Horizontal(g0)
    c: Horizontal(g2)
    c: Vertical(g1)
    c: Vertical(g3)
    c: Coincident(g0,g-1)
    c: DistanceY(g1,g1) = 25
    c: DistanceX(g2,g2) = 44
    c: Vertical(g4)
    c: Coincident(g5,g4)
    c: Horizontal(g5)
    c: Coincident(g6,g5)
    c: Vertical(g6)
    c: Coincident(g0,g4)
    c: Coincident(g7,g6)
    c: Tangent(g0,g7)
    c: DistanceX(g5,g5) = 20
    c: DistanceX(g0,g0) = 11
    c: DistanceY(g6,g6) = 14
FEATURE [Sketcher::SketchObject] Sketch002
  FullyConstrained = true
  MapMode = 5
  Placement = pos=(0,25,0) rot=(0,0.707107,0.707107;3.14159rad)
  sketch-geometry (8):
    g0: LineSegment StartX=-38 StartY=58 StartZ=0 EndX=-38 EndY=22 EndZ=0
    g1: LineSegment StartX=-38 StartY=22 StartZ=0 EndX=-6 EndY=22 EndZ=0
    g2: Circle CenterX=-38 CenterY=58 CenterZ=0 NormalX=0 NormalY=0 NormalZ=1 AngleXU=0 Radius=2.1
    g3: Circle CenterX=-38 CenterY=22 CenterZ=0 NormalX=0 NormalY=0 NormalZ=1 AngleXU=0 Radius=0
    g4: Circle CenterX=-6 CenterY=22 CenterZ=0 NormalX=0 NormalY=0 NormalZ=1 AngleXU=0 Radius=2.1
    g5: Circle CenterX=-6 CenterY=58 CenterZ=0 NormalX=0 NormalY=0 NormalZ=1 AngleXU=0 Radius=2.1
    g6: LineSegment StartX=-38 StartY=58 StartZ=0 EndX=-6 EndY=58 EndZ=0
    g7: Circle CenterX=-38 CenterY=22 CenterZ=0 NormalX=0 NormalY=0 NormalZ=1 AngleXU=0 Radius=2.1
  constraints (20):
    c: Vertical(g0)
    c: Coincident(g1,g0)
    c: Horizontal(g1)
    c: Coincident(g2,g0)
    c: Coincident(g3,g0)
    c: Tangent(g3,g1)
    c: Coincident(g4,g1)
    c: Coincident(g6,g0)
    c: Coincident(g6,g5)
    c: Coincident(g7,g0)
    c: Equal(g2,g7)
    c: Equal(g2,g5)
    c: Equal(g2,g4)
    c: Radius(g2) = 2.1
    c: Horizontal(g5,g0)
    c: DistanceY(g0,g0) = 36
    c: Equal(g6,g1)
    c: DistanceX(g1,g1) = 32
    c: DistanceX(g1,g-1) = 6
    c: DistanceY(g-1,g1) = 22
FEATURE [PartDesign::CoordinateSystem] LCS_Pattino_20
  AttacherType = Attacher::AttachEngine3D
  MapMode = 1
FEATURE [PartDesign::Pad] Pad
  Direction = (0,0,1)
  Length = 80
  Length2 = 10
  Profile = -> Sketch
  ReferenceAxis = -> Sketch [N_Axis]
  Type = 0
FEATURE [PartDesign::Body] Body
  Group = -> [Sketch,Sketch002,Pad,LCS_Pattino_20]
  Origin = -> Origin
  Tip = -> Pad
---- part ../PiastraAvanzamentoCarro.FCStd = doc fcstd_e13bda5dda26 ----
FCSTD DOCUMENT  (FreeCAD 0.21R33771 (Git))
Label: PiastraAvanzamentoCarro
License: All rights reserved
LicenseURL: http://en.wikipedia.org/wiki/All_rights_reserved
objects: Part::FeaturePython×4, Sketcher::SketchObject×3, PartDesign::Pad×1, PartDesign::Pocket×1, PartDesign::CoordinateSystem×1, PartDesign::Body×1, App::DocumentObjectGroup×1
note: 13 computed .brp shape members not serialized (recipe doc carries the construction recipe); baked Part::Feature solids carry a one-line shape summary decoded from their .brp

FEATURE [Sketcher::SketchObject] Sketch
  FullyConstrained = true
  MapMode = 5
  Support = -> [XY_Plane]
  sketch-geometry (4):
    g0: LineSegment StartX=-75 StartY=65 StartZ=0 EndX=75 EndY=65 EndZ=0
    g1: LineSegment StartX=75 StartY=65 StartZ=0 EndX=75 EndY=-65 EndZ=0
    g2: LineSegment StartX=75 StartY=-65 StartZ=0 EndX=-75 EndY=-65 EndZ=0
    g3: LineSegment StartX=-75 StartY=-65 StartZ=0 EndX=-75 EndY=65 EndZ=0
  constraints (10):
    c: Coincident(g0,g1)
    c: Coincident(g1,g2)
    c: Coincident(g2,g3)
    c: Coincident(g3,g0)
    c: Horizontal(g0)
    c: Vertical(g1)
    c: Symmetric(g0,g2,g-1)
    c: Symmetric(g2,g1,g-2)
    c: DistanceX(g0,g0) = 150
    c: DistanceY(g1,g1) = 130
FEATURE [PartDesign::Pad] Pad
  Direction = (0,0,1)
  Length = 10
  Length2 = 10
  Profile = -> Sketch
  ReferenceAxis = -> Sketch [N_Axis]
  Type = 0
FEATURE [Sketcher::SketchObject] Sketch001
  FullyConstrained = true
  MapMode = 5
  Placement = pos=(0,0,10) rot=(0,0,1;0rad)
  Support = -> [Pad]
  sketch-geometry (2):
    g0: Circle CenterX=23 CenterY=21 CenterZ=0 NormalX=0 NormalY=0 NormalZ=1 AngleXU=0 Radius=6
    g1: Circle CenterX=-26 CenterY=-10 CenterZ=0 NormalX=0 NormalY=0 NormalZ=1 AngleXU=0 Radius=6
  constraints (6):
    c: DistanceY(g-1,g0) = 21
    c: Radius(g0) = 6
    c: DistanceX(g-1,g0) = 23
    c: Radius(g1) = 6
    c: DistanceY(g1,g-1) = 10
    c: DistanceX(g1,g-1) = 26
FEATURE [PartDesign::Pocket] Pocket
  BaseFeature = -> Pad
  Direction = (0,0,-1)
  Length = 5
  Length2 = 5
  Profile = -> Sketch001
  ReferenceAxis = -> Sketch001 [N_Axis]
  Type = 1
FEATURE [PartDesign::CoordinateSystem] LCS_PiastraAvanzamentoUtensile  label="LCS_PiastraAvanzamentoCarro"
  AttacherType = Attacher::AttachEngine3D
FEATURE [Sketcher::SketchObject] Sketch003
  FullyConstrained = false
  MapMode = 5
  Placement = pos=(0,65,0) rot=(0,0.707107,0.707107;3.14159rad)
  sketch-geometry (3):
    g0: LineSegment StartX=-82.8492 StartY=5 StartZ=0 EndX=128.855 EndY=5 EndZ=0
    g1: Circle CenterX=-50 CenterY=5 CenterZ=0 NormalX=0 NormalY=0 NormalZ=1 AngleXU=0 Radius=3
    g2: Circle CenterX=50 CenterY=5 CenterZ=0 NormalX=0 NormalY=0 NormalZ=1 AngleXU=0 Radius=3
  constraints (7):
    c: Horizontal(g0)
    c: DistanceY(g-1,g0) = 5
    c: PointOnObject(g1,g0)
    c: Equal(g1,g2)
    c: Radius(g1) = 3
    c: Symmetric(g1,g2,g-2)
    c: DistanceX(g1,g2) = 100
FEATURE [PartDesign::Body] Body  label="Corpo"
  Group = -> [Sketch,Pad,Sketch001,Pocket,LCS_PiastraAvanzamentoUtensile,Sketch003]
  Origin = -> Origin
  Tip = -> Pocket
FEATURE [Part::FeaturePython] PtS  # WARN: FeaturePython — macro-defined, semantics opaque (R4)
FEATURE [Part::FeaturePython] PtS001  # WARN: FeaturePython — macro-defined, semantics opaque (R4)
FEATURE [Part::FeaturePython] PtS002  # WARN: FeaturePython — macro-defined, semantics opaque (R4)
FEATURE [Part::FeaturePython] PtS003  # WARN: FeaturePython — macro-defined, semantics opaque (R4)
FEATURE [App::DocumentObjectGroup] Measures
  Group = -> [PtS,PtS001,PtS002,PtS003]
---- part ../PiastraCarroUtensile.FCStd = doc fcstd_eb555b77a075 ----
FCSTD DOCUMENT  (FreeCAD 0.21R33771 (Git))
Label: PiastraCarroUtensile
License: All rights reserved
LicenseURL: http://en.wikipedia.org/wiki/All_rights_reserved
objects: Sketcher::SketchObject×3, PartDesign::Pocket×2, PartDesign::Pad×1, PartDesign::CoordinateSystem×1, PartDesign::Body×1
note: 11 computed .brp shape members not serialized (recipe doc carries the construction recipe); baked Part::Feature solids carry a one-line shape summary decoded from their .brp

FEATURE [Sketcher::SketchObject] Sketch
  FullyConstrained = true
  MapMode = 5
  Placement = pos=(0,0,0) rot=(1,0,0;1.5708rad)
  Support = -> [XZ_Plane]
  sketch-geometry (4):
    g0: LineSegment StartX=0 StartY=0 StartZ=0 EndX=130 EndY=0 EndZ=0
    g1: LineSegment StartX=130 StartY=0 StartZ=0 EndX=130 EndY=300 EndZ=0
    g2: LineSegment StartX=130 StartY=300 StartZ=0 EndX=0 EndY=300 EndZ=0
    g3: LineSegment StartX=0 StartY=300 StartZ=0 EndX=0 EndY=0 EndZ=0
  constraints (11):
    c: Coincident(g0,g1)
    c: Coincident(g1,g2)
    c: Coincident(g2,g3)
    c: Coincident(g3,g0)
    c: Horizontal(g0)
    c: Horizontal(g2)
    c: Vertical(g1)
    c: Vertical(g3)
    c: Coincident(g0,g-1)
    c: DistanceX(g0,g0) = 130
    c: DistanceY(g3,g3) = 300
FEATURE [PartDesign::Pad] Pad
  Direction = (0,-1,-2e-16)
  Length = 15
  Length2 = 100
  Placement = pos=(0,0,0) rot=(1,0,0;1.5708rad)
  Profile = -> Sketch
  ReferenceAxis = -> Sketch [N_Axis]
  Type = 0
FEATURE [Sketcher::SketchObject] Sketch001
  FullyConstrained = false
  MapMode = 5
  Placement = pos=(0,-15,0) rot=(1,0,0;1.5708rad)
  Support = -> [Pad]
  sketch-geometry (31):
    g0: Circle CenterX=5 CenterY=280 CenterZ=0 NormalX=0 NormalY=0 NormalZ=1 AngleXU=0 Radius=2.1
    g1: Circle CenterX=41 CenterY=280 CenterZ=0 NormalX=0 NormalY=0 NormalZ=1 AngleXU=0 Radius=2.1
    g2: LineSegment StartX=5 StartY=280 StartZ=0 EndX=41 EndY=280 EndZ=0
    g3: Circle CenterX=5 CenterY=248 CenterZ=0 NormalX=0 NormalY=0 NormalZ=1 AngleXU=0 Radius=2.1
    g4: LineSegment StartX=5 StartY=280 StartZ=0 EndX=5 EndY=248 EndZ=0
    g5: Circle CenterX=41 CenterY=248 CenterZ=0 NormalX=0 NormalY=0 NormalZ=1 AngleXU=0 Radius=2.1
    g6: LineSegment StartX=5 StartY=248 StartZ=0 EndX=41 EndY=248 EndZ=0
    g7: Circle CenterX=90 CenterY=280 CenterZ=0 NormalX=0 NormalY=0 NormalZ=1 AngleXU=0 Radius=2.1
    g8: Circle CenterX=126 CenterY=280 CenterZ=0 NormalX=0 NormalY=0 NormalZ=1 AngleXU=0 Radius=2.1
    g9: LineSegment StartX=90 StartY=280 StartZ=0 EndX=126 EndY=280 EndZ=0
    g10: Circle CenterX=90 CenterY=248 CenterZ=0 NormalX=0 NormalY=0 NormalZ=1 AngleXU=0 Radius=2.1
    g11: LineSegment StartX=90 StartY=280 StartZ=0 EndX=90 EndY=248 EndZ=0
    g12: Circle CenterX=126 CenterY=248 CenterZ=0 NormalX=0 NormalY=0 NormalZ=1 AngleXU=0 Radius=2.1
    g13: LineSegment StartX=90 StartY=248 StartZ=0 EndX=126 EndY=248 EndZ=0
    g14: LineSegment StartX=5 StartY=280 StartZ=0 EndX=90 EndY=280 EndZ=0
    g15: Circle CenterX=5 CenterY=90 CenterZ=0 NormalX=0 NormalY=0 NormalZ=1 AngleXU=0 Radius=2.1
    g16: Circle CenterX=41 CenterY=90 CenterZ=0 NormalX=0 NormalY=0 NormalZ=1 AngleXU=0 Radius=2.1
    g17: LineSegment StartX=5 StartY=90 StartZ=0 EndX=41 EndY=90 EndZ=0
    g18: Circle CenterX=5 CenterY=58 CenterZ=0 NormalX=0 NormalY=0 NormalZ=1 AngleXU=0 Radius=2.1
    g19: LineSegment StartX=5 StartY=90 StartZ=0 EndX=5 EndY=58 EndZ=0
    g20: Circle CenterX=41 CenterY=58 CenterZ=0 NormalX=0 NormalY=0 NormalZ=1 AngleXU=0 Radius=2.1
    g21: LineSegment StartX=5 StartY=58 StartZ=0 EndX=41 EndY=58 EndZ=0
    g22: LineSegment StartX=5 StartY=280 StartZ=0 EndX=5 EndY=90 EndZ=0
    g23: Circle CenterX=90 CenterY=90 CenterZ=0 NormalX=0 NormalY=0 NormalZ=1 AngleXU=0 Radius=2.1
    g24: Circle CenterX=126 CenterY=90 CenterZ=0 NormalX=0 NormalY=0 NormalZ=1 AngleXU=0 Radius=2.1
    g25: LineSegment StartX=90 StartY=90 StartZ=0 EndX=126 EndY=90 EndZ=0
    g26: Circle CenterX=90 CenterY=58 CenterZ=0 NormalX=0 NormalY=0 NormalZ=1 AngleXU=0 Radius=2.1
    g27: LineSegment StartX=90 StartY=90 StartZ=0 EndX=90 EndY=58 EndZ=0
    g28: Circle CenterX=126 CenterY=58 CenterZ=0 NormalX=0 NormalY=0 NormalZ=1 AngleXU=0 Radius=2.1
    g29: LineSegment StartX=90 StartY=58 StartZ=0 EndX=126 EndY=58 EndZ=0
    g30: LineSegment StartX=5 StartY=90 StartZ=0 EndX=90 EndY=90 EndZ=0
  constraints (77):
    c: Coincident(g0,g2)
    c: Coincident(g1,g2)
    c: Distance(g2) = 36
    c: Angle(g2) = 0
    c: Coincident(g0,g4)
    c: Coincident(g3,g4)
    c: Distance(g4) = 32
    c: Perpendicular(g4,g2)
    c: Coincident(g3,g6)
    c: Coincident(g5,g6)
    c: Equal(g2,g6)
    c: Parallel(g6,g2)
    c: Coincident(g7,g9)
    c: Coincident(g8,g9)
    c: Distance(g9) = 36
    c: Angle(g9) = 0
    c: Coincident(g7,g11)
    c: Coincident(g10,g11)
    c: Distance(g11) = 32
    c: Perpendicular(g11,g9)
    c: Coincident(g10,g13)
    c: Coincident(g12,g13)
    c: Equal(g9,g13)
    c: Parallel(g13,g9)
    c: Coincident(g0,g14)
    c: Coincident(g7,g14)
    c: Distance(g14) = 85
    c: Angle(g14) = 0
    c: Coincident(g15,g17)
    c: Coincident(g16,g17)
    c: Distance(g17) = 36
    c: Angle(g17) = 0
    c: Coincident(g15,g19)
    c: Coincident(g18,g19)
    c: Distance(g19) = 32
    c: Perpendicular(g19,g17)
    c: Coincident(g18,g21)
    c: Coincident(g20,g21)
    c: Equal(g17,g21)
    c: Parallel(g21,g17)
    c: Coincident(g0,g22)
    c: Coincident(g15,g22)
    c: Distance(g22) = 190
    c: Perpendicular(g22,g14)
    c: Coincident(g23,g25)
    c: Coincident(g24,g25)
    c: Distance(g25) = 36
    c: Angle(g25) = 0
    c: Coincident(g23,g27)
    c: Coincident(g26,g27)
    c: Perpendicular(g27,g25)
    c: Coincident(g26,g29)
    c: Coincident(g28,g29)
    c: Equal(g25,g29)
    c: Parallel(g29,g25)
    c: Coincident(g15,g30)
    c: Coincident(g23,g30)
    c: Equal(g14,g30)
    c: Parallel(g30,g14)
    c: DistanceY(g-1,g0) = 280
    c: DistanceX(g-1,g0) = 5
    c: Radius(g0) = 2.1
    c: Equal(g3,g0)
    c: Equal(g0,g1)
    c: Equal(g1,g5)
    c: Equal(g5,g10)
    c: Equal(g10,g12)
    c: Equal(g12,g8)
    c: Equal(g8,g7)
    c: Equal(g16,g23)
    c: Equal(g23,g24)
    c: Equal(g24,g18)
    c: Equal(g18,g20)
    c: Equal(g15,g16)
    c: Equal(g24,g28)
    c: Equal(g28,g26)
    c: Equal(g27,g19)
FEATURE [PartDesign::Pocket] Pocket
  BaseFeature = -> Pad
  Direction = (0,1,-2e-16)
  Length = 0
  Length2 = 100
  Placement = pos=(0,0,0) rot=(1,0,0;1.5708rad)
  Profile = -> Sketch001
  Type = 1
FEATURE [Sketcher::SketchObject] Sketch002
  FullyConstrained = false
  MapMode = 5
  Placement = pos=(0,-15,0) rot=(1,0,0;1.5708rad)
  Support = -> [Pocket]
  sketch-geometry (13):
    g0: LineSegment StartX=9 StartY=100 StartZ=0 EndX=121 EndY=100 EndZ=0
    g1: Circle CenterX=9 CenterY=100 CenterZ=0 NormalX=0 NormalY=0 NormalZ=1 AngleXU=0 Radius=3
    g2: Circle CenterX=121 CenterY=100 CenterZ=0 NormalX=0 NormalY=0 NormalZ=1 AngleXU=0 Radius=3
    g3: LineSegment StartX=65 StartY=100 StartZ=0 EndX=65 EndY=175 EndZ=0
    g4: Circle CenterX=65 CenterY=175 CenterZ=0 NormalX=0 NormalY=0 NormalZ=1 AngleXU=0 Radius=4
    g5: Circle CenterX=65 CenterY=100 CenterZ=0 NormalX=0 NormalY=0 NormalZ=1 AngleXU=0 Radius=4
    g6: Circle CenterX=65 CenterY=100 CenterZ=0 NormalX=0 NormalY=0 NormalZ=1 AngleXU=0 Radius=56
    g7: LineSegment StartX=11.6907 StartY=137.328 StartZ=0 EndX=123.11 EndY=59.3109 EndZ=0
    g8: LineSegment StartX=120.653 StartY=138.969 StartZ=0 EndX=8.20799 EndY=60.2338 EndZ=0
    g9: Circle CenterX=19.1275 CenterY=132.12 CenterZ=0 NormalX=0 NormalY=0 NormalZ=1 AngleXU=0 Radius=3
    g10: Circle CenterX=110.873 CenterY=67.8797 CenterZ=0 NormalX=0 NormalY=0 NormalZ=1 AngleXU=0 Radius=3
    g11: Circle CenterX=19.1275 CenterY=67.8797 CenterZ=0 NormalX=0 NormalY=0 NormalZ=1 AngleXU=0 Radius=3
    g12: Circle CenterX=110.873 CenterY=132.12 CenterZ=0 NormalX=0 NormalY=0 NormalZ=1 AngleXU=0 Radius=3
  constraints (33):
    c: DistanceX(g0,g0) = 112
    c: Coincident(g1,g0)
    c: Coincident(g2,g0)
    c: Radius(g1) = 3
    c: Equal(g1,g2)
    c: DistanceY(g-1,g2) = 100
    c: PointOnObject(g3,g0)
    c: DistanceY(g3,g3) = 75
    c: Coincident(g4,g3)
    c: Radius(g4) = 4
    c: Coincident(g5,g3)
    c: Vertical(g3)
    c: Symmetric(g1,g2,g3)
    c: Radius(g5) = 4
    c: DistanceX(g-1,g5) = 65
    c: Coincident(g6,g5)
    c: PointOnObject(g2,g6)
    c: PointOnObject(g9,g6)
    c: PointOnObject(g10,g6)
    c: PointOnObject(g11,g6)
    c: PointOnObject(g12,g6)
    c: PointOnObject(g12,g8)
    c: PointOnObject(g11,g8)
    c: PointOnObject(g9,g7)
    c: PointOnObject(g10,g7)
    c: PointOnObject(g5,g7)
    c: PointOnObject(g5,g8)
    c: Radius(g9) = 3
    c: Equal(g9,g12)
    c: Equal(g12,g10)
    c: Equal(g10,g11)
    c: Angle(g7,g0) = 0.610865
    c: Angle(g8,g0) = 2.53073
FEATURE [PartDesign::Pocket] Pocket001
  BaseFeature = -> Pocket
  Direction = (0,1,-2e-16)
  Length = 5
  Length2 = 5
  Placement = pos=(0,0,0) rot=(1,0,0;1.5708rad)
  Profile = -> Sketch002
  ReferenceAxis = -> Sketch002 [N_Axis]
  Type = 1
FEATURE [PartDesign::CoordinateSystem] LCS_PiastraCarro
  AttacherType = Attacher::AttachEngine3D
  MapMode = 11
  Placement = pos=(65,-15,100) rot=(0.57735,-0.57735,0.57735;2.0944rad)
  Support = -> [Pocket001]
FEATURE [PartDesign::Body] Body
  Group = -> [Sketch,Pad,Sketch001,Pocket,LCS_PiastraCarro,Sketch002,Pocket001]
  Origin = -> Origin
  Tip = -> Pocket001
---- part ../PiastraTorretta.FCStd = doc fcstd_b43e1461e32a ----
FCSTD DOCUMENT  (FreeCAD 0.21R33771 (Git))
Label: PiastraTorretta
License: All rights reserved
LicenseURL: https://en.wikipedia.org/wiki/All_rights_reserved
objects: Sketcher::SketchObject×2, PartDesign::Pad×1, PartDesign::Pocket×1, PartDesign::CoordinateSystem×1, PartDesign::Body×1
note: 8 computed .brp shape members not serialized (recipe doc carries the construction recipe); baked Part::Feature solids carry a one-line shape summary decoded from their .brp

FEATURE [Sketcher::SketchObject] Sketch
  FullyConstrained = true
  MapMode = 5
  Support = -> [XY_Plane]
  sketch-geometry (4):
    g0: LineSegment StartX=-47.5 StartY=40 StartZ=0 EndX=47.5 EndY=40 EndZ=0
    g1: LineSegment StartX=47.5 StartY=40 StartZ=0 EndX=47.5 EndY=-40 EndZ=0
    g2: LineSegment StartX=47.5 StartY=-40 StartZ=0 EndX=-47.5 EndY=-40 EndZ=0
    g3: LineSegment StartX=-47.5 StartY=-40 StartZ=0 EndX=-47.5 EndY=40 EndZ=0
  constraints (10):
    c: Coincident(g0,g1)
    c: Coincident(g1,g2)
    c: Coincident(g2,g3)
    c: Coincident(g3,g0)
    c: Horizontal(g0)
    c: Vertical(g1)
    c: Symmetric(g2,g1,g-2)
    c: Symmetric(g0,g2,g-1)
    c: DistanceX(g2,g2) = 95
    c: DistanceY(g3,g3) = 80
FEATURE [PartDesign::Pad] Pad
  Direction = (0,0,1)
  Length = 8
  Length2 = 10
  Profile = -> Sketch
  ReferenceAxis = -> Sketch [N_Axis]
  Type = 0
FEATURE [Sketcher::SketchObject] Sketch001
  ExternalGeometry = -> [Pad]
  FullyConstrained = true
  MapMode = 5
  Placement = pos=(0,0,8) rot=(0,0,1;0rad)
  Support = -> [Pad]
  sketch-geometry (21):
    g0: LineSegment StartX=-43 StartY=25 StartZ=0 EndX=-17 EndY=25 EndZ=0
    g1: LineSegment StartX=-17 StartY=25 StartZ=0 EndX=-17 EndY=-9 EndZ=0
    g2: LineSegment StartX=-17 StartY=-9 StartZ=0 EndX=-43 EndY=-9 EndZ=0
    g3: LineSegment StartX=-43 StartY=-9 StartZ=0 EndX=-43 EndY=25 EndZ=0
    g4: Circle CenterX=-43 CenterY=25 CenterZ=0 NormalX=0 NormalY=0 NormalZ=1 AngleXU=0 Radius=1.5
    g5: Circle CenterX=-17 CenterY=25 CenterZ=0 NormalX=0 NormalY=0 NormalZ=1 AngleXU=0 Radius=1.5
    g6: Circle CenterX=-17 CenterY=-9 CenterZ=0 NormalX=0 NormalY=0 NormalZ=1 AngleXU=0 Radius=1.5
    g7: Circle CenterX=-43 CenterY=-9 CenterZ=0 NormalX=0 NormalY=0 NormalZ=1 AngleXU=0 Radius=1.5
    g8: LineSegment StartX=17 StartY=25 StartZ=0 EndX=43 EndY=25 EndZ=0
    g9: LineSegment StartX=43 StartY=25 StartZ=0 EndX=43 EndY=-9 EndZ=0
    g10: LineSegment StartX=43 StartY=-9 StartZ=0 EndX=17 EndY=-9 EndZ=0
    g11: LineSegment StartX=17 StartY=-9 StartZ=0 EndX=17 EndY=25 EndZ=0
    g12: Circle CenterX=17 CenterY=25 CenterZ=0 NormalX=0 NormalY=0 NormalZ=1 AngleXU=0 Radius=1.5
    g13: Circle CenterX=43 CenterY=25 CenterZ=0 NormalX=0 NormalY=0 NormalZ=1 AngleXU=0 Radius=1.5
    g14: Circle CenterX=43 CenterY=-9 CenterZ=0 NormalX=0 NormalY=0 NormalZ=1 AngleXU=0 Radius=1.5
    g15: Circle CenterX=17 CenterY=-9 CenterZ=0 NormalX=0 NormalY=0 NormalZ=1 AngleXU=0 Radius=1.5
    g16: LineSegment StartX=-43 StartY=25 StartZ=0 EndX=17 EndY=25 EndZ=0
    g17: LineSegment StartX=-11 StartY=-31.5 StartZ=0 EndX=11 EndY=-31.5 EndZ=0
    g18: LineSegment StartX=11 StartY=-31.5 StartZ=0 EndX=11 EndY=-40 EndZ=0
    g19: LineSegment StartX=11 StartY=-40 StartZ=0 EndX=-11 EndY=-40 EndZ=0
    g20: LineSegment StartX=-11 StartY=-40 StartZ=0 EndX=-11 EndY=-31.5 EndZ=0
  constraints (52):
    c: Horizontal(g0)
    c: Coincident(g1,g0)
    c: Vertical(g1)
    c: Coincident(g2,g1)
    c: Horizontal(g2)
    c: Coincident(g3,g2)
    c: Coincident(g3,g0)
    c: Vertical(g3)
    c: Coincident(g4,g0)
    c: Coincident(g5,g0)
    c: Coincident(g6,g1)
    c: Coincident(g7,g2)
    c: Radius(g4) = 1.5
    c: Equal(g4,g5)
    c: Equal(g5,g6)
    c: Equal(g6,g7)
    c: DistanceY(g3,g3) = 34
    c: DistanceX(g2,g2) = 26
    c: Horizontal(g8)
    c: Coincident(g9,g8)
    c: Vertical(g9)
    c: Coincident(g10,g9)
    c: Horizontal(g10)
    c: Coincident(g11,g10)
    c: Coincident(g11,g8)
    c: Vertical(g11)
    c: Coincident(g12,g8)
    c: Coincident(g13,g8)
    c: Coincident(g14,g9)
    c: Coincident(g15,g10)
    c: Radius(g12) = 1.5
    c: Equal(g12,g13)
    c: Equal(g13,g14)
    c: Equal(g14,g15)
    c: DistanceY(g11,g11) = 34
    c: DistanceX(g10,g10) = 26
    c: Coincident(g0,g16)
    c: Coincident(g8,g16)
    c: Coincident(g17,g18)
    c: Coincident(g18,g19)
    c: Coincident(g19,g20)
    c: Coincident(g20,g17)
    c: Horizontal(g17)
    c: Vertical(g18)
    c: Vertical(g20)
    c: DistanceX(g19,g19) = 22
    c: DistanceY(g18,g18) = 8.5
    c: Symmetric(g19,g18,g-2)
    c: PointOnObject(g19,g-3)
    c: DistanceX(g5,g-1) = 17
    c: Symmetric(g5,g12,g-2)
    c: DistanceY(g-1,g5) = 25
FEATURE [PartDesign::Pocket] Pocket
  BaseFeature = -> Pad
  Direction = (0,0,-1)
  Length = 6
  Length2 = 5
  Profile = -> Sketch001
  ReferenceAxis = -> Sketch001 [N_Axis]
  Type = 1
FEATURE [PartDesign::CoordinateSystem] LCS_PiastraTorretta
  AttacherType = Attacher::AttachEngine3D
FEATURE [PartDesign::Body] Body
  Group = -> [Sketch,Pad,Sketch001,Pocket,LCS_PiastraTorretta]
  Origin = -> Origin
  Tip = -> Pocket
---- part ../Piatto40x10x850.FCStd = doc fcstd_723a337a0be8 ----
FCSTD DOCUMENT  (FreeCAD 0.21R33771 (Git))
Label: Piatto40x10x850
License: All rights reserved
LicenseURL: http://en.wikipedia.org/wiki/All_rights_reserved
objects: Sketcher::SketchObject×3, PartDesign::Pocket×2, PartDesign::Pad×1, PartDesign::CoordinateSystem×1, PartDesign::Body×1
note: 11 computed .brp shape members not serialized (recipe doc carries the construction recipe); baked Part::Feature solids carry a one-line shape summary decoded from their .brp

FEATURE [Sketcher::SketchObject] Sketch
  FullyConstrained = true
  MapMode = 5
  Support = -> [XY_Plane]
  sketch-geometry (4):
    g0: LineSegment StartX=0 StartY=0 StartZ=0 EndX=10 EndY=0 EndZ=0
    g1: LineSegment StartX=10 StartY=0 StartZ=0 EndX=10 EndY=40 EndZ=0
    g2: LineSegment StartX=10 StartY=40 StartZ=0 EndX=0 EndY=40 EndZ=0
    g3: LineSegment StartX=0 StartY=40 StartZ=0 EndX=0 EndY=0 EndZ=0
  constraints (11):
    c: Coincident(g0,g1)
    c: Coincident(g1,g2)
    c: Coincident(g2,g3)
    c: Coincident(g3,g0)
    c: Horizontal(g0)
    c: Horizontal(g2)
    c: Vertical(g1)
    c: Vertical(g3)
    c: Coincident(g0,g-1)
    c: DistanceX(g2,g2) = 10
    c: DistanceY(g3,g3) = 40
FEATURE [PartDesign::Pad] Pad
  Direction = (0,0,1)
  Length = 850
  Length2 = 10
  Profile = -> Sketch
  ReferenceAxis = -> Sketch [N_Axis]
  Type = 0
FEATURE [PartDesign::CoordinateSystem] LCS_Piatto40x10
  AttacherType = Attacher::AttachEngine3D
FEATURE [Sketcher::SketchObject] Sketch001
  FullyConstrained = false
  MapMode = 5
  Placement = pos=(0,0,0) rot=(0.57735,-0.57735,-0.57735;2.0944rad)
  Support = -> [Pad]
  sketch-geometry (4):
    g0: LineSegment StartX=-20 StartY=902.961 StartZ=0 EndX=-20 EndY=-51.8905 EndZ=0
    g1: Circle CenterX=-20 CenterY=50 CenterZ=0 NormalX=0 NormalY=0 NormalZ=1 AngleXU=0 Radius=6
    g2: Circle CenterX=-20 CenterY=425 CenterZ=0 NormalX=0 NormalY=0 NormalZ=1 AngleXU=0 Radius=6
    g3: Circle CenterX=-20 CenterY=800 CenterZ=0 NormalX=0 NormalY=0 NormalZ=1 AngleXU=0 Radius=6
  constraints (11):
    c: Vertical(g0)
    c: DistanceX(g0,g-1) = 20
    c: PointOnObject(g1,g0)
    c: PointOnObject(g2,g0)
    c: PointOnObject(g3,g0)
    c: Equal(g1,g2)
    c: Equal(g1,g3)
    c: Radius(g1) = 6
    c: DistanceY(g-1,g1) = 50
    c: DistanceY(g-1,g2) = 425
    c: DistanceY(g-1,g3) = 800
FEATURE [PartDesign::Pocket] Pocket
  BaseFeature = -> Pad
  Direction = (1,0,0)
  Length = 5
  Length2 = 5
  Profile = -> Sketch001
  ReferenceAxis = -> Sketch001 [N_Axis]
  Type = 1
FEATURE [Sketcher::SketchObject] Sketch002
  ExternalGeometry = -> [Pocket]
  FullyConstrained = true
  MapMode = 5
  Placement = pos=(10,0,0) rot=(0.57735,0.57735,0.57735;2.0944rad)
  Support = -> [Pocket]
  sketch-geometry (3):
    g0: Circle CenterX=20 CenterY=800 CenterZ=0 NormalX=0 NormalY=0 NormalZ=1 AngleXU=0 Radius=9
    g1: Circle CenterX=20 CenterY=425 CenterZ=0 NormalX=0 NormalY=0 NormalZ=1 AngleXU=0 Radius=9
    g2: Circle CenterX=20 CenterY=50 CenterZ=0 NormalX=0 NormalY=0 NormalZ=1 AngleXU=0 Radius=9
  constraints (6):
    c: Coincident(g0,g-3)
    c: Coincident(g1,g-4)
    c: Coincident(g2,g-5)
    c: Equal(g2,g1)
    c: Equal(g2,g0)
    c: Radius(g2) = 9
FEATURE [PartDesign::Pocket] Pocket001
  BaseFeature = -> Pocket
  Direction = (-1,0,0)
  Length = 6
  Length2 = 5
  Profile = -> Sketch002
  ReferenceAxis = -> Sketch002 [N_Axis]
  Type = 0
FEATURE [PartDesign::Body] Body  label="Corpo"
  Group = -> [Sketch,Pad,LCS_Piatto40x10,Sketch001,Pocket,Sketch002,Pocket001]
  Origin = -> Origin
  Tip = -> Pocket001
---- part ../Piedino40x40.FCStd = doc fcstd_83c0320ab840 ----
FCSTD DOCUMENT  (FreeCAD 0.21R33771 (Git))
Label: Piedino40x40
License: All rights reserved
LicenseURL: http://en.wikipedia.org/wiki/All_rights_reserved
objects: Sketcher::SketchObject×1, PartDesign::Pad×1, PartDesign::CoordinateSystem×1, PartDesign::Body×1
note: 5 computed .brp shape members not serialized (recipe doc carries the construction recipe); baked Part::Feature solids carry a one-line shape summary decoded from their .brp

FEATURE [Sketcher::SketchObject] Sketch
  FullyConstrained = true
  MapMode = 5
  Support = -> [XY_Plane]
  sketch-geometry (8):
    g0: LineSegment StartX=40 StartY=40 StartZ=0 EndX=0 EndY=40 EndZ=0
    g1: LineSegment StartX=0 StartY=40 StartZ=0 EndX=0 EndY=0 EndZ=0
    g2: LineSegment StartX=0 StartY=0 StartZ=0 EndX=40 EndY=0 EndZ=0
    g3: LineSegment StartX=40 StartY=0 StartZ=0 EndX=40 EndY=40 EndZ=0
    g4: LineSegment StartX=3 StartY=37 StartZ=0 EndX=37 EndY=37 EndZ=0
    g5: LineSegment StartX=37 StartY=37 StartZ=0 EndX=37 EndY=3 EndZ=0
    g6: LineSegment StartX=37 StartY=3 StartZ=0 EndX=3 EndY=3 EndZ=0
    g7: LineSegment StartX=3 StartY=3 StartZ=0 EndX=3 EndY=37 EndZ=0
  constraints (23):
    c: Coincident(g0,g1)
    c: Coincident(g1,g2)
    c: Coincident(g2,g3)
    c: Coincident(g3,g0)
    c: Horizontal(g0)
    c: Horizontal(g2)
    c: Vertical(g1)
    c: Vertical(g3)
    c: Coincident(g1,g-1)
    c: DistanceX(g0,g0) = 40
    c: DistanceY(g1,g1) = 40
    c: Coincident(g4,g5)
    c: Coincident(g5,g6)
    c: Coincident(g6,g7)
    c: Coincident(g7,g4)
    c: Horizontal(g4)
    c: Horizontal(g6)
    c: Vertical(g5)
    c: Vertical(g7)
    c: DistanceX(g6,g6) = 34
    c: DistanceY(g5,g5) = 34
    c: DistanceY(g1,g6) = 3
    c: DistanceX(g1,g6) = 3
FEATURE [PartDesign::Pad] Pad
  Direction = (0,0,1)
  Length = 150
  Length2 = 10
  Profile = -> Sketch
  ReferenceAxis = -> Sketch [N_Axis]
  Type = 0
FEATURE [PartDesign::CoordinateSystem] LCS_piedino40x40
  AttacherType = Attacher::AttachEngine3D
FEATURE [PartDesign::Body] Body  label="Corpo"
  Group = -> [Sketch,Pad,LCS_piedino40x40]
  Origin = -> Origin
  Tip = -> Pad
---- part ../Profilo-C-basamento.FCStd = doc fcstd_f968203fe7b7 ----
FCSTD DOCUMENT  (FreeCAD 0.21R33771 (Git))
Label: Profilo-C-basamento
License: All rights reserved
LicenseURL: http://en.wikipedia.org/wiki/All_rights_reserved
objects: Sketcher::SketchObject×2, PartDesign::Pad×1, PartDesign::CoordinateSystem×1, PartDesign::Pocket×1, PartDesign::Body×1
note: 8 computed .brp shape members not serialized (recipe doc carries the construction recipe); baked Part::Feature solids carry a one-line shape summary decoded from their .brp

FEATURE [Sketcher::SketchObject] Sketch
  FullyConstrained = true
  MapMode = 5
  Support = -> [XY_Plane]
  sketch-geometry (12):
    g0: LineSegment StartX=0 StartY=0 StartZ=0 EndX=0 EndY=45 EndZ=0
    g1: LineSegment StartX=0 StartY=45 StartZ=0 EndX=80 EndY=45 EndZ=0
    g2: LineSegment StartX=80 StartY=45 StartZ=0 EndX=80 EndY=0 EndZ=0
    g3: LineSegment StartX=80 StartY=0 StartZ=0 EndX=78 EndY=0 EndZ=0
    g4: LineSegment StartX=75.0114 StartY=2.73853 StartZ=0 EndX=72.4379 EndY=32.1537 EndZ=0
    g5: LineSegment StartX=0 StartY=0 StartZ=0 EndX=2 EndY=0 EndZ=0
    g6: LineSegment StartX=4.98858 StartY=2.73853 StartZ=0 EndX=7.56207 EndY=32.1537 EndZ=0
    g7: LineSegment StartX=64.9665 StartY=39 StartZ=0 EndX=15.0335 EndY=39 EndZ=0
    g8: ArcOfCircle CenterX=64.9665 CenterY=31.5 CenterZ=0 NormalX=0 NormalY=0 NormalZ=1 AngleXU=0 Radius=7.5 StartAngle=0.0872665 EndAngle=1.5708
    g9: ArcOfCircle CenterX=15.0335 CenterY=31.5 CenterZ=0 NormalX=0 NormalY=0 NormalZ=1 AngleXU=0 Radius=7.5 StartAngle=1.5708 EndAngle=3.05433
    g10: ArcOfCircle CenterX=78 CenterY=3 CenterZ=0 NormalX=0 NormalY=0 NormalZ=1 AngleXU=0 Radius=3 StartAngle=3.22886 EndAngle=4.71239
    g11: ArcOfCircle CenterX=2 CenterY=3 CenterZ=0 NormalX=0 NormalY=0 NormalZ=1 AngleXU=0 Radius=3 StartAngle=4.71239 EndAngle=6.19592
  constraints (31):
    c: Coincident(g0,g-1)
    c: PointOnObject(g0,g-2)
    c: Coincident(g1,g0)
    c: Horizontal(g1)
    c: Coincident(g2,g1)
    c: PointOnObject(g2,g-1)
    c: Vertical(g2)
    c: Coincident(g3,g2)
    c: Coincident(g5,g0)
    c: Horizontal(g7)
    c: DistanceY(g0,g0) = 45
    c: DistanceX(g0,g1) = 80
    c: Angle(g6,g0) = 0.0872665
    c: Angle(g4,g-1) = 1.48353
    c: Equal(g5,g3)
    c: Tangent(g7,g8) = -1.5708
    c: Tangent(g4,g8) = -1.5708
    c: Tangent(g6,g9) = 1.5708
    c: Tangent(g7,g9) = -1.5708
    c: DistanceY(g7,g1) = 6
    c: Equal(g9,g8)
    c: Radius(g9) = 7.5
    c: Tangent(g4,g10) = 1.5708
    c: Tangent(g3,g10) = 1.5708
    c: Radius(g10) = 3
    c: Horizontal(g3)
    c: Tangent(g6,g11) = -1.5708
    c: Tangent(g5,g11) = -1.5708
    c: Equal(g11,g10)
    c: Horizontal(g5)
    c: DistanceX(g3,g3) = 2
FEATURE [PartDesign::Pad] Pad
  Direction = (0,0,1)
  Length = 1100
  Length2 = 10
  Profile = -> Sketch
  ReferenceAxis = -> Sketch [N_Axis]
  Type = 0
FEATURE [PartDesign::CoordinateSystem] LCS_ProfiloCbasamento
  AttacherType = Attacher::AttachEngine3D
FEATURE [Sketcher::SketchObject] Sketch001
  FullyConstrained = true
  MapMode = 5
  Placement = pos=(0,0,0) rot=(0.57735,-0.57735,-0.57735;2.0944rad)
  Support = -> [Pad]
  sketch-geometry (1):
    g0: Circle CenterX=-62 CenterY=1050 CenterZ=0 NormalX=0 NormalY=0 NormalZ=1 AngleXU=0 Radius=6
  constraints (3):
    c: Radius(g0) = 6
    c: DistanceY(g-1,g0) = 1050
    c: DistanceX(g0,g-1) = 62
FEATURE [PartDesign::Pocket] Pocket
  BaseFeature = -> Pad
  Direction = (1,0,0)
  Length = 5
  Length2 = 5
  Profile = -> Sketch001
  ReferenceAxis = -> Sketch001 [N_Axis]
  Type = 1
FEATURE [PartDesign::Body] Body  label="Corpo"
  Group = -> [Sketch,Pad,LCS_ProfiloCbasamento,Sketch001,Pocket]
  Origin = -> Origin
  Tip = -> Pocket
---- part ../Puleggia70-Foro28.FCStd = doc fcstd_1eeae1e5eff7 ----
FCSTD DOCUMENT  (FreeCAD 0.21R33771 (Git))
Label: Puleggia70-Foro28
License: All rights reserved
LicenseURL: http://en.wikipedia.org/wiki/All_rights_reserved
objects: Sketcher::SketchObject×2, PartDesign::Revolution×1, PartDesign::Pocket×1, PartDesign::CoordinateSystem×1, PartDesign::Body×1
note: 8 computed .brp shape members not serialized (recipe doc carries the construction recipe); baked Part::Feature solids carry a one-line shape summary decoded from their .brp

FEATURE [Sketcher::SketchObject] Sketch
  FullyConstrained = true
  MapMode = 5
  Support = -> [XY_Plane]
  sketch-geometry (8):
    g0: LineSegment StartX=-6 StartY=0 StartZ=0 EndX=6 EndY=1e-16 EndZ=0
    g1: LineSegment StartX=6 StartY=1e-16 StartZ=0 EndX=6 EndY=35 EndZ=0
    g2: LineSegment StartX=3.5 StartY=24 StartZ=0 EndX=-3.5 EndY=24 EndZ=0
    g3: LineSegment StartX=-6 StartY=35 StartZ=0 EndX=-6 EndY=0 EndZ=0
    g4: LineSegment StartX=-6 StartY=35 StartZ=0 EndX=-5 EndY=35 EndZ=0
    g5: LineSegment StartX=6 StartY=35 StartZ=0 EndX=5 EndY=35 EndZ=0
    g6: LineSegment StartX=-5 StartY=35 StartZ=0 EndX=-3.5 EndY=24 EndZ=0
    g7: LineSegment StartX=3.5 StartY=24 StartZ=0 EndX=5 EndY=35 EndZ=0
  constraints (22):
    c: PointOnObject(g0,g-1)
    c: Coincident(g1,g0)
    c: Vertical(g1)
    c: Vertical(g3)
    c: Symmetric(g2,g2,g-2)
    c: Symmetric(g0,g3,g-2)
    c: Coincident(g0,g3)
    c: Equal(g1,g3)
    c: DistanceX(g0,g0) = 12
    c: DistanceY(g0,g2) = 24
    c: DistanceX(g2,g2) = 7
    c: Coincident(g4,g3)
    c: Horizontal(g4)
    c: Coincident(g5,g1)
    c: Equal(g4,g5)
    c: Horizontal(g5)
    c: DistanceX(g4,g4) = 1
    c: Coincident(g6,g4)
    c: Coincident(g6,g2)
    c: Coincident(g7,g2)
    c: Coincident(g7,g5)
    c: DistanceY(g3,g3) = 35
FEATURE [PartDesign::Revolution] Revolution
  Angle = 360
  Axis = (1,0,0)
  Base = (0,0,0)
  Profile = -> Sketch
  ReferenceAxis = -> X_Axis
FEATURE [Sketcher::SketchObject] Sketch001
  FullyConstrained = true
  MapMode = 5
  Placement = pos=(-6,0,0) rot=(0.57735,-0.57735,-0.57735;2.0944rad)
  Support = -> [Revolution]
  sketch-geometry (1):
    g0: Circle CenterX=0 CenterY=0 CenterZ=0 NormalX=0 NormalY=0 NormalZ=1 AngleXU=0 Radius=14
  constraints (2):
    c: Coincident(g0,g-1)
    c: Radius(g0) = 14
FEATURE [PartDesign::Pocket] Pocket
  BaseFeature = -> Revolution
  Direction = (1,0,0)
  Length = 5
  Length2 = 5
  Profile = -> Sketch001
  ReferenceAxis = -> Sketch001 [N_Axis]
  Type = 1
FEATURE [PartDesign::CoordinateSystem] LCS_Puleggia70  label="LCS_Puleggia70-D28"
  AttacherType = Attacher::AttachEngine3D
FEATURE [PartDesign::Body] Body  label="Corpo"
  Group = -> [Sketch,Revolution,Sketch001,Pocket,LCS_Puleggia70]
  Origin = -> Origin
  Tip = -> Pocket
---- part ../StaffaChiocciola16x4.FCStd = doc fcstd_ddd312eda095 ----
FCSTD DOCUMENT  (FreeCAD 0.21R33771 (Git))
Label: StaffaChiocciola16x4
License: All rights reserved
LicenseURL: http://en.wikipedia.org/wiki/All_rights_reserved
objects: Sketcher::SketchObject×1, PartDesign::Pad×1, PartDesign::CoordinateSystem×1, PartDesign::Body×1
note: 5 computed .brp shape members not serialized (recipe doc carries the construction recipe); baked Part::Feature solids carry a one-line shape summary decoded from their .brp

FEATURE [Sketcher::SketchObject] Sketch
  FullyConstrained = false
  MapMode = 5
  Support = -> [XY_Plane]
  sketch-geometry (12):
    g0: LineSegment StartX=0 StartY=0 StartZ=0 EndX=75 EndY=0 EndZ=0
    g1: LineSegment StartX=75 StartY=0 StartZ=0 EndX=75 EndY=40 EndZ=0
    g2: LineSegment StartX=75 StartY=40 StartZ=0 EndX=0 EndY=40 EndZ=0
    g3: LineSegment StartX=0 StartY=40 StartZ=0 EndX=0 EndY=0 EndZ=0
    g4: Circle CenterX=55 CenterY=20 CenterZ=0 NormalX=0 NormalY=0 NormalZ=1 AngleXU=0 Radius=12
    g5: Circle CenterX=55 CenterY=20 CenterZ=0 NormalX=0 NormalY=0 NormalZ=1 AngleXU=0 Radius=15.5
    g6: Circle CenterX=65.9602 CenterY=30.9602 CenterZ=0 NormalX=0 NormalY=0 NormalZ=1 AngleXU=0 Radius=2
    g7: Circle CenterX=44.0398 CenterY=30.9602 CenterZ=0 NormalX=0 NormalY=0 NormalZ=1 AngleXU=0 Radius=2
    g8: Circle CenterX=44.0398 CenterY=9.03984 CenterZ=0 NormalX=0 NormalY=0 NormalZ=1 AngleXU=0 Radius=2
    g9: Circle CenterX=65.9602 CenterY=9.03984 CenterZ=0 NormalX=0 NormalY=0 NormalZ=1 AngleXU=0 Radius=2
    g10: LineSegment StartX=84.4263 StartY=-9.42631 StartZ=0 EndX=2.27454 EndY=72.7255 EndZ=0
    g11: LineSegment StartX=67.5573 StartY=32.5573 StartZ=0 EndX=12.7075 EndY=-22.2925 EndZ=0
  constraints (32):
    c: Coincident(g0,g1)
    c: Coincident(g2,g3)
    c: Coincident(g3,g0)
    c: Horizontal(g0)
    c: Horizontal(g2)
    c: Vertical(g1)
    c: Vertical(g3)
    c: Coincident(g0,g-1)
    c: DistanceY(g3,g3) = 40
    c: Radius(g4) = 12
    c: DistanceX(g4,g0) = 20
    c: DistanceY(g0,g4) = 20
    c: Coincident(g5,g4)
    c: PointOnObject(g6,g5)
    c: PointOnObject(g7,g5)
    c: PointOnObject(g8,g5)
    c: PointOnObject(g9,g5)
    c: Equal(g6,g7)
    c: Equal(g7,g8)
    c: Equal(g8,g9)
    c: Radius(g6) = 2
    c: Tangent(g7,g10) = 1.5708
    c: PointOnObject(g4,g10)
    c: PointOnObject(g9,g10)
    c: PointOnObject(g4,g11)
    c: PointOnObject(g6,g11)
    c: PointOnObject(g8,g11)
    c: Radius(g5) = 15.5
    c: Angle(g10,g11) = 1.5708
    c: Angle(g11,g0) = 2.35619
    c: Coincident(g2,g1)
    c: DistanceX(g0,g0) = 75
FEATURE [PartDesign::Pad] Pad
  Direction = (0,0,1)
  Length = 10
  Length2 = 10
  Profile = -> Sketch
  ReferenceAxis = -> Sketch [N_Axis]
  Type = 0
FEATURE [PartDesign::CoordinateSystem] LCS_StaffaChiocciola16x4
  AttacherType = Attacher::AttachEngine3D
FEATURE [PartDesign::Body] Body  label="Corpo"
  Group = -> [Sketch,Pad,LCS_StaffaChiocciola16x4]
  Origin = -> Origin
  Tip = -> Pad
---- part ../SupportoDoppioVite16x4.FCStd = doc fcstd_4a465a95b0ad ----
FCSTD DOCUMENT  (FreeCAD 0.21R33771 (Git))
Label: SupportoDoppioVite16x4
License: All rights reserved
LicenseURL: http://en.wikipedia.org/wiki/All_rights_reserved
objects: Sketcher::SketchObject×2, PartDesign::Pad×1, PartDesign::Pocket×1, PartDesign::CoordinateSystem×1, PartDesign::Body×1
note: 8 computed .brp shape members not serialized (recipe doc carries the construction recipe); baked Part::Feature solids carry a one-line shape summary decoded from their .brp

FEATURE [Sketcher::SketchObject] Sketch
  FullyConstrained = true
  MapMode = 5
  Support = -> [XY_Plane]
  sketch-geometry (9):
    g0: LineSegment StartX=-17 StartY=21.6256 StartZ=0 EndX=17 EndY=21.6256 EndZ=0
    g1: LineSegment StartX=30 StartY=7.5 StartZ=0 EndX=30 EndY=-25 EndZ=0
    g2: LineSegment StartX=30 StartY=-25 StartZ=0 EndX=-30 EndY=-25 EndZ=0
    g3: LineSegment StartX=-30 StartY=-25 StartZ=0 EndX=-30 EndY=7.5 EndZ=0
    g4: LineSegment StartX=-30 StartY=7.5 StartZ=0 EndX=-17 EndY=7.5 EndZ=0
    g5: LineSegment StartX=-17 StartY=7.5 StartZ=0 EndX=-17 EndY=21.6256 EndZ=0
    g6: LineSegment StartX=17 StartY=21.6256 StartZ=0 EndX=17 EndY=7.5 EndZ=0
    g7: LineSegment StartX=17 StartY=7.5 StartZ=0 EndX=30 EndY=7.5 EndZ=0
    g8: Circle CenterX=0 CenterY=0 CenterZ=0 NormalX=0 NormalY=0 NormalZ=1 AngleXU=0 Radius=6
  constraints (24):
    c: Coincident(g1,g2)
    c: Coincident(g2,g3)
    c: Vertical(g1)
    c: DistanceX(g2,g2) = 60
    c: Symmetric(g2,g1,g-2)
    c: Horizontal(g4)
    c: Coincident(g5,g4)
    c: Vertical(g5)
    c: Coincident(g0,g5)
    c: Coincident(g3,g4)
    c: Vertical(g6)
    c: Coincident(g7,g6)
    c: Horizontal(g7)
    c: Coincident(g1,g7)
    c: Coincident(g0,g6)
    c: Symmetric(g0,g0,g-2)
    c: DistanceY(g3,g3) = 32.5
    c: Equal(g3,g1)
    c: Equal(g5,g6)
    c: Equal(g4,g7)
    c: DistanceX(g0,g0) = 34
    c: DistanceY(g1,g-1) = 25
    c: Coincident(g8,g-1)
    c: Radius(g8) = 6
FEATURE [PartDesign::Pad] Pad
  Direction = (0,0,1)
  Length = 35
  Length2 = 10
  Profile = -> Sketch
  ReferenceAxis = -> Sketch [N_Axis]
  Type = 0
FEATURE [Sketcher::SketchObject] Sketch001
  FullyConstrained = false
  MapMode = 5
  Placement = pos=(0,7.5,0) rot=(0,0.707107,0.707107;3.14159rad)
  Support = -> [Pad]
  sketch-geometry (3):
    g0: LineSegment StartX=-35.0154 StartY=15 StartZ=0 EndX=38.3815 EndY=15 EndZ=0
    g1: Circle CenterX=-23 CenterY=15 CenterZ=0 NormalX=0 NormalY=0 NormalZ=1 AngleXU=0 Radius=3.25
    g2: Circle CenterX=23 CenterY=15 CenterZ=0 NormalX=0 NormalY=0 NormalZ=1 AngleXU=0 Radius=3.25
  constraints (7):
    c: PointOnObject(g1,g0)
    c: PointOnObject(g2,g0)
    c: Equal(g1,g2)
    c: Radius(g1) = 3.25
    c: Symmetric(g1,g2,g-2)
    c: DistanceX(g1,g2) = 46
    c: DistanceY(g-1,g1) = 15
FEATURE [PartDesign::Pocket] Pocket
  BaseFeature = -> Pad
  Direction = (0,-1,2e-16)
  Length = 5
  Length2 = 5
  Profile = -> Sketch001
  ReferenceAxis = -> Sketch001 [N_Axis]
  Type = 1
FEATURE [PartDesign::CoordinateSystem] LCS_SupportoDoppioVite16x4
  AttacherType = Attacher::AttachEngine3D
FEATURE [PartDesign::Body] Body
  Group = -> [Sketch,Pad,Sketch001,Pocket,LCS_SupportoDoppioVite16x4]
  Origin = -> Origin
  Tip = -> Pocket
---- part ../SupportoSingoloVite16x4.FCStd = doc fcstd_60cc58ee6546 ----
FCSTD DOCUMENT  (FreeCAD 0.21R33771 (Git))
Label: SupportoSingoloVite16x4
License: All rights reserved
LicenseURL: http://en.wikipedia.org/wiki/All_rights_reserved
objects: Sketcher::SketchObject×2, PartDesign::Pad×1, PartDesign::Pocket×1, PartDesign::CoordinateSystem×1, PartDesign::Body×1
note: 8 computed .brp shape members not serialized (recipe doc carries the construction recipe); baked Part::Feature solids carry a one-line shape summary decoded from their .brp

FEATURE [Sketcher::SketchObject] Sketch
  FullyConstrained = true
  MapMode = 5
  Support = -> [XY_Plane]
  sketch-geometry (9):
    g0: LineSegment StartX=-17 StartY=21.6256 StartZ=0 EndX=17 EndY=21.6256 EndZ=0
    g1: LineSegment StartX=30 StartY=7.5 StartZ=0 EndX=30 EndY=-25 EndZ=0
    g2: LineSegment StartX=30 StartY=-25 StartZ=0 EndX=-30 EndY=-25 EndZ=0
    g3: LineSegment StartX=-30 StartY=-25 StartZ=0 EndX=-30 EndY=7.5 EndZ=0
    g4: LineSegment StartX=-30 StartY=7.5 StartZ=0 EndX=-17 EndY=7.5 EndZ=0
    g5: LineSegment StartX=-17 StartY=7.5 StartZ=0 EndX=-17 EndY=21.6256 EndZ=0
    g6: LineSegment StartX=17 StartY=21.6256 StartZ=0 EndX=17 EndY=7.5 EndZ=0
    g7: LineSegment StartX=17 StartY=7.5 StartZ=0 EndX=30 EndY=7.5 EndZ=0
    g8: Circle CenterX=0 CenterY=0 CenterZ=0 NormalX=0 NormalY=0 NormalZ=1 AngleXU=0 Radius=6
  constraints (24):
    c: Coincident(g1,g2)
    c: Coincident(g2,g3)
    c: Vertical(g1)
    c: DistanceX(g2,g2) = 60
    c: Symmetric(g2,g1,g-2)
    c: Horizontal(g4)
    c: Coincident(g5,g4)
    c: Vertical(g5)
    c: Coincident(g0,g5)
    c: Coincident(g3,g4)
    c: Vertical(g6)
    c: Coincident(g7,g6)
    c: Horizontal(g7)
    c: Coincident(g1,g7)
    c: Coincident(g0,g6)
    c: Symmetric(g0,g0,g-2)
    c: DistanceY(g3,g3) = 32.5
    c: Equal(g3,g1)
    c: Equal(g5,g6)
    c: Equal(g4,g7)
    c: DistanceX(g0,g0) = 34
    c: DistanceY(g1,g-1) = 25
    c: Coincident(g8,g-1)
    c: Radius(g8) = 6
FEATURE [PartDesign::Pad] Pad
  Direction = (0,0,1)
  Length = 20
  Length2 = 10
  Profile = -> Sketch
  ReferenceAxis = -> Sketch [N_Axis]
  Type = 0
FEATURE [Sketcher::SketchObject] Sketch001
  FullyConstrained = false
  MapMode = 5
  Placement = pos=(0,7.5,0) rot=(0,0.707107,0.707107;3.14159rad)
  Support = -> [Pad]
  sketch-geometry (3):
    g0: LineSegment StartX=-35.0148 StartY=10 StartZ=0 EndX=38.3816 EndY=10 EndZ=0
    g1: Circle CenterX=-23 CenterY=10 CenterZ=0 NormalX=0 NormalY=0 NormalZ=1 AngleXU=0 Radius=3.25
    g2: Circle CenterX=23 CenterY=10 CenterZ=0 NormalX=0 NormalY=0 NormalZ=1 AngleXU=0 Radius=3.25
  constraints (7):
    c: PointOnObject(g1,g0)
    c: PointOnObject(g2,g0)
    c: Equal(g1,g2)
    c: Radius(g1) = 3.25
    c: Symmetric(g1,g2,g-2)
    c: DistanceX(g1,g2) = 46
    c: DistanceY(g-1,g1) = 10
FEATURE [PartDesign::Pocket] Pocket
  BaseFeature = -> Pad
  Direction = (0,-1,2e-16)
  Length = 5
  Length2 = 5
  Profile = -> Sketch001
  ReferenceAxis = -> Sketch001 [N_Axis]
  Type = 1
FEATURE [PartDesign::CoordinateSystem] LCS_SupportoSingoloVite16x4
  AttacherType = Attacher::AttachEngine3D
FEATURE [PartDesign::Body] Body
  Group = -> [Sketch,Pad,Sketch001,Pocket,LCS_SupportoSingoloVite16x4]
  Origin = -> Origin
  Tip = -> Pocket
---- part ../TORRETTA/Chiocciola10x2.FCStd = doc fcstd_896a6d5d39c7 ----
FCSTD DOCUMENT  (FreeCAD 0.21R33771 (Git))
Label: Chiocciola10x2
License: All rights reserved
LicenseURL: http://en.wikipedia.org/wiki/All_rights_reserved
objects: Sketcher::SketchObject×3, PartDesign::Pad×2, PartDesign::CoordinateSystem×1, PartDesign::Pocket×1, PartDesign::Body×1
note: 11 computed .brp shape members not serialized (recipe doc carries the construction recipe); baked Part::Feature solids carry a one-line shape summary decoded from their .brp

FEATURE [PartDesign::CoordinateSystem] LCS_Chiocciola12x2
  AttacherType = Attacher::AttachEngine3D
FEATURE [Sketcher::SketchObject] Sketch
  FullyConstrained = true
  MapMode = 5
  Support = -> [XY_Plane]
  sketch-geometry (4):
    g0: ArcOfCircle CenterX=0 CenterY=0 CenterZ=0 NormalX=0 NormalY=0 NormalZ=1 AngleXU=0 Radius=16 StartAngle=2.54419 EndAngle=3.739
    g1: LineSegment StartX=-13.2288 StartY=9 StartZ=0 EndX=13.2288 EndY=9 EndZ=0
    g2: LineSegment StartX=-13.2288 StartY=-9 StartZ=0 EndX=13.2288 EndY=-9 EndZ=0
    g3: ArcOfCircle CenterX=0 CenterY=0 CenterZ=0 NormalX=0 NormalY=0 NormalZ=1 AngleXU=0 Radius=16 StartAngle=5.68578 EndAngle=6.88059
  constraints (12):
    c: Coincident(g0,g-1)
    c: Radius(g0) = 16
    c: Horizontal(g1)
    c: Coincident(g1,g3)
    c: Coincident(g1,g0)
    c: Horizontal(g2)
    c: Equal(g0,g3)
    c: Coincident(g0,g3)
    c: Coincident(g2,g3)
    c: Coincident(g2,g0)
    c: Equal(g2,g1)
    c: DistanceY(g0,g0) = 9
FEATURE [PartDesign::Pad] Pad
  Direction = (0,0,1)
  Length = 10
  Length2 = 10
  Profile = -> Sketch
  ReferenceAxis = -> Sketch [N_Axis]
  Type = 0
FEATURE [Sketcher::SketchObject] Sketch001
  FullyConstrained = true
  MapMode = 5
  Placement = pos=(0,0,0) rot=(1,0,0;3.14159rad)
  Support = -> [Pad]
  sketch-geometry (1):
    g0: Circle CenterX=0 CenterY=0 CenterZ=0 NormalX=0 NormalY=0 NormalZ=1 AngleXU=0 Radius=8
  constraints (2):
    c: Coincident(g0,g-1)
    c: Radius(g0) = 8
FEATURE [PartDesign::Pad] Pad001
  BaseFeature = -> Pad
  Direction = (0,0,-1)
  Length = 24
  Length2 = 10
  Profile = -> Sketch001
  ReferenceAxis = -> Sketch001 [N_Axis]
  Type = 0
FEATURE [Sketcher::SketchObject] Sketch002
  FullyConstrained = true
  MapMode = 5
  Placement = pos=(0,0,10) rot=(0,0,1;0rad)
  Support = -> [Pad001]
  sketch-geometry (4):
    g0: Circle CenterX=0 CenterY=0 CenterZ=0 NormalX=0 NormalY=0 NormalZ=1 AngleXU=0 Radius=5
    g1: Circle CenterX=0 CenterY=0 CenterZ=0 NormalX=0 NormalY=0 NormalZ=1 AngleXU=0 Radius=12
    g2: Circle CenterX=12 CenterY=0 CenterZ=0 NormalX=0 NormalY=0 NormalZ=1 AngleXU=0 Radius=2
    g3: Circle CenterX=-12 CenterY=0 CenterZ=0 NormalX=0 NormalY=0 NormalZ=1 AngleXU=0 Radius=2
  constraints (10):
    c: Coincident(g0,g-1)
    c: Radius(g0) = 5
    c: Coincident(g1,g0)
    c: PointOnObject(g2,g1)
    c: PointOnObject(g3,g1)
    c: Radius(g1) = 12
    c: PointOnObject(g2,g-1)
    c: PointOnObject(g3,g-1)
    c: Radius(g3) = 2
    c: Equal(g3,g2)
FEATURE [PartDesign::Pocket] Pocket
  BaseFeature = -> Pad001
  Direction = (0,0,-1)
  Length = 5
  Length2 = 5
  Profile = -> Sketch002
  ReferenceAxis = -> Sketch002 [N_Axis]
  Type = 1
FEATURE [PartDesign::Body] Body  label="Corpo"
  Group = -> [LCS_Chiocciola12x2,Sketch,Pad,Sketch001,Pad001,Sketch002,Pocket]
  Origin = -> Origin
  Tip = -> Pocket
---- part ../TORRETTA/Guida-quadra-15-300.FCStd = doc fcstd_cb140f93d65b ----
FCSTD DOCUMENT  (FreeCAD 0.21R33771 (Git))
Label: Guida-quadra-15-300
License: All rights reserved
LicenseURL: https://en.wikipedia.org/wiki/All_rights_reserved
objects: Sketcher::SketchObject×3, PartDesign::Pocket×2, PartDesign::Pad×1, PartDesign::CoordinateSystem×1, PartDesign::Body×1
note: 11 computed .brp shape members not serialized (recipe doc carries the construction recipe); baked Part::Feature solids carry a one-line shape summary decoded from their .brp

FEATURE [Sketcher::SketchObject] Sketch
  FullyConstrained = true
  MapMode = 5
  Support = -> [XY_Plane]
  sketch-geometry (10):
    g0: LineSegment StartX=-7 StartY=0 StartZ=0 EndX=7 EndY=0 EndZ=0
    g1: LineSegment StartX=7 StartY=14.5879 StartZ=0 EndX=-7 EndY=14.5879 EndZ=0
    g2: LineSegment StartX=-7.36485 StartY=13.7461 StartZ=0 EndX=-3 EndY=9.08793 EndZ=0
    g3: LineSegment StartX=-3 StartY=9.08793 StartZ=0 EndX=-7.44147 EndY=0.734736 EndZ=0
    g4: LineSegment StartX=7.36485 StartY=13.7461 StartZ=0 EndX=3 EndY=9.08793 EndZ=0
    g5: LineSegment StartX=3 StartY=9.08793 StartZ=0 EndX=7.44147 EndY=0.734736 EndZ=0
    g6: ArcOfCircle CenterX=-7 CenterY=0.5 CenterZ=0 NormalX=0 NormalY=0 NormalZ=1 AngleXU=0 Radius=0.5 StartAngle=2.6529 EndAngle=4.71239
    g7: ArcOfCircle CenterX=7 CenterY=0.5 CenterZ=0 NormalX=0 NormalY=0 NormalZ=1 AngleXU=0 Radius=0.5 StartAngle=4.71239 EndAngle=6.77188
    g8: ArcOfCircle CenterX=-7 CenterY=14.0879 CenterZ=0 NormalX=0 NormalY=0 NormalZ=1 AngleXU=0 Radius=0.5 StartAngle=1.5708 EndAngle=3.8945
    g9: ArcOfCircle CenterX=7 CenterY=14.0879 CenterZ=0 NormalX=0 NormalY=0 NormalZ=1 AngleXU=0 Radius=0.5 StartAngle=5.53028 EndAngle=7.85398
  constraints (23):
    c: Coincident(g3,g2)
    c: Coincident(g5,g4)
    c: Equal(g0,g1)
    c: Tangent(g3,g6) = -1.5708
    c: Tangent(g0,g6) = -1.5708
    c: Tangent(g5,g7) = 1.5708
    c: Tangent(g0,g7) = -1.5708
    c: Radius(g7) = 0.5
    c: Equal(g6,g7)
    c: Tangent(g2,g8) = -1.5708
    c: Tangent(g1,g8) = -1.5708
    c: Tangent(g1,g9) = -1.5708
    c: Tangent(g4,g9) = 1.5708
    c: Symmetric(g6,g7,g-2)
    c: Symmetric(g8,g9,g-2)
    c: Equal(g7,g9)
    c: Equal(g9,g8)
    c: Symmetric(g2,g4,g-2)
    c: DistanceX(g6,g7) = 14
    c: DistanceY(g4,g9) = 5
    c: DistanceX(g2,g-1) = 3
    c: PointOnObject(g-1,g0)
    c: Angle(g5,g0) = 1.0821
FEATURE [Sketcher::SketchObject] Sketch002
  FullyConstrained = false
  MapMode = 5
  Placement = pos=(0,14.5879,0) rot=(0,0.707107,0.707107;3.14159rad)
  sketch-geometry (9):
    g0: Circle CenterX=-1.76438e-11 CenterY=260 CenterZ=0 NormalX=0 NormalY=0 NormalZ=1 AngleXU=0 Radius=3.7
    g1: Circle CenterX=-1.3252e-11 CenterY=200 CenterZ=0 NormalX=0 NormalY=0 NormalZ=1 AngleXU=0 Radius=3.7
    g2: LineSegment StartX=-1.76438e-11 StartY=260 StartZ=0 EndX=-1.3252e-11 EndY=200 EndZ=0
    g3: Circle CenterX=3.67901e-11 CenterY=140 CenterZ=0 NormalX=0 NormalY=0 NormalZ=1 AngleXU=0 Radius=3.7
    g4: LineSegment StartX=-1.3252e-11 StartY=200 StartZ=0 EndX=3.67901e-11 EndY=140 EndZ=0
    g5: Circle CenterX=7.47349e-11 CenterY=80 CenterZ=0 NormalX=0 NormalY=0 NormalZ=1 AngleXU=0 Radius=3.7
    g6: LineSegment StartX=3.67901e-11 StartY=140 StartZ=0 EndX=7.47349e-11 EndY=80 EndZ=0
    g7: Circle CenterX=1.08711e-10 CenterY=20 CenterZ=0 NormalX=0 NormalY=0 NormalZ=1 AngleXU=0 Radius=3.7
    g8: LineSegment StartX=7.47349e-11 StartY=80 StartZ=0 EndX=1.08711e-10 EndY=20 EndZ=0
  constraints (19):
    c: Radius(g0) = 3.7
    c: Radius(g1) = 3.7
    c: Coincident(g0,g2)
    c: Coincident(g1,g2)
    c: Radius(g3) = 3.7
    c: Coincident(g1,g4)
    c: Coincident(g3,g4)
    c: Equal(g2,g4)
    c: Parallel(g4,g2)
    c: Radius(g5) = 3.7
    c: Coincident(g3,g6)
    c: Coincident(g5,g6)
    c: Equal(g2,g6)
    c: Parallel(g6,g2)
    c: Radius(g7) = 3.7
    c: Coincident(g5,g8)
    c: Coincident(g7,g8)
    c: Equal(g2,g8)
    c: Parallel(g8,g2)
FEATURE [PartDesign::Pad] Pad
  Direction = (0,0,1)
  Length = 300
  Length2 = 10
  Profile = -> Sketch
  ReferenceAxis = -> Sketch [N_Axis]
  Type = 0
FEATURE [Sketcher::SketchObject] Sketch001
  FullyConstrained = true
  MapMode = 5
  Placement = pos=(0,14.5879,0) rot=(0,0.707107,0.707107;3.14159rad)
  Support = -> [Pad]
  sketch-geometry (9):
    g0: Circle CenterX=0 CenterY=20 CenterZ=0 NormalX=0 NormalY=0 NormalZ=1 AngleXU=0 Radius=2.2
    g1: Circle CenterX=0 CenterY=80 CenterZ=0 NormalX=0 NormalY=0 NormalZ=1 AngleXU=0 Radius=2.2
    g2: LineSegment StartX=0 StartY=20 StartZ=0 EndX=0 EndY=80 EndZ=0
    g3: Circle CenterX=-9.85e-12 CenterY=140 CenterZ=0 NormalX=0 NormalY=0 NormalZ=1 AngleXU=0 Radius=2.2
    g4: LineSegment StartX=0 StartY=80 StartZ=0 EndX=-9.85e-12 EndY=140 EndZ=0
    g5: Circle CenterX=-1.3252e-11 CenterY=200 CenterZ=0 NormalX=0 NormalY=0 NormalZ=1 AngleXU=0 Radius=2.2
    g6: LineSegment StartX=-9.85e-12 StartY=140 StartZ=0 EndX=-1.3252e-11 EndY=200 EndZ=0
    g7: Circle CenterX=-1.76438e-11 CenterY=260 CenterZ=0 NormalX=0 NormalY=0 NormalZ=1 AngleXU=0 Radius=2.2
    g8: LineSegment StartX=-1.3252e-11 StartY=200 StartZ=0 EndX=-1.76438e-11 EndY=260 EndZ=0
  constraints (23):
    c: PointOnObject(g0,g-2)
    c: Radius(g0) = 2.2
    c: DistanceY(g-1,g0) = 20
    c: Radius(g1) = 2.2
    c: Coincident(g0,g2)
    c: Coincident(g1,g2)
    c: Distance(g2) = 60
    c: Radius(g3) = 2.2
    c: Coincident(g1,g4)
    c: Coincident(g3,g4)
    c: Equal(g2,g4)
    c: Parallel(g4,g2)
    c: Radius(g5) = 2.2
    c: Coincident(g3,g6)
    c: Coincident(g5,g6)
    c: Equal(g2,g6)
    c: Parallel(g6,g2)
    c: Radius(g7) = 2.2
    c: Coincident(g5,g8)
    c: Coincident(g7,g8)
    c: Equal(g2,g8)
    c: Parallel(g8,g2)
    c: PointOnObject(g1,g-2)
FEATURE [PartDesign::Pocket] Pocket
  BaseFeature = -> Pad
  Direction = (0,-1,2e-16)
  Length = 5
  Length2 = 5
  Profile = -> Sketch001
  ReferenceAxis = -> Sketch001 [N_Axis]
  Type = 1
FEATURE [PartDesign::Pocket] Pocket001
  BaseFeature = -> Pocket
  Direction = (0,-1,2e-16)
  Length = 5
  Length2 = 5
  Profile = -> Sketch002
  ReferenceAxis = -> Sketch002 [N_Axis]
  Type = 0
FEATURE [PartDesign::CoordinateSystem] LCS_GuidoQuadra15x300  label="LCS_GuidaQuadra15x300"
  AttacherType = Attacher::AttachEngine3D
FEATURE [PartDesign::Body] Body
  Group = -> [Sketch,Pad,Sketch001,Sketch002,Pocket,Pocket001,LCS_GuidoQuadra15x300]
  Origin = -> Origin
  Tip = -> Pocket001
---- part ../TORRETTA/Pattino-15.FCStd = doc fcstd_e89f70db5334 ----
FCSTD DOCUMENT  (FreeCAD 0.21R33771 (Git))
Label: Pattino-15
License: All rights reserved
LicenseURL: http://en.wikipedia.org/wiki/All_rights_reserved
objects: Sketcher::SketchObject×2, PartDesign::Pad×1, PartDesign::CoordinateSystem×1, PartDesign::Body×1
note: 6 computed .brp shape members not serialized (recipe doc carries the construction recipe); baked Part::Feature solids carry a one-line shape summary decoded from their .brp

FEATURE [Sketcher::SketchObject] Sketch
  FullyConstrained = true
  MapMode = 5
  Support = -> [XY_Plane]
  sketch-geometry (8):
    g0: LineSegment StartX=0 StartY=0 StartZ=0 EndX=9.5 EndY=0 EndZ=0
    g1: LineSegment StartX=34 StartY=0 StartZ=0 EndX=34 EndY=23 EndZ=0
    g2: LineSegment StartX=34 StartY=23 StartZ=0 EndX=0 EndY=23 EndZ=0
    g3: LineSegment StartX=0 StartY=23 StartZ=0 EndX=0 EndY=0 EndZ=0
    g4: LineSegment StartX=9.5 StartY=0 StartZ=0 EndX=9.5 EndY=14 EndZ=0
    g5: LineSegment StartX=9.5 StartY=14 StartZ=0 EndX=24.5 EndY=14 EndZ=0
    g6: LineSegment StartX=24.5 StartY=14 StartZ=0 EndX=24.5 EndY=0 EndZ=0
    g7: LineSegment StartX=24.5 StartY=0 StartZ=0 EndX=34 EndY=0 EndZ=0
  constraints (22):
    c: Coincident(g7,g1)
    c: Coincident(g1,g2)
    c: Coincident(g2,g3)
    c: Coincident(g3,g0)
    c: Horizontal(g0)
    c: Horizontal(g2)
    c: Vertical(g1)
    c: Vertical(g3)
    c: Coincident(g0,g-1)
    c: DistanceY(g1,g1) = 23
    c: DistanceX(g2,g2) = 34
    c: Vertical(g4)
    c: Coincident(g5,g4)
    c: Horizontal(g5)
    c: Coincident(g6,g5)
    c: Vertical(g6)
    c: Coincident(g0,g4)
    c: Coincident(g7,g6)
    c: Tangent(g0,g7)
    c: DistanceX(g5,g5) = 15
    c: DistanceX(g0,g0) = 9.5
    c: DistanceY(g6,g6) = 14
FEATURE [PartDesign::Pad] Pad
  Direction = (0,0,1)
  Length = 62
  Length2 = 100
  Profile = -> Sketch
  ReferenceAxis = -> Sketch [N_Axis]
  Type = 0
FEATURE [Sketcher::SketchObject] Sketch002
  FullyConstrained = true
  MapMode = 5
  Placement = pos=(0,23,0) rot=(0,0.707107,0.707107;3.14159rad)
  Support = -> [Pad]
  sketch-geometry (8):
    g0: LineSegment StartX=-30 StartY=48 StartZ=0 EndX=-30 EndY=14 EndZ=0
    g1: LineSegment StartX=-30 StartY=14 StartZ=0 EndX=-4 EndY=14 EndZ=0
    g2: Circle CenterX=-30 CenterY=48 CenterZ=0 NormalX=0 NormalY=0 NormalZ=1 AngleXU=0 Radius=2.1
    g3: Circle CenterX=-30 CenterY=14 CenterZ=0 NormalX=0 NormalY=0 NormalZ=1 AngleXU=0 Radius=0
    g4: Circle CenterX=-4 CenterY=14 CenterZ=0 NormalX=0 NormalY=0 NormalZ=1 AngleXU=0 Radius=2.1
    g5: Circle CenterX=-4 CenterY=48 CenterZ=0 NormalX=0 NormalY=0 NormalZ=1 AngleXU=0 Radius=2.1
    g6: LineSegment StartX=-30 StartY=48 StartZ=0 EndX=-4 EndY=48 EndZ=0
    g7: Circle CenterX=-30 CenterY=14 CenterZ=0 NormalX=0 NormalY=0 NormalZ=1 AngleXU=0 Radius=2.1
  constraints (20):
    c: Vertical(g0)
    c: Coincident(g1,g0)
    c: Horizontal(g1)
    c: Coincident(g2,g0)
    c: Coincident(g3,g0)
    c: Tangent(g3,g1)
    c: Coincident(g4,g1)
    c: Coincident(g6,g0)
    c: Coincident(g6,g5)
    c: Coincident(g7,g0)
    c: Equal(g2,g7)
    c: Equal(g2,g5)
    c: Equal(g2,g4)
    c: Radius(g2) = 2.1
    c: Horizontal(g5,g0)
    c: DistanceY(g0,g0) = 34
    c: Equal(g6,g1)
    c: DistanceX(g1,g1) = 26
    c: DistanceX(g1,g-1) = 4
    c: DistanceY(g-1,g1) = 14
FEATURE [PartDesign::CoordinateSystem] LCS_Pattino1  label="LCS_Pattino15"
  AttacherType = Attacher::AttachEngine3D
FEATURE [PartDesign::Body] Body
  Group = -> [Sketch,Pad,Sketch002,LCS_Pattino1]
  Origin = -> Origin
  Tip = -> Pad
---- part ../TORRETTA/PiastraAvanzamentoUtensile.FCStd = doc fcstd_66c77dab2aa1 ----
FCSTD DOCUMENT  (FreeCAD 0.21R33771 (Git))
Label: PiastraAvanzamentoUtensile
License: All rights reserved
LicenseURL: http://en.wikipedia.org/wiki/All_rights_reserved
objects: Part::FeaturePython×13, Sketcher::SketchObject×4, PartDesign::Pocket×3, PartDesign::Pad×1, PartDesign::CoordinateSystem×1, PartDesign::Body×1, App::DocumentObjectGroup×1
note: 27 computed .brp shape members not serialized (recipe doc carries the construction recipe); baked Part::Feature solids carry a one-line shape summary decoded from their .brp

FEATURE [Sketcher::SketchObject] Sketch
  FullyConstrained = true
  MapMode = 5
  Support = -> [XY_Plane]
  sketch-geometry (4):
    g0: LineSegment StartX=-45 StartY=20 StartZ=0 EndX=45 EndY=20 EndZ=0
    g1: LineSegment StartX=45 StartY=20 StartZ=0 EndX=45 EndY=-20 EndZ=0
    g2: LineSegment StartX=45 StartY=-20 StartZ=0 EndX=-45 EndY=-20 EndZ=0
    g3: LineSegment StartX=-45 StartY=-20 StartZ=0 EndX=-45 EndY=20 EndZ=0
  constraints (10):
    c: Coincident(g0,g1)
    c: Coincident(g1,g2)
    c: Coincident(g2,g3)
    c: Coincident(g3,g0)
    c: Horizontal(g0)
    c: Vertical(g1)
    c: Symmetric(g0,g2,g-1)
    c: Symmetric(g2,g1,g-2)
    c: DistanceX(g0,g0) = 90
    c: DistanceY(g1,g1) = 40
FEATURE [PartDesign::Pad] Pad
  Direction = (0,0,1)
  Length = 10
  Length2 = 10
  Profile = -> Sketch
  ReferenceAxis = -> Sketch [N_Axis]
  Type = 0
FEATURE [Sketcher::SketchObject] Sketch001
  FullyConstrained = true
  MapMode = 5
  Placement = pos=(0,0,10) rot=(0,0,1;0rad)
  Support = -> [Pad]
  sketch-geometry (4):
    g0: Circle CenterX=0 CenterY=7 CenterZ=0 NormalX=0 NormalY=0 NormalZ=1 AngleXU=0 Radius=6
    g1: LineSegment StartX=-30 StartY=-10 StartZ=0 EndX=30 EndY=-10 EndZ=0
    g2: Circle CenterX=-30 CenterY=-10 CenterZ=0 NormalX=0 NormalY=0 NormalZ=1 AngleXU=0 Radius=2.5
    g3: Circle CenterX=30 CenterY=-10 CenterZ=0 NormalX=0 NormalY=0 NormalZ=1 AngleXU=0 Radius=2.5
  constraints (10):
    c: PointOnObject(g0,g-2)
    c: DistanceY(g-1,g0) = 7
    c: Radius(g0) = 6
    c: Symmetric(g1,g1,g-2)
    c: DistanceX(g1,g1) = 60
    c: Coincident(g2,g1)
    c: Coincident(g3,g1)
    c: Radius(g2) = 2.5
    c: Equal(g2,g3)
    c: DistanceY(g3,g-1) = 10
FEATURE [PartDesign::Pocket] Pocket
  BaseFeature = -> Pad
  Direction = (0,0,-1)
  Length = 5
  Length2 = 5
  Profile = -> Sketch001
  ReferenceAxis = -> Sketch001 [N_Axis]
  Type = 1
FEATURE [Sketcher::SketchObject] Sketch002
  ExternalGeometry = -> [Pocket]
  FullyConstrained = true
  MapMode = 5
  Placement = pos=(0,0,10) rot=(0,0,1;0rad)
  Support = -> [Pocket]
  sketch-geometry (3):
    g0: Circle CenterX=30 CenterY=-10 CenterZ=0 NormalX=0 NormalY=0 NormalZ=1 AngleXU=0 Radius=4
    g1: Circle CenterX=0 CenterY=7 CenterZ=0 NormalX=0 NormalY=0 NormalZ=1 AngleXU=0 Radius=4
    g2: Circle CenterX=-30 CenterY=-10 CenterZ=0 NormalX=0 NormalY=0 NormalZ=1 AngleXU=0 Radius=4
  constraints (6):
    c: Radius(g0) = 4
    c: Coincident(g1,g-3)
    c: Equal(g0,g1)
    c: Coincident(g0,g-4)
    c: Coincident(g2,g-5)
    c: Equal(g2,g0)
FEATURE [PartDesign::Pocket] Pocket001
  BaseFeature = -> Pocket
  Direction = (0,0,-1)
  Length = 5
  Length2 = 5
  Profile = -> Sketch002
  ReferenceAxis = -> Sketch002 [N_Axis]
  Type = 0
FEATURE [Sketcher::SketchObject] Sketch004
  ExternalGeometry = -> [Pocket001]
  FullyConstrained = true
  MapMode = 5
  Placement = pos=(0,0,0) rot=(1,0,0;3.14159rad)
  Support = -> [Pocket001]
  sketch-geometry (1):
    g0: Circle CenterX=0 CenterY=-7 CenterZ=0 NormalX=0 NormalY=0 NormalZ=1 AngleXU=0 Radius=11
  constraints (2):
    c: Coincident(g0,g-3)
    c: Radius(g0) = 11
FEATURE [PartDesign::Pocket] Pocket003
  BaseFeature = -> Pocket001
  Direction = (0,0,1)
  Length = 7
  Length2 = 5
  Profile = -> Sketch004
  ReferenceAxis = -> Sketch004 [N_Axis]
  Type = 0
FEATURE [Part::FeaturePython] PtS  # WARN: FeaturePython — macro-defined, semantics opaque (R4)
FEATURE [Part::FeaturePython] PtS001 .. PtS006  x6 (patterned run collapsed; names and placements below)
FEATURE [PartDesign::CoordinateSystem] LCS_PiastraAvanzamentoViteUtensile
  AttacherType = Attacher::AttachEngine3D
FEATURE [PartDesign::Body] Body  label="Corpo"
  Group = -> [Sketch,Pad,Sketch001,Pocket,Sketch002,Pocket001,Sketch004,Pocket003,LCS_PiastraAvanzamentoViteUtensile]
  Origin = -> Origin
  Tip = -> Pocket003
FEATURE [Part::FeaturePython] PtS007 .. PtS012  x6 (patterned run collapsed; names and placements below)
FEATURE [App::DocumentObjectGroup] Measures
  Group = -> [PtS,PtS001,PtS002,PtS003,PtS004,PtS005,PtS006,PtS007,PtS008,PtS009,PtS010,PtS011,PtS012]
---- part ../TORRETTA/SupportoChiocciolaRicircolo12.FCStd = doc fcstd_6511eaec8bd5 ----
FCSTD DOCUMENT  (FreeCAD 0.21R33771 (Git))
Label: SupportoChiocciolaRicircolo12
License: All rights reserved
LicenseURL: http://en.wikipedia.org/wiki/All_rights_reserved
objects: Sketcher::SketchObject×1, PartDesign::Pad×1, PartDesign::CoordinateSystem×1, PartDesign::Body×1
note: 5 computed .brp shape members not serialized (recipe doc carries the construction recipe); baked Part::Feature solids carry a one-line shape summary decoded from their .brp

FEATURE [Sketcher::SketchObject] Sketch
  FullyConstrained = false
  MapMode = 5
  Support = -> [XY_Plane]
  sketch-geometry (14):
    g0: LineSegment StartX=-16 StartY=13 StartZ=0 EndX=16 EndY=13 EndZ=0
    g1: LineSegment StartX=16 StartY=13 StartZ=0 EndX=16 EndY=-13 EndZ=0
    g2: LineSegment StartX=16 StartY=-13 StartZ=0 EndX=-16 EndY=-13 EndZ=0
    g3: LineSegment StartX=-16 StartY=-13 StartZ=0 EndX=-16 EndY=13 EndZ=0
    g4: Circle CenterX=-2e-16 CenterY=0 CenterZ=0 NormalX=0 NormalY=0 NormalZ=1 AngleXU=0 Radius=8.5
    g5: Circle CenterX=-2e-16 CenterY=0 CenterZ=0 NormalX=0 NormalY=0 NormalZ=1 AngleXU=0 Radius=12
    g6: Circle CenterX=-8.48528 CenterY=8.48528 CenterZ=0 NormalX=0 NormalY=0 NormalZ=1 AngleXU=0 Radius=2.1
    g7: Circle CenterX=8.48528 CenterY=8.48528 CenterZ=0 NormalX=0 NormalY=0 NormalZ=1 AngleXU=0 Radius=2.1
    g8: Circle CenterX=-12 CenterY=0 CenterZ=0 NormalX=0 NormalY=0 NormalZ=1 AngleXU=0 Radius=2.1
    g9: Circle CenterX=8.48528 CenterY=-8.48528 CenterZ=0 NormalX=0 NormalY=0 NormalZ=1 AngleXU=0 Radius=2.1
    g10: Circle CenterX=12 CenterY=0 CenterZ=0 NormalX=0 NormalY=0 NormalZ=1 AngleXU=0 Radius=2.1
    g11: Circle CenterX=-8.48528 CenterY=-8.48528 CenterZ=0 NormalX=0 NormalY=0 NormalZ=1 AngleXU=0 Radius=2.1
    g12: LineSegment StartX=-16.0802 StartY=-16.0802 StartZ=0 EndX=16.7185 EndY=16.7185 EndZ=0
    g13: LineSegment StartX=-17.8445 StartY=17.8445 StartZ=0 EndX=17.734 EndY=-17.734 EndZ=0
  constraints (36):
    c: Coincident(g0,g1)
    c: Coincident(g1,g2)
    c: Coincident(g2,g3)
    c: Coincident(g3,g0)
    c: Horizontal(g0)
    c: Vertical(g1)
    c: Symmetric(g2,g1,g-2)
    c: DistanceX(g2,g2) = 32
    c: Coincident(g4,g-1)
    c: Radius(g4) = 8.5
    c: DistanceY(g3,g3) = 26
    c: Symmetric(g0,g2,g-1)
    c: Coincident(g5,g4)
    c: Radius(g5) = 12
    c: PointOnObject(g6,g5)
    c: PointOnObject(g7,g5)
    c: PointOnObject(g8,g5)
    c: PointOnObject(g9,g5)
    c: PointOnObject(g10,g5)
    c: Radius(g6) = 2.1
    c: Equal(g6,g7)
    c: Equal(g7,g10)
    c: Equal(g10,g9)
    c: Equal(g9,g8)
    c: Equal(g11,g9)
    c: Tangent(g11,g5) = -1.5708
    c: PointOnObject(g4,g13)
    c: PointOnObject(g4,g12)
    c: Angle(g-1,g13) = 2.35619
    c: Angle(g-1,g12) = 0.785398
    c: PointOnObject(g11,g12)
    c: Tangent(g9,g13) = -1.5708
    c: PointOnObject(g8,g-1)
    c: PointOnObject(g6,g13)
    c: PointOnObject(g7,g12)
    c: PointOnObject(g10,g-1)
FEATURE [PartDesign::Pad] Pad
  Direction = (0,0,1)
  Length = 8
  Length2 = 10
  Profile = -> Sketch
  ReferenceAxis = -> Sketch [N_Axis]
  Type = 0
FEATURE [PartDesign::CoordinateSystem] LCS_SupportoChiocciolaRicircolo12
  AttacherType = Attacher::AttachEngine3D
FEATURE [PartDesign::Body] Body
  Group = -> [Sketch,Pad,LCS_SupportoChiocciolaRicircolo12]
  Origin = -> Origin
  Tip = -> Pad
---- part ../TORRETTA/TorrettaPortaUtensile.FCStd = doc fcstd_b46dbb66b17f ----
FCSTD DOCUMENT  (FreeCAD 0.21R33771 (Git))
Label: TorrettaPortaUtensile
License: All rights reserved
LicenseURL: https://en.wikipedia.org/wiki/All_rights_reserved
objects: Sketcher::SketchObject×5, PartDesign::Pad×3, PartDesign::Pocket×2, PartDesign::CoordinateSystem×1, PartDesign::Body×1
note: 17 computed .brp shape members not serialized (recipe doc carries the construction recipe); baked Part::Feature solids carry a one-line shape summary decoded from their .brp

FEATURE [Sketcher::SketchObject] Sketch
  FullyConstrained = true
  MapMode = 5
  Placement = pos=(0,0,0) rot=(1,0,0;1.5708rad)
  Support = -> [XZ_Plane]
  sketch-geometry (4):
    g0: LineSegment StartX=-40 StartY=40 StartZ=0 EndX=40 EndY=40 EndZ=0
    g1: LineSegment StartX=40 StartY=40 StartZ=0 EndX=40 EndY=-40 EndZ=0
    g2: LineSegment StartX=40 StartY=-40 StartZ=0 EndX=-40 EndY=-40 EndZ=0
    g3: LineSegment StartX=-40 StartY=-40 StartZ=0 EndX=-40 EndY=40 EndZ=0
  constraints (10):
    c: Coincident(g0,g1)
    c: Coincident(g1,g2)
    c: Coincident(g2,g3)
    c: Coincident(g3,g0)
    c: Horizontal(g0)
    c: Vertical(g1)
    c: Symmetric(g0,g2,g-1)
    c: Symmetric(g2,g1,g-2)
    c: DistanceX(g0,g0) = 80
    c: DistanceY(g3,g3) = 80
FEATURE [PartDesign::Pad] Pad
  Direction = (0,-1,2e-16)
  Length = 10
  Length2 = 10
  Placement = pos=(0,0,0) rot=(1,0,0;1.5708rad)
  Profile = -> Sketch
  ReferenceAxis = -> Sketch [N_Axis]
  Type = 0
FEATURE [Sketcher::SketchObject] Sketch001
  FullyConstrained = true
  MapMode = 5
  Placement = pos=(0,-10,4.4e-15) rot=(1,0,0;1.5708rad)
  Support = -> [Pad]
  sketch-geometry (4):
    g0: LineSegment StartX=-20 StartY=20 StartZ=0 EndX=20 EndY=20 EndZ=0
    g1: LineSegment StartX=20 StartY=20 StartZ=0 EndX=20 EndY=-20 EndZ=0
    g2: LineSegment StartX=20 StartY=-20 StartZ=0 EndX=-20 EndY=-20 EndZ=0
    g3: LineSegment StartX=-20 StartY=-20 StartZ=0 EndX=-20 EndY=20 EndZ=0
  constraints (10):
    c: Coincident(g0,g1)
    c: Coincident(g1,g2)
    c: Coincident(g2,g3)
    c: Coincident(g3,g0)
    c: Horizontal(g0)
    c: Vertical(g1)
    c: Symmetric(g2,g1,g-2)
    c: Symmetric(g0,g2,g-1)
    c: DistanceX(g2,g2) = 40
    c: DistanceY(g3,g3) = 40
FEATURE [PartDesign::Pad] Pad001
  BaseFeature = -> Pad
  Direction = (0,-1,2e-16)
  Length = 20
  Length2 = 10
  Placement = pos=(0,0,0) rot=(1,0,0;1.5708rad)
  Profile = -> Sketch001
  ReferenceAxis = -> Sketch001 [N_Axis]
  Type = 0
FEATURE [Sketcher::SketchObject] Sketch002
  ExternalGeometry = -> [Pad001]
  FullyConstrained = true
  MapMode = 5
  Placement = pos=(0,-30,1.48e-14) rot=(1,0,0;1.5708rad)
  Support = -> [Pad001]
  sketch-geometry (4):
    g0: LineSegment StartX=-40 StartY=40 StartZ=0 EndX=40 EndY=40 EndZ=0
    g1: LineSegment StartX=40 StartY=40 StartZ=0 EndX=40 EndY=-40 EndZ=0
    g2: LineSegment StartX=40 StartY=-40 StartZ=0 EndX=-40 EndY=-40 EndZ=0
    g3: LineSegment StartX=-40 StartY=-40 StartZ=0 EndX=-40 EndY=40 EndZ=0
  constraints (10):
    c: Coincident(g0,g1)
    c: Coincident(g1,g2)
    c: Coincident(g2,g3)
    c: Coincident(g3,g0)
    c: Horizontal(g0)
    c: Horizontal(g2)
    c: Vertical(g1)
    c: Vertical(g3)
    c: Coincident(g0,g-3)
    c: Coincident(g1,g-4)
FEATURE [PartDesign::Pad] Pad002
  BaseFeature = -> Pad001
  Direction = (0,-1,2e-16)
  Length = 15
  Length2 = 10
  Placement = pos=(0,0,0) rot=(1,0,0;1.5708rad)
  Profile = -> Sketch002
  ReferenceAxis = -> Sketch002 [N_Axis]
  Type = 0
FEATURE [Sketcher::SketchObject] Sketch003
  FullyConstrained = true
  MapMode = 5
  Placement = pos=(0,-45,2.21e-14) rot=(1,0,0;1.5708rad)
  Support = -> [Pad002]
  sketch-geometry (12):
    g0: LineSegment StartX=-30 StartY=30 StartZ=0 EndX=30 EndY=30 EndZ=0
    g1: LineSegment StartX=30 StartY=30 StartZ=0 EndX=30 EndY=-30 EndZ=0
    g2: LineSegment StartX=30 StartY=-30 StartZ=0 EndX=-30 EndY=-30 EndZ=0
    g3: LineSegment StartX=-30 StartY=-30 StartZ=0 EndX=-30 EndY=30 EndZ=0
    g4: Circle CenterX=-30 CenterY=30 CenterZ=0 NormalX=0 NormalY=0 NormalZ=1 AngleXU=0 Radius=4
    g5: Circle CenterX=30 CenterY=30 CenterZ=0 NormalX=0 NormalY=0 NormalZ=1 AngleXU=0 Radius=4
    g6: Circle CenterX=30 CenterY=-30 CenterZ=0 NormalX=0 NormalY=0 NormalZ=1 AngleXU=0 Radius=4
    g7: Circle CenterX=-30 CenterY=-30 CenterZ=0 NormalX=0 NormalY=0 NormalZ=1 AngleXU=0 Radius=4
    g8: Circle CenterX=0 CenterY=-30 CenterZ=0 NormalX=0 NormalY=0 NormalZ=1 AngleXU=0 Radius=4
    g9: Circle CenterX=0 CenterY=30 CenterZ=0 NormalX=0 NormalY=0 NormalZ=1 AngleXU=0 Radius=4
    g10: Circle CenterX=-30 CenterY=0 CenterZ=0 NormalX=0 NormalY=0 NormalZ=1 AngleXU=0 Radius=4
    g11: Circle CenterX=30 CenterY=0 CenterZ=0 NormalX=0 NormalY=0 NormalZ=1 AngleXU=0 Radius=4
  constraints (30):
    c: Coincident(g0,g1)
    c: Coincident(g1,g2)
    c: Coincident(g2,g3)
    c: Coincident(g3,g0)
    c: Horizontal(g0)
    c: Vertical(g1)
    c: Symmetric(g0,g2,g-1)
    c: Symmetric(g2,g1,g-2)
    c: DistanceX(g0,g0) = 60
    c: DistanceY(g1,g1) = 60
    c: Coincident(g4,g0)
    c: Coincident(g5,g0)
    c: Coincident(g6,g1)
    c: Coincident(g7,g2)
    c: PointOnObject(g8,g2)
    c: PointOnObject(g9,g0)
    c: Radius(g4) = 4
    c: Equal(g4,g9)
    c: Equal(g9,g5)
    c: Equal(g5,g6)
    c: Equal(g6,g8)
    c: Equal(g8,g7)
    c: PointOnObject(g9,g-2)
    c: PointOnObject(g8,g-2)
    c: PointOnObject(g10,g3)
    c: PointOnObject(g11,g1)
    c: Equal(g4,g10)
    c: Equal(g10,g11)
    c: PointOnObject(g10,g-1)
    c: PointOnObject(g11,g-1)
FEATURE [PartDesign::Pocket] Pocket
  BaseFeature = -> Pad002
  Direction = (0,1,-2e-16)
  Length = 0
  Length2 = 5
  Placement = pos=(0,0,0) rot=(1,0,0;1.5708rad)
  Profile = -> Sketch003
  ReferenceAxis = -> Sketch003 [N_Axis]
  Type = 3
  UpToFace = -> Pad002 [Face4]
FEATURE [Sketcher::SketchObject] Sketch004
  FullyConstrained = true
  MapMode = 5
  Placement = pos=(0,-45,2.21e-14) rot=(1,0,0;1.5708rad)
  Support = -> [Pocket]
  sketch-geometry (1):
    g0: Circle CenterX=0 CenterY=0 CenterZ=0 NormalX=0 NormalY=0 NormalZ=1 AngleXU=0 Radius=6
  constraints (2):
    c: Coincident(g0,g-1)
    c: Radius(g0) = 6
FEATURE [PartDesign::CoordinateSystem] LCS_TorrettaPortaUtensile
  AttacherType = Attacher::AttachEngine3D
  MapMode = 11
  Placement = pos=(0,0,2e-15) rot=(0.57735,-0.57735,0.57735;2.0944rad)
FEATURE [PartDesign::Pocket] Pocket001
  BaseFeature = -> Pocket
  Direction = (0,1,-4e-16)
  Length = 5
  Length2 = 5
  Placement = pos=(0,0,0) rot=(1,0,0;1.5708rad)
  Profile = -> Sketch004
  ReferenceAxis = -> Sketch004 [N_Axis]
  Type = 1
FEATURE [PartDesign::Body] Body  label="Corpo"
  Group = -> [Sketch,Pad,Sketch001,Pad001,Sketch002,Pad002,Sketch003,Pocket,Sketch004,LCS_TorrettaPortaUtensile,Pocket001]
  Origin = -> Origin
  Tip = -> Pocket001
---- part ../TORRETTA/ViteTrapezioT10.FCStd = doc fcstd_1040ce33b0e0 ----
FCSTD DOCUMENT  (FreeCAD 0.21R33771 (Git))
Label: ViteTrapezioT10
License: All rights reserved
LicenseURL: http://en.wikipedia.org/wiki/All_rights_reserved
objects: Sketcher::SketchObject×1, PartDesign::Pad×1, PartDesign::CoordinateSystem×1, PartDesign::Body×1
note: 5 computed .brp shape members not serialized (recipe doc carries the construction recipe); baked Part::Feature solids carry a one-line shape summary decoded from their .brp

FEATURE [Sketcher::SketchObject] Sketch
  FullyConstrained = true
  MapMode = 5
  Support = -> [XY_Plane]
  sketch-geometry (1):
    g0: Circle CenterX=0 CenterY=0 CenterZ=0 NormalX=0 NormalY=0 NormalZ=1 AngleXU=0 Radius=6
  constraints (2):
    c: Coincident(g0,g-1)
    c: Radius(g0) = 6
FEATURE [PartDesign::Pad] Pad
  Direction = (0,0,1)
  Length = 400
  Length2 = 10
  Profile = -> Sketch
  ReferenceAxis = -> Sketch [N_Axis]
  Type = 0
FEATURE [PartDesign::CoordinateSystem] LCS_ViteTrapezioT10
  AttacherType = Attacher::AttachEngine3D
FEATURE [PartDesign::Body] Body  label="Corpo"
  Group = -> [Sketch,Pad,LCS_ViteTrapezioT10]
  Origin = -> Origin
  Tip = -> Pad
---- part ../ViteCarro16x4.FCStd = doc fcstd_e6d48d017ebc ----
FCSTD DOCUMENT  (FreeCAD 0.21R33771 (Git))
Label: ViteCarro16x4
License: All rights reserved
LicenseURL: http://en.wikipedia.org/wiki/All_rights_reserved
objects: Sketcher::SketchObject×1, PartDesign::CoordinateSystem×1, PartDesign::Revolution×1, PartDesign::Body×1
note: 5 computed .brp shape members not serialized (recipe doc carries the construction recipe); baked Part::Feature solids carry a one-line shape summary decoded from their .brp

FEATURE [Sketcher::SketchObject] Sketch
  FullyConstrained = true
  MapMode = 5
  Support = -> [XY_Plane]
  sketch-geometry (8):
    g0: LineSegment StartX=0 StartY=0 StartZ=0 EndX=0 EndY=5 EndZ=0
    g1: LineSegment StartX=0 StartY=5 StartZ=0 EndX=55 EndY=5 EndZ=0
    g2: LineSegment StartX=55 StartY=5 StartZ=0 EndX=55 EndY=8 EndZ=0
    g3: LineSegment StartX=55 StartY=8 StartZ=0 EndX=575 EndY=8 EndZ=0
    g4: LineSegment StartX=575 StartY=8 StartZ=0 EndX=575 EndY=5 EndZ=0
    g5: LineSegment StartX=575 StartY=5 StartZ=0 EndX=600 EndY=5 EndZ=0
    g6: LineSegment StartX=600 StartY=5 StartZ=0 EndX=600 EndY=0 EndZ=0
    g7: LineSegment StartX=600 StartY=0 StartZ=0 EndX=0 EndY=0 EndZ=0
  constraints (23):
    c: Coincident(g0,g-1)
    c: PointOnObject(g0,g-2)
    c: Coincident(g1,g0)
    c: Horizontal(g1)
    c: Coincident(g2,g1)
    c: Vertical(g2)
    c: Coincident(g3,g2)
    c: Horizontal(g3)
    c: Coincident(g4,g3)
    c: Vertical(g4)
    c: Coincident(g5,g4)
    c: Horizontal(g5)
    c: Coincident(g6,g5)
    c: PointOnObject(g6,g-1)
    c: Vertical(g6)
    c: Coincident(g7,g6)
    c: Coincident(g7,g0)
    c: DistanceY(g0,g0) = 5
    c: DistanceY(g2,g2) = 3
    c: Equal(g2,g4)
    c: DistanceX(g3,g3) = 520
    c: DistanceX(g7,g7) = 600
    c: DistanceX(g5,g5) = 25
FEATURE [PartDesign::CoordinateSystem] LCS_ViteCarro16x4
  AttacherType = Attacher::AttachEngine3D
FEATURE [PartDesign::Revolution] Revolution
  Angle = 360
  Axis = (1,0,0)
  Base = (0,0,0)
  Profile = -> Sketch
  ReferenceAxis = -> Sketch [H_Axis]
FEATURE [PartDesign::Body] Body
  Group = -> [Sketch,LCS_ViteCarro16x4,Revolution]
  Origin = -> Origin
  Tip = -> Revolution
